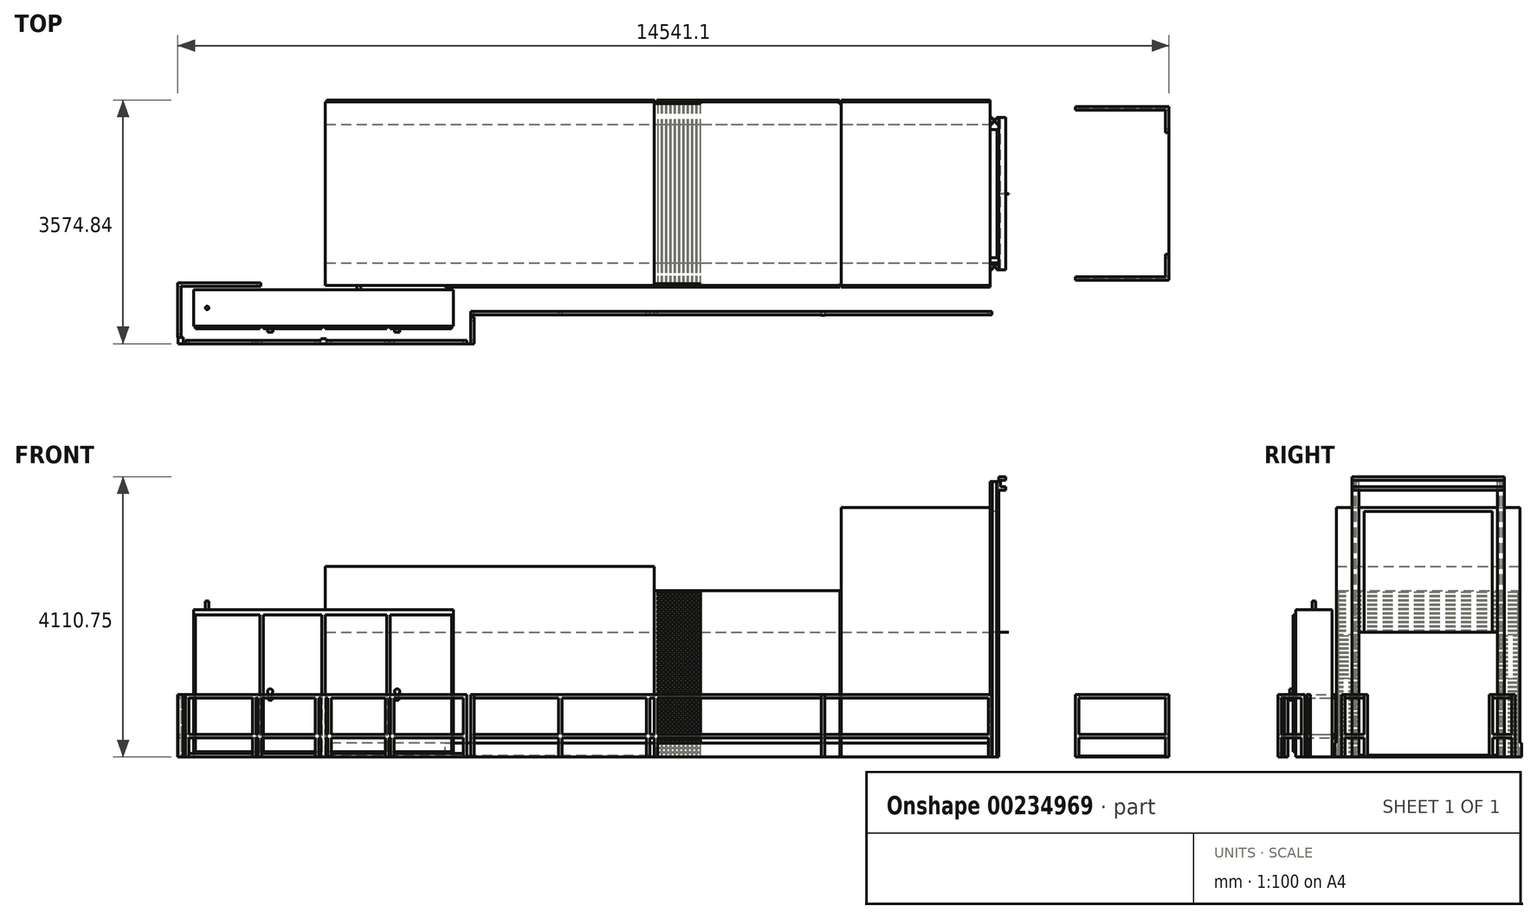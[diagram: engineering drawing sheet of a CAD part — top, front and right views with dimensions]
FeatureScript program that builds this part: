
annotation { "Feature Type Name" : "Feature", "Feature Type Description" : "" }
export const myFeature = defineFeature(function(context is Context, id is Id, definition is map)
    precondition{}
    {
        {
            var Q0;
            Q0=qCreatedBy(makeId("Top.planeOp"),FACE);
            var sketch = newSketch(context, id + "F0", { "sketchPlane" : qUnion([Q0])});
            skLineSegment(sketch, "E0.bottom", {"start": v(-1017.68, -307.3) * mm, "end": v(2792.32, -307.3) * mm});
            skLineSegment(sketch, "E0.top", {"start": v(-1017.68, 226.1) * mm, "end": v(2792.32, 226.1) * mm});
            skLineSegment(sketch, "E0.left", {"start": v(-1017.68, -307.3) * mm, "end": v(-1017.68, 226.1) * mm});
            skLineSegment(sketch, "E0.right", {"start": v(2792.32, -307.3) * mm, "end": v(2792.32, 226.1) * mm});
            skLineSegment(sketch, "E1.bottom", {"start": v(912.72, 289.6) * mm, "end": v(5738.72, 289.6) * mm});
            skLineSegment(sketch, "E1.top", {"start": v(912.72, 2982) * mm, "end": v(5738.72, 2982) * mm});
            skLineSegment(sketch, "E1.left", {"start": v(912.72, 289.6) * mm, "end": v(912.72, 2982) * mm});
            skLineSegment(sketch, "E1.right", {"start": v(5738.72, 289.6) * mm, "end": v(5738.72, 2982) * mm});
            skLineSegment(sketch, "E2.bottom", {"start": v(5738.72, 289.6) * mm, "end": v(8481.92, 289.6) * mm});
            skLineSegment(sketch, "E2.top", {"start": v(5738.72, 2982) * mm, "end": v(8481.92, 2982) * mm});
            skLineSegment(sketch, "E2.right", {"start": v(8481.92, 289.6) * mm, "end": v(8481.92, 2982) * mm});
            skLineSegment(sketch, "E3.bottom", {"start": v(8481.92, 289.6) * mm, "end": v(10666.32, 289.6) * mm});
            skLineSegment(sketch, "E3.top", {"start": v(8481.92, 2982) * mm, "end": v(10666.32, 2982) * mm});
            skLineSegment(sketch, "E3.right", {"start": v(10666.32, 289.6) * mm, "end": v(10666.32, 2982) * mm});
            skSolve(sketch);
        }
        {
            var Q0;
            Q0=makeQuery(id+"F0.imprint","IMPRINT",FACE,{"disambiguationData":[TD([[makeQuery(id+"F0.imprint","IMPRINT",EDGE,{"derivedFrom":sQuery(id+"F0.wireOp",EDGE,"E0.bottom")}),1.0]])]});
            extrude(context, id + "F1", {"entities" : qUnion([Q0]), "depth" : 2159 * mm});
        }
        {
            var Q0;
            Q0=makeQuery(id+"F0.imprint","IMPRINT",FACE,{"disambiguationData":[TD([[makeQuery(id+"F0.imprint","IMPRINT",EDGE,{"derivedFrom":sQuery(id+"F0.wireOp",EDGE,"E1.bottom")}),1.0]])]});
            extrude(context, id + "F2", {"entities" : qUnion([Q0]), "depth" : 2794 * mm});
        }
        {
            var Q0;
            Q0=makeQuery(id+"F0.imprint","IMPRINT",FACE,{"disambiguationData":[TD([[makeQuery(id+"F0.imprint","IMPRINT",EDGE,{"derivedFrom":sQuery(id+"F0.wireOp",EDGE,"E2.bottom")}),1.0]])]});
            extrude(context, id + "F3", {"entities" : qUnion([Q0]), "operationType" : NewBodyOperationType.ADD, "depth" : 2438.4 * mm});
        }
        {
            var Q0;
            Q0=makeQuery(id+"F0.imprint","IMPRINT",FACE,{"disambiguationData":[TD([[makeQuery(id+"F0.imprint","IMPRINT",EDGE,{"derivedFrom":sQuery(id+"F0.wireOp",EDGE,"E3.bottom")}),1.0]])]});
            extrude(context, id + "F4", {"entities" : qUnion([Q0]), "operationType" : NewBodyOperationType.ADD, "depth" : 3657.6 * mm});
        }
        {
            var Q0;
            Q0=makeQuery(id+"F4.boolean.opBoolean","MERGE",FACE,{"derivedFrom":[makeQuery(id+"F3.boolean.opBoolean","MERGE",FACE,{"derivedFrom":[makeQuery(id+"F2.opExtrude","SWEPT_FACE",FACE,{"disambiguationData":[OSD([sQuery(id+"F0.wireOp",EDGE,"E1.bottom")])]}),makeQuery(id+"F3.opExtrude","SWEPT_FACE",FACE,{"disambiguationData":[OSD([sQuery(id+"F0.wireOp",EDGE,"E2.bottom")])]})]}),makeQuery(id+"F4.opExtrude","SWEPT_FACE",FACE,{"disambiguationData":[OSD([sQuery(id+"F0.wireOp",EDGE,"E3.bottom")])]})]});
            var sketch = newSketch(context, id + "F5", { "sketchPlane" : qUnion([Q0])});
            skLineSegment(sketch, "E4.bottom", {"start": v(5787.37, 2413.96) * mm, "end": v(5838.17, 2413.96) * mm});
            skLineSegment(sketch, "E4.top", {"start": v(5787.37, 2363.16) * mm, "end": v(5838.17, 2363.16) * mm});
            skLineSegment(sketch, "E4.left", {"start": v(5787.37, 2413.96) * mm, "end": v(5787.37, 2363.16) * mm});
            skLineSegment(sketch, "E4.right", {"start": v(5838.17, 2413.96) * mm, "end": v(5838.17, 2363.16) * mm});
            skLineSegment(sketch, "E5.0.1.0", {"start": v(5787.37, 2350.46) * mm, "end": v(5838.17, 2350.46) * mm});
            skLineSegment(sketch, "E5.0.1.1", {"start": v(5838.17, 2350.46) * mm, "end": v(5838.17, 2299.66) * mm});
            skLineSegment(sketch, "E5.0.1.2", {"start": v(5787.37, 2350.46) * mm, "end": v(5787.37, 2299.66) * mm});
            skLineSegment(sketch, "E5.0.1.3", {"start": v(5787.37, 2299.66) * mm, "end": v(5838.17, 2299.66) * mm});
            skLineSegment(sketch, "E5.0.2.0", {"start": v(5787.37, 2286.96) * mm, "end": v(5838.17, 2286.96) * mm});
            skLineSegment(sketch, "E5.0.2.1", {"start": v(5838.17, 2286.96) * mm, "end": v(5838.17, 2236.16) * mm});
            skLineSegment(sketch, "E5.0.2.2", {"start": v(5787.37, 2286.96) * mm, "end": v(5787.37, 2236.16) * mm});
            skLineSegment(sketch, "E5.0.2.3", {"start": v(5787.37, 2236.16) * mm, "end": v(5838.17, 2236.16) * mm});
            skLineSegment(sketch, "E5.0.3.0", {"start": v(5787.37, 2223.46) * mm, "end": v(5838.17, 2223.46) * mm});
            skLineSegment(sketch, "E5.0.3.1", {"start": v(5838.17, 2223.46) * mm, "end": v(5838.17, 2172.66) * mm});
            skLineSegment(sketch, "E5.0.3.2", {"start": v(5787.37, 2223.46) * mm, "end": v(5787.37, 2172.66) * mm});
            skLineSegment(sketch, "E5.0.3.3", {"start": v(5787.37, 2172.66) * mm, "end": v(5838.17, 2172.66) * mm});
            skLineSegment(sketch, "E5.0.4.0", {"start": v(5787.37, 2159.96) * mm, "end": v(5838.17, 2159.96) * mm});
            skLineSegment(sketch, "E5.0.4.1", {"start": v(5838.17, 2159.96) * mm, "end": v(5838.17, 2109.16) * mm});
            skLineSegment(sketch, "E5.0.4.2", {"start": v(5787.37, 2159.96) * mm, "end": v(5787.37, 2109.16) * mm});
            skLineSegment(sketch, "E5.0.4.3", {"start": v(5787.37, 2109.16) * mm, "end": v(5838.17, 2109.16) * mm});
            skLineSegment(sketch, "E5.0.5.0", {"start": v(5787.37, 2096.46) * mm, "end": v(5838.17, 2096.46) * mm});
            skLineSegment(sketch, "E5.0.5.1", {"start": v(5838.17, 2096.46) * mm, "end": v(5838.17, 2045.66) * mm});
            skLineSegment(sketch, "E5.0.5.2", {"start": v(5787.37, 2096.46) * mm, "end": v(5787.37, 2045.66) * mm});
            skLineSegment(sketch, "E5.0.5.3", {"start": v(5787.37, 2045.66) * mm, "end": v(5838.17, 2045.66) * mm});
            skLineSegment(sketch, "E5.0.6.0", {"start": v(5787.37, 2032.96) * mm, "end": v(5838.17, 2032.96) * mm});
            skLineSegment(sketch, "E5.0.6.1", {"start": v(5838.17, 2032.96) * mm, "end": v(5838.17, 1982.16) * mm});
            skLineSegment(sketch, "E5.0.6.2", {"start": v(5787.37, 2032.96) * mm, "end": v(5787.37, 1982.16) * mm});
            skLineSegment(sketch, "E5.0.6.3", {"start": v(5787.37, 1982.16) * mm, "end": v(5838.17, 1982.16) * mm});
            skLineSegment(sketch, "E5.0.7.0", {"start": v(5787.37, 1969.46) * mm, "end": v(5838.17, 1969.46) * mm});
            skLineSegment(sketch, "E5.0.7.1", {"start": v(5838.17, 1969.46) * mm, "end": v(5838.17, 1918.66) * mm});
            skLineSegment(sketch, "E5.0.7.2", {"start": v(5787.37, 1969.46) * mm, "end": v(5787.37, 1918.66) * mm});
            skLineSegment(sketch, "E5.0.7.3", {"start": v(5787.37, 1918.66) * mm, "end": v(5838.17, 1918.66) * mm});
            skLineSegment(sketch, "E5.0.8.0", {"start": v(5787.37, 1905.96) * mm, "end": v(5838.17, 1905.96) * mm});
            skLineSegment(sketch, "E5.0.8.1", {"start": v(5838.17, 1905.96) * mm, "end": v(5838.17, 1855.16) * mm});
            skLineSegment(sketch, "E5.0.8.2", {"start": v(5787.37, 1905.96) * mm, "end": v(5787.37, 1855.16) * mm});
            skLineSegment(sketch, "E5.0.8.3", {"start": v(5787.37, 1855.16) * mm, "end": v(5838.17, 1855.16) * mm});
            skLineSegment(sketch, "E5.0.9.0", {"start": v(5787.37, 1842.46) * mm, "end": v(5838.17, 1842.46) * mm});
            skLineSegment(sketch, "E5.0.9.1", {"start": v(5838.17, 1842.46) * mm, "end": v(5838.17, 1791.66) * mm});
            skLineSegment(sketch, "E5.0.9.2", {"start": v(5787.37, 1842.46) * mm, "end": v(5787.37, 1791.66) * mm});
            skLineSegment(sketch, "E5.0.9.3", {"start": v(5787.37, 1791.66) * mm, "end": v(5838.17, 1791.66) * mm});
            skLineSegment(sketch, "E5.1.0.0", {"start": v(5850.87, 2413.96) * mm, "end": v(5901.67, 2413.96) * mm});
            skLineSegment(sketch, "E5.1.0.1", {"start": v(5901.67, 2413.96) * mm, "end": v(5901.67, 2363.16) * mm});
            skLineSegment(sketch, "E5.1.0.2", {"start": v(5850.87, 2413.96) * mm, "end": v(5850.87, 2363.16) * mm});
            skLineSegment(sketch, "E5.1.0.3", {"start": v(5850.87, 2363.16) * mm, "end": v(5901.67, 2363.16) * mm});
            skLineSegment(sketch, "E5.1.1.0", {"start": v(5850.87, 2350.46) * mm, "end": v(5901.67, 2350.46) * mm});
            skLineSegment(sketch, "E5.1.1.1", {"start": v(5901.67, 2350.46) * mm, "end": v(5901.67, 2299.66) * mm});
            skLineSegment(sketch, "E5.1.1.2", {"start": v(5850.87, 2350.46) * mm, "end": v(5850.87, 2299.66) * mm});
            skLineSegment(sketch, "E5.1.1.3", {"start": v(5850.87, 2299.66) * mm, "end": v(5901.67, 2299.66) * mm});
            skLineSegment(sketch, "E5.1.2.0", {"start": v(5850.87, 2286.96) * mm, "end": v(5901.67, 2286.96) * mm});
            skLineSegment(sketch, "E5.1.2.1", {"start": v(5901.67, 2286.96) * mm, "end": v(5901.67, 2236.16) * mm});
            skLineSegment(sketch, "E5.1.2.2", {"start": v(5850.87, 2286.96) * mm, "end": v(5850.87, 2236.16) * mm});
            skLineSegment(sketch, "E5.1.2.3", {"start": v(5850.87, 2236.16) * mm, "end": v(5901.67, 2236.16) * mm});
            skLineSegment(sketch, "E5.1.3.0", {"start": v(5850.87, 2223.46) * mm, "end": v(5901.67, 2223.46) * mm});
            skLineSegment(sketch, "E5.1.3.1", {"start": v(5901.67, 2223.46) * mm, "end": v(5901.67, 2172.66) * mm});
            skLineSegment(sketch, "E5.1.3.2", {"start": v(5850.87, 2223.46) * mm, "end": v(5850.87, 2172.66) * mm});
            skLineSegment(sketch, "E5.1.3.3", {"start": v(5850.87, 2172.66) * mm, "end": v(5901.67, 2172.66) * mm});
            skLineSegment(sketch, "E5.1.4.0", {"start": v(5850.87, 2159.96) * mm, "end": v(5901.67, 2159.96) * mm});
            skLineSegment(sketch, "E5.1.4.1", {"start": v(5901.67, 2159.96) * mm, "end": v(5901.67, 2109.16) * mm});
            skLineSegment(sketch, "E5.1.4.2", {"start": v(5850.87, 2159.96) * mm, "end": v(5850.87, 2109.16) * mm});
            skLineSegment(sketch, "E5.1.4.3", {"start": v(5850.87, 2109.16) * mm, "end": v(5901.67, 2109.16) * mm});
            skLineSegment(sketch, "E5.1.5.0", {"start": v(5850.87, 2096.46) * mm, "end": v(5901.67, 2096.46) * mm});
            skLineSegment(sketch, "E5.1.5.1", {"start": v(5901.67, 2096.46) * mm, "end": v(5901.67, 2045.66) * mm});
            skLineSegment(sketch, "E5.1.5.2", {"start": v(5850.87, 2096.46) * mm, "end": v(5850.87, 2045.66) * mm});
            skLineSegment(sketch, "E5.1.5.3", {"start": v(5850.87, 2045.66) * mm, "end": v(5901.67, 2045.66) * mm});
            skLineSegment(sketch, "E5.1.6.0", {"start": v(5850.87, 2032.96) * mm, "end": v(5901.67, 2032.96) * mm});
            skLineSegment(sketch, "E5.1.6.1", {"start": v(5901.67, 2032.96) * mm, "end": v(5901.67, 1982.16) * mm});
            skLineSegment(sketch, "E5.1.6.2", {"start": v(5850.87, 2032.96) * mm, "end": v(5850.87, 1982.16) * mm});
            skLineSegment(sketch, "E5.1.6.3", {"start": v(5850.87, 1982.16) * mm, "end": v(5901.67, 1982.16) * mm});
            skLineSegment(sketch, "E5.1.7.0", {"start": v(5850.87, 1969.46) * mm, "end": v(5901.67, 1969.46) * mm});
            skLineSegment(sketch, "E5.1.7.1", {"start": v(5901.67, 1969.46) * mm, "end": v(5901.67, 1918.66) * mm});
            skLineSegment(sketch, "E5.1.7.2", {"start": v(5850.87, 1969.46) * mm, "end": v(5850.87, 1918.66) * mm});
            skLineSegment(sketch, "E5.1.7.3", {"start": v(5850.87, 1918.66) * mm, "end": v(5901.67, 1918.66) * mm});
            skLineSegment(sketch, "E5.1.8.0", {"start": v(5850.87, 1905.96) * mm, "end": v(5901.67, 1905.96) * mm});
            skLineSegment(sketch, "E5.1.8.1", {"start": v(5901.67, 1905.96) * mm, "end": v(5901.67, 1855.16) * mm});
            skLineSegment(sketch, "E5.1.8.2", {"start": v(5850.87, 1905.96) * mm, "end": v(5850.87, 1855.16) * mm});
            skLineSegment(sketch, "E5.1.8.3", {"start": v(5850.87, 1855.16) * mm, "end": v(5901.67, 1855.16) * mm});
            skLineSegment(sketch, "E5.1.9.0", {"start": v(5850.87, 1842.46) * mm, "end": v(5901.67, 1842.46) * mm});
            skLineSegment(sketch, "E5.1.9.1", {"start": v(5901.67, 1842.46) * mm, "end": v(5901.67, 1791.66) * mm});
            skLineSegment(sketch, "E5.1.9.2", {"start": v(5850.87, 1842.46) * mm, "end": v(5850.87, 1791.66) * mm});
            skLineSegment(sketch, "E5.1.9.3", {"start": v(5850.87, 1791.66) * mm, "end": v(5901.67, 1791.66) * mm});
            skLineSegment(sketch, "E5.2.0.0", {"start": v(5914.37, 2413.96) * mm, "end": v(5965.17, 2413.96) * mm});
            skLineSegment(sketch, "E5.2.0.1", {"start": v(5965.17, 2413.96) * mm, "end": v(5965.17, 2363.16) * mm});
            skLineSegment(sketch, "E5.2.0.2", {"start": v(5914.37, 2413.96) * mm, "end": v(5914.37, 2363.16) * mm});
            skLineSegment(sketch, "E5.2.0.3", {"start": v(5914.37, 2363.16) * mm, "end": v(5965.17, 2363.16) * mm});
            skLineSegment(sketch, "E5.2.1.0", {"start": v(5914.37, 2350.46) * mm, "end": v(5965.17, 2350.46) * mm});
            skLineSegment(sketch, "E5.2.1.1", {"start": v(5965.17, 2350.46) * mm, "end": v(5965.17, 2299.66) * mm});
            skLineSegment(sketch, "E5.2.1.2", {"start": v(5914.37, 2350.46) * mm, "end": v(5914.37, 2299.66) * mm});
            skLineSegment(sketch, "E5.2.1.3", {"start": v(5914.37, 2299.66) * mm, "end": v(5965.17, 2299.66) * mm});
            skLineSegment(sketch, "E5.2.2.0", {"start": v(5914.37, 2286.96) * mm, "end": v(5965.17, 2286.96) * mm});
            skLineSegment(sketch, "E5.2.2.1", {"start": v(5965.17, 2286.96) * mm, "end": v(5965.17, 2236.16) * mm});
            skLineSegment(sketch, "E5.2.2.2", {"start": v(5914.37, 2286.96) * mm, "end": v(5914.37, 2236.16) * mm});
            skLineSegment(sketch, "E5.2.2.3", {"start": v(5914.37, 2236.16) * mm, "end": v(5965.17, 2236.16) * mm});
            skLineSegment(sketch, "E5.2.3.0", {"start": v(5914.37, 2223.46) * mm, "end": v(5965.17, 2223.46) * mm});
            skLineSegment(sketch, "E5.2.3.1", {"start": v(5965.17, 2223.46) * mm, "end": v(5965.17, 2172.66) * mm});
            skLineSegment(sketch, "E5.2.3.2", {"start": v(5914.37, 2223.46) * mm, "end": v(5914.37, 2172.66) * mm});
            skLineSegment(sketch, "E5.2.3.3", {"start": v(5914.37, 2172.66) * mm, "end": v(5965.17, 2172.66) * mm});
            skLineSegment(sketch, "E5.2.4.0", {"start": v(5914.37, 2159.96) * mm, "end": v(5965.17, 2159.96) * mm});
            skLineSegment(sketch, "E5.2.4.1", {"start": v(5965.17, 2159.96) * mm, "end": v(5965.17, 2109.16) * mm});
            skLineSegment(sketch, "E5.2.4.2", {"start": v(5914.37, 2159.96) * mm, "end": v(5914.37, 2109.16) * mm});
            skLineSegment(sketch, "E5.2.4.3", {"start": v(5914.37, 2109.16) * mm, "end": v(5965.17, 2109.16) * mm});
            skLineSegment(sketch, "E5.2.5.0", {"start": v(5914.37, 2096.46) * mm, "end": v(5965.17, 2096.46) * mm});
            skLineSegment(sketch, "E5.2.5.1", {"start": v(5965.17, 2096.46) * mm, "end": v(5965.17, 2045.66) * mm});
            skLineSegment(sketch, "E5.2.5.2", {"start": v(5914.37, 2096.46) * mm, "end": v(5914.37, 2045.66) * mm});
            skLineSegment(sketch, "E5.2.5.3", {"start": v(5914.37, 2045.66) * mm, "end": v(5965.17, 2045.66) * mm});
            skLineSegment(sketch, "E5.2.6.0", {"start": v(5914.37, 2032.96) * mm, "end": v(5965.17, 2032.96) * mm});
            skLineSegment(sketch, "E5.2.6.1", {"start": v(5965.17, 2032.96) * mm, "end": v(5965.17, 1982.16) * mm});
            skLineSegment(sketch, "E5.2.6.2", {"start": v(5914.37, 2032.96) * mm, "end": v(5914.37, 1982.16) * mm});
            skLineSegment(sketch, "E5.2.6.3", {"start": v(5914.37, 1982.16) * mm, "end": v(5965.17, 1982.16) * mm});
            skLineSegment(sketch, "E5.2.7.0", {"start": v(5914.37, 1969.46) * mm, "end": v(5965.17, 1969.46) * mm});
            skLineSegment(sketch, "E5.2.7.1", {"start": v(5965.17, 1969.46) * mm, "end": v(5965.17, 1918.66) * mm});
            skLineSegment(sketch, "E5.2.7.2", {"start": v(5914.37, 1969.46) * mm, "end": v(5914.37, 1918.66) * mm});
            skLineSegment(sketch, "E5.2.7.3", {"start": v(5914.37, 1918.66) * mm, "end": v(5965.17, 1918.66) * mm});
            skLineSegment(sketch, "E5.2.8.0", {"start": v(5914.37, 1905.96) * mm, "end": v(5965.17, 1905.96) * mm});
            skLineSegment(sketch, "E5.2.8.1", {"start": v(5965.17, 1905.96) * mm, "end": v(5965.17, 1855.16) * mm});
            skLineSegment(sketch, "E5.2.8.2", {"start": v(5914.37, 1905.96) * mm, "end": v(5914.37, 1855.16) * mm});
            skLineSegment(sketch, "E5.2.8.3", {"start": v(5914.37, 1855.16) * mm, "end": v(5965.17, 1855.16) * mm});
            skLineSegment(sketch, "E5.2.9.0", {"start": v(5914.37, 1842.46) * mm, "end": v(5965.17, 1842.46) * mm});
            skLineSegment(sketch, "E5.2.9.1", {"start": v(5965.17, 1842.46) * mm, "end": v(5965.17, 1791.66) * mm});
            skLineSegment(sketch, "E5.2.9.2", {"start": v(5914.37, 1842.46) * mm, "end": v(5914.37, 1791.66) * mm});
            skLineSegment(sketch, "E5.2.9.3", {"start": v(5914.37, 1791.66) * mm, "end": v(5965.17, 1791.66) * mm});
            skLineSegment(sketch, "E5.3.0.0", {"start": v(5977.87, 2413.96) * mm, "end": v(6028.67, 2413.96) * mm});
            skLineSegment(sketch, "E5.3.0.1", {"start": v(6028.67, 2413.96) * mm, "end": v(6028.67, 2363.16) * mm});
            skLineSegment(sketch, "E5.3.0.2", {"start": v(5977.87, 2413.96) * mm, "end": v(5977.87, 2363.16) * mm});
            skLineSegment(sketch, "E5.3.0.3", {"start": v(5977.87, 2363.16) * mm, "end": v(6028.67, 2363.16) * mm});
            skLineSegment(sketch, "E5.3.1.0", {"start": v(5977.87, 2350.46) * mm, "end": v(6028.67, 2350.46) * mm});
            skLineSegment(sketch, "E5.3.1.1", {"start": v(6028.67, 2350.46) * mm, "end": v(6028.67, 2299.66) * mm});
            skLineSegment(sketch, "E5.3.1.2", {"start": v(5977.87, 2350.46) * mm, "end": v(5977.87, 2299.66) * mm});
            skLineSegment(sketch, "E5.3.1.3", {"start": v(5977.87, 2299.66) * mm, "end": v(6028.67, 2299.66) * mm});
            skLineSegment(sketch, "E5.3.2.0", {"start": v(5977.87, 2286.96) * mm, "end": v(6028.67, 2286.96) * mm});
            skLineSegment(sketch, "E5.3.2.1", {"start": v(6028.67, 2286.96) * mm, "end": v(6028.67, 2236.16) * mm});
            skLineSegment(sketch, "E5.3.2.2", {"start": v(5977.87, 2286.96) * mm, "end": v(5977.87, 2236.16) * mm});
            skLineSegment(sketch, "E5.3.2.3", {"start": v(5977.87, 2236.16) * mm, "end": v(6028.67, 2236.16) * mm});
            skLineSegment(sketch, "E5.3.3.0", {"start": v(5977.87, 2223.46) * mm, "end": v(6028.67, 2223.46) * mm});
            skLineSegment(sketch, "E5.3.3.1", {"start": v(6028.67, 2223.46) * mm, "end": v(6028.67, 2172.66) * mm});
            skLineSegment(sketch, "E5.3.3.2", {"start": v(5977.87, 2223.46) * mm, "end": v(5977.87, 2172.66) * mm});
            skLineSegment(sketch, "E5.3.3.3", {"start": v(5977.87, 2172.66) * mm, "end": v(6028.67, 2172.66) * mm});
            skLineSegment(sketch, "E5.3.4.0", {"start": v(5977.87, 2159.96) * mm, "end": v(6028.67, 2159.96) * mm});
            skLineSegment(sketch, "E5.3.4.1", {"start": v(6028.67, 2159.96) * mm, "end": v(6028.67, 2109.16) * mm});
            skLineSegment(sketch, "E5.3.4.2", {"start": v(5977.87, 2159.96) * mm, "end": v(5977.87, 2109.16) * mm});
            skLineSegment(sketch, "E5.3.4.3", {"start": v(5977.87, 2109.16) * mm, "end": v(6028.67, 2109.16) * mm});
            skLineSegment(sketch, "E5.3.5.0", {"start": v(5977.87, 2096.46) * mm, "end": v(6028.67, 2096.46) * mm});
            skLineSegment(sketch, "E5.3.5.1", {"start": v(6028.67, 2096.46) * mm, "end": v(6028.67, 2045.66) * mm});
            skLineSegment(sketch, "E5.3.5.2", {"start": v(5977.87, 2096.46) * mm, "end": v(5977.87, 2045.66) * mm});
            skLineSegment(sketch, "E5.3.5.3", {"start": v(5977.87, 2045.66) * mm, "end": v(6028.67, 2045.66) * mm});
            skLineSegment(sketch, "E5.3.6.0", {"start": v(5977.87, 2032.96) * mm, "end": v(6028.67, 2032.96) * mm});
            skLineSegment(sketch, "E5.3.6.1", {"start": v(6028.67, 2032.96) * mm, "end": v(6028.67, 1982.16) * mm});
            skLineSegment(sketch, "E5.3.6.2", {"start": v(5977.87, 2032.96) * mm, "end": v(5977.87, 1982.16) * mm});
            skLineSegment(sketch, "E5.3.6.3", {"start": v(5977.87, 1982.16) * mm, "end": v(6028.67, 1982.16) * mm});
            skLineSegment(sketch, "E5.3.7.0", {"start": v(5977.87, 1969.46) * mm, "end": v(6028.67, 1969.46) * mm});
            skLineSegment(sketch, "E5.3.7.1", {"start": v(6028.67, 1969.46) * mm, "end": v(6028.67, 1918.66) * mm});
            skLineSegment(sketch, "E5.3.7.2", {"start": v(5977.87, 1969.46) * mm, "end": v(5977.87, 1918.66) * mm});
            skLineSegment(sketch, "E5.3.7.3", {"start": v(5977.87, 1918.66) * mm, "end": v(6028.67, 1918.66) * mm});
            skLineSegment(sketch, "E5.3.8.0", {"start": v(5977.87, 1905.96) * mm, "end": v(6028.67, 1905.96) * mm});
            skLineSegment(sketch, "E5.3.8.1", {"start": v(6028.67, 1905.96) * mm, "end": v(6028.67, 1855.16) * mm});
            skLineSegment(sketch, "E5.3.8.2", {"start": v(5977.87, 1905.96) * mm, "end": v(5977.87, 1855.16) * mm});
            skLineSegment(sketch, "E5.3.8.3", {"start": v(5977.87, 1855.16) * mm, "end": v(6028.67, 1855.16) * mm});
            skLineSegment(sketch, "E5.3.9.0", {"start": v(5977.87, 1842.46) * mm, "end": v(6028.67, 1842.46) * mm});
            skLineSegment(sketch, "E5.3.9.1", {"start": v(6028.67, 1842.46) * mm, "end": v(6028.67, 1791.66) * mm});
            skLineSegment(sketch, "E5.3.9.2", {"start": v(5977.87, 1842.46) * mm, "end": v(5977.87, 1791.66) * mm});
            skLineSegment(sketch, "E5.3.9.3", {"start": v(5977.87, 1791.66) * mm, "end": v(6028.67, 1791.66) * mm});
            skLineSegment(sketch, "E5.4.0.0", {"start": v(6041.37, 2413.96) * mm, "end": v(6092.17, 2413.96) * mm});
            skLineSegment(sketch, "E5.4.0.1", {"start": v(6092.17, 2413.96) * mm, "end": v(6092.17, 2363.16) * mm});
            skLineSegment(sketch, "E5.4.0.2", {"start": v(6041.37, 2413.96) * mm, "end": v(6041.37, 2363.16) * mm});
            skLineSegment(sketch, "E5.4.0.3", {"start": v(6041.37, 2363.16) * mm, "end": v(6092.17, 2363.16) * mm});
            skLineSegment(sketch, "E5.4.1.0", {"start": v(6041.37, 2350.46) * mm, "end": v(6092.17, 2350.46) * mm});
            skLineSegment(sketch, "E5.4.1.1", {"start": v(6092.17, 2350.46) * mm, "end": v(6092.17, 2299.66) * mm});
            skLineSegment(sketch, "E5.4.1.2", {"start": v(6041.37, 2350.46) * mm, "end": v(6041.37, 2299.66) * mm});
            skLineSegment(sketch, "E5.4.1.3", {"start": v(6041.37, 2299.66) * mm, "end": v(6092.17, 2299.66) * mm});
            skLineSegment(sketch, "E5.4.2.0", {"start": v(6041.37, 2286.96) * mm, "end": v(6092.17, 2286.96) * mm});
            skLineSegment(sketch, "E5.4.2.1", {"start": v(6092.17, 2286.96) * mm, "end": v(6092.17, 2236.16) * mm});
            skLineSegment(sketch, "E5.4.2.2", {"start": v(6041.37, 2286.96) * mm, "end": v(6041.37, 2236.16) * mm});
            skLineSegment(sketch, "E5.4.2.3", {"start": v(6041.37, 2236.16) * mm, "end": v(6092.17, 2236.16) * mm});
            skLineSegment(sketch, "E5.4.3.0", {"start": v(6041.37, 2223.46) * mm, "end": v(6092.17, 2223.46) * mm});
            skLineSegment(sketch, "E5.4.3.1", {"start": v(6092.17, 2223.46) * mm, "end": v(6092.17, 2172.66) * mm});
            skLineSegment(sketch, "E5.4.3.2", {"start": v(6041.37, 2223.46) * mm, "end": v(6041.37, 2172.66) * mm});
            skLineSegment(sketch, "E5.4.3.3", {"start": v(6041.37, 2172.66) * mm, "end": v(6092.17, 2172.66) * mm});
            skLineSegment(sketch, "E5.4.4.0", {"start": v(6041.37, 2159.96) * mm, "end": v(6092.17, 2159.96) * mm});
            skLineSegment(sketch, "E5.4.4.1", {"start": v(6092.17, 2159.96) * mm, "end": v(6092.17, 2109.16) * mm});
            skLineSegment(sketch, "E5.4.4.2", {"start": v(6041.37, 2159.96) * mm, "end": v(6041.37, 2109.16) * mm});
            skLineSegment(sketch, "E5.4.4.3", {"start": v(6041.37, 2109.16) * mm, "end": v(6092.17, 2109.16) * mm});
            skLineSegment(sketch, "E5.4.5.0", {"start": v(6041.37, 2096.46) * mm, "end": v(6092.17, 2096.46) * mm});
            skLineSegment(sketch, "E5.4.5.1", {"start": v(6092.17, 2096.46) * mm, "end": v(6092.17, 2045.66) * mm});
            skLineSegment(sketch, "E5.4.5.2", {"start": v(6041.37, 2096.46) * mm, "end": v(6041.37, 2045.66) * mm});
            skLineSegment(sketch, "E5.4.5.3", {"start": v(6041.37, 2045.66) * mm, "end": v(6092.17, 2045.66) * mm});
            skLineSegment(sketch, "E5.4.6.0", {"start": v(6041.37, 2032.96) * mm, "end": v(6092.17, 2032.96) * mm});
            skLineSegment(sketch, "E5.4.6.1", {"start": v(6092.17, 2032.96) * mm, "end": v(6092.17, 1982.16) * mm});
            skLineSegment(sketch, "E5.4.6.2", {"start": v(6041.37, 2032.96) * mm, "end": v(6041.37, 1982.16) * mm});
            skLineSegment(sketch, "E5.4.6.3", {"start": v(6041.37, 1982.16) * mm, "end": v(6092.17, 1982.16) * mm});
            skLineSegment(sketch, "E5.4.7.0", {"start": v(6041.37, 1969.46) * mm, "end": v(6092.17, 1969.46) * mm});
            skLineSegment(sketch, "E5.4.7.1", {"start": v(6092.17, 1969.46) * mm, "end": v(6092.17, 1918.66) * mm});
            skLineSegment(sketch, "E5.4.7.2", {"start": v(6041.37, 1969.46) * mm, "end": v(6041.37, 1918.66) * mm});
            skLineSegment(sketch, "E5.4.7.3", {"start": v(6041.37, 1918.66) * mm, "end": v(6092.17, 1918.66) * mm});
            skLineSegment(sketch, "E5.4.8.0", {"start": v(6041.37, 1905.96) * mm, "end": v(6092.17, 1905.96) * mm});
            skLineSegment(sketch, "E5.4.8.1", {"start": v(6092.17, 1905.96) * mm, "end": v(6092.17, 1855.16) * mm});
            skLineSegment(sketch, "E5.4.8.2", {"start": v(6041.37, 1905.96) * mm, "end": v(6041.37, 1855.16) * mm});
            skLineSegment(sketch, "E5.4.8.3", {"start": v(6041.37, 1855.16) * mm, "end": v(6092.17, 1855.16) * mm});
            skLineSegment(sketch, "E5.4.9.0", {"start": v(6041.37, 1842.46) * mm, "end": v(6092.17, 1842.46) * mm});
            skLineSegment(sketch, "E5.4.9.1", {"start": v(6092.17, 1842.46) * mm, "end": v(6092.17, 1791.66) * mm});
            skLineSegment(sketch, "E5.4.9.2", {"start": v(6041.37, 1842.46) * mm, "end": v(6041.37, 1791.66) * mm});
            skLineSegment(sketch, "E5.4.9.3", {"start": v(6041.37, 1791.66) * mm, "end": v(6092.17, 1791.66) * mm});
            skLineSegment(sketch, "E5.5.0.0", {"start": v(6104.87, 2413.96) * mm, "end": v(6155.67, 2413.96) * mm});
            skLineSegment(sketch, "E5.5.0.1", {"start": v(6155.67, 2413.96) * mm, "end": v(6155.67, 2363.16) * mm});
            skLineSegment(sketch, "E5.5.0.2", {"start": v(6104.87, 2413.96) * mm, "end": v(6104.87, 2363.16) * mm});
            skLineSegment(sketch, "E5.5.0.3", {"start": v(6104.87, 2363.16) * mm, "end": v(6155.67, 2363.16) * mm});
            skLineSegment(sketch, "E5.5.1.0", {"start": v(6104.87, 2350.46) * mm, "end": v(6155.67, 2350.46) * mm});
            skLineSegment(sketch, "E5.5.1.1", {"start": v(6155.67, 2350.46) * mm, "end": v(6155.67, 2299.66) * mm});
            skLineSegment(sketch, "E5.5.1.2", {"start": v(6104.87, 2350.46) * mm, "end": v(6104.87, 2299.66) * mm});
            skLineSegment(sketch, "E5.5.1.3", {"start": v(6104.87, 2299.66) * mm, "end": v(6155.67, 2299.66) * mm});
            skLineSegment(sketch, "E5.5.2.0", {"start": v(6104.87, 2286.96) * mm, "end": v(6155.67, 2286.96) * mm});
            skLineSegment(sketch, "E5.5.2.1", {"start": v(6155.67, 2286.96) * mm, "end": v(6155.67, 2236.16) * mm});
            skLineSegment(sketch, "E5.5.2.2", {"start": v(6104.87, 2286.96) * mm, "end": v(6104.87, 2236.16) * mm});
            skLineSegment(sketch, "E5.5.2.3", {"start": v(6104.87, 2236.16) * mm, "end": v(6155.67, 2236.16) * mm});
            skLineSegment(sketch, "E5.5.3.0", {"start": v(6104.87, 2223.46) * mm, "end": v(6155.67, 2223.46) * mm});
            skLineSegment(sketch, "E5.5.3.1", {"start": v(6155.67, 2223.46) * mm, "end": v(6155.67, 2172.66) * mm});
            skLineSegment(sketch, "E5.5.3.2", {"start": v(6104.87, 2223.46) * mm, "end": v(6104.87, 2172.66) * mm});
            skLineSegment(sketch, "E5.5.3.3", {"start": v(6104.87, 2172.66) * mm, "end": v(6155.67, 2172.66) * mm});
            skLineSegment(sketch, "E5.5.4.0", {"start": v(6104.87, 2159.96) * mm, "end": v(6155.67, 2159.96) * mm});
            skLineSegment(sketch, "E5.5.4.1", {"start": v(6155.67, 2159.96) * mm, "end": v(6155.67, 2109.16) * mm});
            skLineSegment(sketch, "E5.5.4.2", {"start": v(6104.87, 2159.96) * mm, "end": v(6104.87, 2109.16) * mm});
            skLineSegment(sketch, "E5.5.4.3", {"start": v(6104.87, 2109.16) * mm, "end": v(6155.67, 2109.16) * mm});
            skLineSegment(sketch, "E5.5.5.0", {"start": v(6104.87, 2096.46) * mm, "end": v(6155.67, 2096.46) * mm});
            skLineSegment(sketch, "E5.5.5.1", {"start": v(6155.67, 2096.46) * mm, "end": v(6155.67, 2045.66) * mm});
            skLineSegment(sketch, "E5.5.5.2", {"start": v(6104.87, 2096.46) * mm, "end": v(6104.87, 2045.66) * mm});
            skLineSegment(sketch, "E5.5.5.3", {"start": v(6104.87, 2045.66) * mm, "end": v(6155.67, 2045.66) * mm});
            skLineSegment(sketch, "E5.5.6.0", {"start": v(6104.87, 2032.96) * mm, "end": v(6155.67, 2032.96) * mm});
            skLineSegment(sketch, "E5.5.6.1", {"start": v(6155.67, 2032.96) * mm, "end": v(6155.67, 1982.16) * mm});
            skLineSegment(sketch, "E5.5.6.2", {"start": v(6104.87, 2032.96) * mm, "end": v(6104.87, 1982.16) * mm});
            skLineSegment(sketch, "E5.5.6.3", {"start": v(6104.87, 1982.16) * mm, "end": v(6155.67, 1982.16) * mm});
            skLineSegment(sketch, "E5.5.7.0", {"start": v(6104.87, 1969.46) * mm, "end": v(6155.67, 1969.46) * mm});
            skLineSegment(sketch, "E5.5.7.1", {"start": v(6155.67, 1969.46) * mm, "end": v(6155.67, 1918.66) * mm});
            skLineSegment(sketch, "E5.5.7.2", {"start": v(6104.87, 1969.46) * mm, "end": v(6104.87, 1918.66) * mm});
            skLineSegment(sketch, "E5.5.7.3", {"start": v(6104.87, 1918.66) * mm, "end": v(6155.67, 1918.66) * mm});
            skLineSegment(sketch, "E5.5.8.0", {"start": v(6104.87, 1905.96) * mm, "end": v(6155.67, 1905.96) * mm});
            skLineSegment(sketch, "E5.5.8.1", {"start": v(6155.67, 1905.96) * mm, "end": v(6155.67, 1855.16) * mm});
            skLineSegment(sketch, "E5.5.8.2", {"start": v(6104.87, 1905.96) * mm, "end": v(6104.87, 1855.16) * mm});
            skLineSegment(sketch, "E5.5.8.3", {"start": v(6104.87, 1855.16) * mm, "end": v(6155.67, 1855.16) * mm});
            skLineSegment(sketch, "E5.5.9.0", {"start": v(6104.87, 1842.46) * mm, "end": v(6155.67, 1842.46) * mm});
            skLineSegment(sketch, "E5.5.9.1", {"start": v(6155.67, 1842.46) * mm, "end": v(6155.67, 1791.66) * mm});
            skLineSegment(sketch, "E5.5.9.2", {"start": v(6104.87, 1842.46) * mm, "end": v(6104.87, 1791.66) * mm});
            skLineSegment(sketch, "E5.5.9.3", {"start": v(6104.87, 1791.66) * mm, "end": v(6155.67, 1791.66) * mm});
            skLineSegment(sketch, "E5.6.0.0", {"start": v(6168.37, 2413.96) * mm, "end": v(6219.17, 2413.96) * mm});
            skLineSegment(sketch, "E5.6.0.1", {"start": v(6219.17, 2413.96) * mm, "end": v(6219.17, 2363.16) * mm});
            skLineSegment(sketch, "E5.6.0.2", {"start": v(6168.37, 2413.96) * mm, "end": v(6168.37, 2363.16) * mm});
            skLineSegment(sketch, "E5.6.0.3", {"start": v(6168.37, 2363.16) * mm, "end": v(6219.17, 2363.16) * mm});
            skLineSegment(sketch, "E5.6.1.0", {"start": v(6168.37, 2350.46) * mm, "end": v(6219.17, 2350.46) * mm});
            skLineSegment(sketch, "E5.6.1.1", {"start": v(6219.17, 2350.46) * mm, "end": v(6219.17, 2299.66) * mm});
            skLineSegment(sketch, "E5.6.1.2", {"start": v(6168.37, 2350.46) * mm, "end": v(6168.37, 2299.66) * mm});
            skLineSegment(sketch, "E5.6.1.3", {"start": v(6168.37, 2299.66) * mm, "end": v(6219.17, 2299.66) * mm});
            skLineSegment(sketch, "E5.6.2.0", {"start": v(6168.37, 2286.96) * mm, "end": v(6219.17, 2286.96) * mm});
            skLineSegment(sketch, "E5.6.2.1", {"start": v(6219.17, 2286.96) * mm, "end": v(6219.17, 2236.16) * mm});
            skLineSegment(sketch, "E5.6.2.2", {"start": v(6168.37, 2286.96) * mm, "end": v(6168.37, 2236.16) * mm});
            skLineSegment(sketch, "E5.6.2.3", {"start": v(6168.37, 2236.16) * mm, "end": v(6219.17, 2236.16) * mm});
            skLineSegment(sketch, "E5.6.3.0", {"start": v(6168.37, 2223.46) * mm, "end": v(6219.17, 2223.46) * mm});
            skLineSegment(sketch, "E5.6.3.1", {"start": v(6219.17, 2223.46) * mm, "end": v(6219.17, 2172.66) * mm});
            skLineSegment(sketch, "E5.6.3.2", {"start": v(6168.37, 2223.46) * mm, "end": v(6168.37, 2172.66) * mm});
            skLineSegment(sketch, "E5.6.3.3", {"start": v(6168.37, 2172.66) * mm, "end": v(6219.17, 2172.66) * mm});
            skLineSegment(sketch, "E5.6.4.0", {"start": v(6168.37, 2159.96) * mm, "end": v(6219.17, 2159.96) * mm});
            skLineSegment(sketch, "E5.6.4.1", {"start": v(6219.17, 2159.96) * mm, "end": v(6219.17, 2109.16) * mm});
            skLineSegment(sketch, "E5.6.4.2", {"start": v(6168.37, 2159.96) * mm, "end": v(6168.37, 2109.16) * mm});
            skLineSegment(sketch, "E5.6.4.3", {"start": v(6168.37, 2109.16) * mm, "end": v(6219.17, 2109.16) * mm});
            skLineSegment(sketch, "E5.6.5.0", {"start": v(6168.37, 2096.46) * mm, "end": v(6219.17, 2096.46) * mm});
            skLineSegment(sketch, "E5.6.5.1", {"start": v(6219.17, 2096.46) * mm, "end": v(6219.17, 2045.66) * mm});
            skLineSegment(sketch, "E5.6.5.2", {"start": v(6168.37, 2096.46) * mm, "end": v(6168.37, 2045.66) * mm});
            skLineSegment(sketch, "E5.6.5.3", {"start": v(6168.37, 2045.66) * mm, "end": v(6219.17, 2045.66) * mm});
            skLineSegment(sketch, "E5.6.6.0", {"start": v(6168.37, 2032.96) * mm, "end": v(6219.17, 2032.96) * mm});
            skLineSegment(sketch, "E5.6.6.1", {"start": v(6219.17, 2032.96) * mm, "end": v(6219.17, 1982.16) * mm});
            skLineSegment(sketch, "E5.6.6.2", {"start": v(6168.37, 2032.96) * mm, "end": v(6168.37, 1982.16) * mm});
            skLineSegment(sketch, "E5.6.6.3", {"start": v(6168.37, 1982.16) * mm, "end": v(6219.17, 1982.16) * mm});
            skLineSegment(sketch, "E5.6.7.0", {"start": v(6168.37, 1969.46) * mm, "end": v(6219.17, 1969.46) * mm});
            skLineSegment(sketch, "E5.6.7.1", {"start": v(6219.17, 1969.46) * mm, "end": v(6219.17, 1918.66) * mm});
            skLineSegment(sketch, "E5.6.7.2", {"start": v(6168.37, 1969.46) * mm, "end": v(6168.37, 1918.66) * mm});
            skLineSegment(sketch, "E5.6.7.3", {"start": v(6168.37, 1918.66) * mm, "end": v(6219.17, 1918.66) * mm});
            skLineSegment(sketch, "E5.6.8.0", {"start": v(6168.37, 1905.96) * mm, "end": v(6219.17, 1905.96) * mm});
            skLineSegment(sketch, "E5.6.8.1", {"start": v(6219.17, 1905.96) * mm, "end": v(6219.17, 1855.16) * mm});
            skLineSegment(sketch, "E5.6.8.2", {"start": v(6168.37, 1905.96) * mm, "end": v(6168.37, 1855.16) * mm});
            skLineSegment(sketch, "E5.6.8.3", {"start": v(6168.37, 1855.16) * mm, "end": v(6219.17, 1855.16) * mm});
            skLineSegment(sketch, "E5.6.9.0", {"start": v(6168.37, 1842.46) * mm, "end": v(6219.17, 1842.46) * mm});
            skLineSegment(sketch, "E5.6.9.1", {"start": v(6219.17, 1842.46) * mm, "end": v(6219.17, 1791.66) * mm});
            skLineSegment(sketch, "E5.6.9.2", {"start": v(6168.37, 1842.46) * mm, "end": v(6168.37, 1791.66) * mm});
            skLineSegment(sketch, "E5.6.9.3", {"start": v(6168.37, 1791.66) * mm, "end": v(6219.17, 1791.66) * mm});
            skLineSegment(sketch, "E5.7.0.0", {"start": v(6231.87, 2413.96) * mm, "end": v(6282.67, 2413.96) * mm});
            skLineSegment(sketch, "E5.7.0.1", {"start": v(6282.67, 2413.96) * mm, "end": v(6282.67, 2363.16) * mm});
            skLineSegment(sketch, "E5.7.0.2", {"start": v(6231.87, 2413.96) * mm, "end": v(6231.87, 2363.16) * mm});
            skLineSegment(sketch, "E5.7.0.3", {"start": v(6231.87, 2363.16) * mm, "end": v(6282.67, 2363.16) * mm});
            skLineSegment(sketch, "E5.7.1.0", {"start": v(6231.87, 2350.46) * mm, "end": v(6282.67, 2350.46) * mm});
            skLineSegment(sketch, "E5.7.1.1", {"start": v(6282.67, 2350.46) * mm, "end": v(6282.67, 2299.66) * mm});
            skLineSegment(sketch, "E5.7.1.2", {"start": v(6231.87, 2350.46) * mm, "end": v(6231.87, 2299.66) * mm});
            skLineSegment(sketch, "E5.7.1.3", {"start": v(6231.87, 2299.66) * mm, "end": v(6282.67, 2299.66) * mm});
            skLineSegment(sketch, "E5.7.2.0", {"start": v(6231.87, 2286.96) * mm, "end": v(6282.67, 2286.96) * mm});
            skLineSegment(sketch, "E5.7.2.1", {"start": v(6282.67, 2286.96) * mm, "end": v(6282.67, 2236.16) * mm});
            skLineSegment(sketch, "E5.7.2.2", {"start": v(6231.87, 2286.96) * mm, "end": v(6231.87, 2236.16) * mm});
            skLineSegment(sketch, "E5.7.2.3", {"start": v(6231.87, 2236.16) * mm, "end": v(6282.67, 2236.16) * mm});
            skLineSegment(sketch, "E5.7.3.0", {"start": v(6231.87, 2223.46) * mm, "end": v(6282.67, 2223.46) * mm});
            skLineSegment(sketch, "E5.7.3.1", {"start": v(6282.67, 2223.46) * mm, "end": v(6282.67, 2172.66) * mm});
            skLineSegment(sketch, "E5.7.3.2", {"start": v(6231.87, 2223.46) * mm, "end": v(6231.87, 2172.66) * mm});
            skLineSegment(sketch, "E5.7.3.3", {"start": v(6231.87, 2172.66) * mm, "end": v(6282.67, 2172.66) * mm});
            skLineSegment(sketch, "E5.7.4.0", {"start": v(6231.87, 2159.96) * mm, "end": v(6282.67, 2159.96) * mm});
            skLineSegment(sketch, "E5.7.4.1", {"start": v(6282.67, 2159.96) * mm, "end": v(6282.67, 2109.16) * mm});
            skLineSegment(sketch, "E5.7.4.2", {"start": v(6231.87, 2159.96) * mm, "end": v(6231.87, 2109.16) * mm});
            skLineSegment(sketch, "E5.7.4.3", {"start": v(6231.87, 2109.16) * mm, "end": v(6282.67, 2109.16) * mm});
            skLineSegment(sketch, "E5.7.5.0", {"start": v(6231.87, 2096.46) * mm, "end": v(6282.67, 2096.46) * mm});
            skLineSegment(sketch, "E5.7.5.1", {"start": v(6282.67, 2096.46) * mm, "end": v(6282.67, 2045.66) * mm});
            skLineSegment(sketch, "E5.7.5.2", {"start": v(6231.87, 2096.46) * mm, "end": v(6231.87, 2045.66) * mm});
            skLineSegment(sketch, "E5.7.5.3", {"start": v(6231.87, 2045.66) * mm, "end": v(6282.67, 2045.66) * mm});
            skLineSegment(sketch, "E5.7.6.0", {"start": v(6231.87, 2032.96) * mm, "end": v(6282.67, 2032.96) * mm});
            skLineSegment(sketch, "E5.7.6.1", {"start": v(6282.67, 2032.96) * mm, "end": v(6282.67, 1982.16) * mm});
            skLineSegment(sketch, "E5.7.6.2", {"start": v(6231.87, 2032.96) * mm, "end": v(6231.87, 1982.16) * mm});
            skLineSegment(sketch, "E5.7.6.3", {"start": v(6231.87, 1982.16) * mm, "end": v(6282.67, 1982.16) * mm});
            skLineSegment(sketch, "E5.7.7.0", {"start": v(6231.87, 1969.46) * mm, "end": v(6282.67, 1969.46) * mm});
            skLineSegment(sketch, "E5.7.7.1", {"start": v(6282.67, 1969.46) * mm, "end": v(6282.67, 1918.66) * mm});
            skLineSegment(sketch, "E5.7.7.2", {"start": v(6231.87, 1969.46) * mm, "end": v(6231.87, 1918.66) * mm});
            skLineSegment(sketch, "E5.7.7.3", {"start": v(6231.87, 1918.66) * mm, "end": v(6282.67, 1918.66) * mm});
            skLineSegment(sketch, "E5.7.8.0", {"start": v(6231.87, 1905.96) * mm, "end": v(6282.67, 1905.96) * mm});
            skLineSegment(sketch, "E5.7.8.1", {"start": v(6282.67, 1905.96) * mm, "end": v(6282.67, 1855.16) * mm});
            skLineSegment(sketch, "E5.7.8.2", {"start": v(6231.87, 1905.96) * mm, "end": v(6231.87, 1855.16) * mm});
            skLineSegment(sketch, "E5.7.8.3", {"start": v(6231.87, 1855.16) * mm, "end": v(6282.67, 1855.16) * mm});
            skLineSegment(sketch, "E5.7.9.0", {"start": v(6231.87, 1842.46) * mm, "end": v(6282.67, 1842.46) * mm});
            skLineSegment(sketch, "E5.7.9.1", {"start": v(6282.67, 1842.46) * mm, "end": v(6282.67, 1791.66) * mm});
            skLineSegment(sketch, "E5.7.9.2", {"start": v(6231.87, 1842.46) * mm, "end": v(6231.87, 1791.66) * mm});
            skLineSegment(sketch, "E5.7.9.3", {"start": v(6231.87, 1791.66) * mm, "end": v(6282.67, 1791.66) * mm});
            skLineSegment(sketch, "E5.8.0.0", {"start": v(6295.37, 2413.96) * mm, "end": v(6346.17, 2413.96) * mm});
            skLineSegment(sketch, "E5.8.0.1", {"start": v(6346.17, 2413.96) * mm, "end": v(6346.17, 2363.16) * mm});
            skLineSegment(sketch, "E5.8.0.2", {"start": v(6295.37, 2413.96) * mm, "end": v(6295.37, 2363.16) * mm});
            skLineSegment(sketch, "E5.8.0.3", {"start": v(6295.37, 2363.16) * mm, "end": v(6346.17, 2363.16) * mm});
            skLineSegment(sketch, "E5.8.1.0", {"start": v(6295.37, 2350.46) * mm, "end": v(6346.17, 2350.46) * mm});
            skLineSegment(sketch, "E5.8.1.1", {"start": v(6346.17, 2350.46) * mm, "end": v(6346.17, 2299.66) * mm});
            skLineSegment(sketch, "E5.8.1.2", {"start": v(6295.37, 2350.46) * mm, "end": v(6295.37, 2299.66) * mm});
            skLineSegment(sketch, "E5.8.1.3", {"start": v(6295.37, 2299.66) * mm, "end": v(6346.17, 2299.66) * mm});
            skLineSegment(sketch, "E5.8.2.0", {"start": v(6295.37, 2286.96) * mm, "end": v(6346.17, 2286.96) * mm});
            skLineSegment(sketch, "E5.8.2.1", {"start": v(6346.17, 2286.96) * mm, "end": v(6346.17, 2236.16) * mm});
            skLineSegment(sketch, "E5.8.2.2", {"start": v(6295.37, 2286.96) * mm, "end": v(6295.37, 2236.16) * mm});
            skLineSegment(sketch, "E5.8.2.3", {"start": v(6295.37, 2236.16) * mm, "end": v(6346.17, 2236.16) * mm});
            skLineSegment(sketch, "E5.8.3.0", {"start": v(6295.37, 2223.46) * mm, "end": v(6346.17, 2223.46) * mm});
            skLineSegment(sketch, "E5.8.3.1", {"start": v(6346.17, 2223.46) * mm, "end": v(6346.17, 2172.66) * mm});
            skLineSegment(sketch, "E5.8.3.2", {"start": v(6295.37, 2223.46) * mm, "end": v(6295.37, 2172.66) * mm});
            skLineSegment(sketch, "E5.8.3.3", {"start": v(6295.37, 2172.66) * mm, "end": v(6346.17, 2172.66) * mm});
            skLineSegment(sketch, "E5.8.4.0", {"start": v(6295.37, 2159.96) * mm, "end": v(6346.17, 2159.96) * mm});
            skLineSegment(sketch, "E5.8.4.1", {"start": v(6346.17, 2159.96) * mm, "end": v(6346.17, 2109.16) * mm});
            skLineSegment(sketch, "E5.8.4.2", {"start": v(6295.37, 2159.96) * mm, "end": v(6295.37, 2109.16) * mm});
            skLineSegment(sketch, "E5.8.4.3", {"start": v(6295.37, 2109.16) * mm, "end": v(6346.17, 2109.16) * mm});
            skLineSegment(sketch, "E5.8.5.0", {"start": v(6295.37, 2096.46) * mm, "end": v(6346.17, 2096.46) * mm});
            skLineSegment(sketch, "E5.8.5.1", {"start": v(6346.17, 2096.46) * mm, "end": v(6346.17, 2045.66) * mm});
            skLineSegment(sketch, "E5.8.5.2", {"start": v(6295.37, 2096.46) * mm, "end": v(6295.37, 2045.66) * mm});
            skLineSegment(sketch, "E5.8.5.3", {"start": v(6295.37, 2045.66) * mm, "end": v(6346.17, 2045.66) * mm});
            skLineSegment(sketch, "E5.8.6.0", {"start": v(6295.37, 2032.96) * mm, "end": v(6346.17, 2032.96) * mm});
            skLineSegment(sketch, "E5.8.6.1", {"start": v(6346.17, 2032.96) * mm, "end": v(6346.17, 1982.16) * mm});
            skLineSegment(sketch, "E5.8.6.2", {"start": v(6295.37, 2032.96) * mm, "end": v(6295.37, 1982.16) * mm});
            skLineSegment(sketch, "E5.8.6.3", {"start": v(6295.37, 1982.16) * mm, "end": v(6346.17, 1982.16) * mm});
            skLineSegment(sketch, "E5.8.7.0", {"start": v(6295.37, 1969.46) * mm, "end": v(6346.17, 1969.46) * mm});
            skLineSegment(sketch, "E5.8.7.1", {"start": v(6346.17, 1969.46) * mm, "end": v(6346.17, 1918.66) * mm});
            skLineSegment(sketch, "E5.8.7.2", {"start": v(6295.37, 1969.46) * mm, "end": v(6295.37, 1918.66) * mm});
            skLineSegment(sketch, "E5.8.7.3", {"start": v(6295.37, 1918.66) * mm, "end": v(6346.17, 1918.66) * mm});
            skLineSegment(sketch, "E5.8.8.0", {"start": v(6295.37, 1905.96) * mm, "end": v(6346.17, 1905.96) * mm});
            skLineSegment(sketch, "E5.8.8.1", {"start": v(6346.17, 1905.96) * mm, "end": v(6346.17, 1855.16) * mm});
            skLineSegment(sketch, "E5.8.8.2", {"start": v(6295.37, 1905.96) * mm, "end": v(6295.37, 1855.16) * mm});
            skLineSegment(sketch, "E5.8.8.3", {"start": v(6295.37, 1855.16) * mm, "end": v(6346.17, 1855.16) * mm});
            skLineSegment(sketch, "E5.8.9.0", {"start": v(6295.37, 1842.46) * mm, "end": v(6346.17, 1842.46) * mm});
            skLineSegment(sketch, "E5.8.9.1", {"start": v(6346.17, 1842.46) * mm, "end": v(6346.17, 1791.66) * mm});
            skLineSegment(sketch, "E5.8.9.2", {"start": v(6295.37, 1842.46) * mm, "end": v(6295.37, 1791.66) * mm});
            skLineSegment(sketch, "E5.8.9.3", {"start": v(6295.37, 1791.66) * mm, "end": v(6346.17, 1791.66) * mm});
            skLineSegment(sketch, "E5.9.0.0", {"start": v(6358.87, 2413.96) * mm, "end": v(6409.67, 2413.96) * mm});
            skLineSegment(sketch, "E5.9.0.1", {"start": v(6409.67, 2413.96) * mm, "end": v(6409.67, 2363.16) * mm});
            skLineSegment(sketch, "E5.9.0.2", {"start": v(6358.87, 2413.96) * mm, "end": v(6358.87, 2363.16) * mm});
            skLineSegment(sketch, "E5.9.0.3", {"start": v(6358.87, 2363.16) * mm, "end": v(6409.67, 2363.16) * mm});
            skLineSegment(sketch, "E5.9.1.0", {"start": v(6358.87, 2350.46) * mm, "end": v(6409.67, 2350.46) * mm});
            skLineSegment(sketch, "E5.9.1.1", {"start": v(6409.67, 2350.46) * mm, "end": v(6409.67, 2299.66) * mm});
            skLineSegment(sketch, "E5.9.1.2", {"start": v(6358.87, 2350.46) * mm, "end": v(6358.87, 2299.66) * mm});
            skLineSegment(sketch, "E5.9.1.3", {"start": v(6358.87, 2299.66) * mm, "end": v(6409.67, 2299.66) * mm});
            skLineSegment(sketch, "E5.9.2.0", {"start": v(6358.87, 2286.96) * mm, "end": v(6409.67, 2286.96) * mm});
            skLineSegment(sketch, "E5.9.2.1", {"start": v(6409.67, 2286.96) * mm, "end": v(6409.67, 2236.16) * mm});
            skLineSegment(sketch, "E5.9.2.2", {"start": v(6358.87, 2286.96) * mm, "end": v(6358.87, 2236.16) * mm});
            skLineSegment(sketch, "E5.9.2.3", {"start": v(6358.87, 2236.16) * mm, "end": v(6409.67, 2236.16) * mm});
            skLineSegment(sketch, "E5.9.3.0", {"start": v(6358.87, 2223.46) * mm, "end": v(6409.67, 2223.46) * mm});
            skLineSegment(sketch, "E5.9.3.1", {"start": v(6409.67, 2223.46) * mm, "end": v(6409.67, 2172.66) * mm});
            skLineSegment(sketch, "E5.9.3.2", {"start": v(6358.87, 2223.46) * mm, "end": v(6358.87, 2172.66) * mm});
            skLineSegment(sketch, "E5.9.3.3", {"start": v(6358.87, 2172.66) * mm, "end": v(6409.67, 2172.66) * mm});
            skLineSegment(sketch, "E5.9.4.0", {"start": v(6358.87, 2159.96) * mm, "end": v(6409.67, 2159.96) * mm});
            skLineSegment(sketch, "E5.9.4.1", {"start": v(6409.67, 2159.96) * mm, "end": v(6409.67, 2109.16) * mm});
            skLineSegment(sketch, "E5.9.4.2", {"start": v(6358.87, 2159.96) * mm, "end": v(6358.87, 2109.16) * mm});
            skLineSegment(sketch, "E5.9.4.3", {"start": v(6358.87, 2109.16) * mm, "end": v(6409.67, 2109.16) * mm});
            skLineSegment(sketch, "E5.9.5.0", {"start": v(6358.87, 2096.46) * mm, "end": v(6409.67, 2096.46) * mm});
            skLineSegment(sketch, "E5.9.5.1", {"start": v(6409.67, 2096.46) * mm, "end": v(6409.67, 2045.66) * mm});
            skLineSegment(sketch, "E5.9.5.2", {"start": v(6358.87, 2096.46) * mm, "end": v(6358.87, 2045.66) * mm});
            skLineSegment(sketch, "E5.9.5.3", {"start": v(6358.87, 2045.66) * mm, "end": v(6409.67, 2045.66) * mm});
            skLineSegment(sketch, "E5.9.6.0", {"start": v(6358.87, 2032.96) * mm, "end": v(6409.67, 2032.96) * mm});
            skLineSegment(sketch, "E5.9.6.1", {"start": v(6409.67, 2032.96) * mm, "end": v(6409.67, 1982.16) * mm});
            skLineSegment(sketch, "E5.9.6.2", {"start": v(6358.87, 2032.96) * mm, "end": v(6358.87, 1982.16) * mm});
            skLineSegment(sketch, "E5.9.6.3", {"start": v(6358.87, 1982.16) * mm, "end": v(6409.67, 1982.16) * mm});
            skLineSegment(sketch, "E5.9.7.0", {"start": v(6358.87, 1969.46) * mm, "end": v(6409.67, 1969.46) * mm});
            skLineSegment(sketch, "E5.9.7.1", {"start": v(6409.67, 1969.46) * mm, "end": v(6409.67, 1918.66) * mm});
            skLineSegment(sketch, "E5.9.7.2", {"start": v(6358.87, 1969.46) * mm, "end": v(6358.87, 1918.66) * mm});
            skLineSegment(sketch, "E5.9.7.3", {"start": v(6358.87, 1918.66) * mm, "end": v(6409.67, 1918.66) * mm});
            skLineSegment(sketch, "E5.9.8.0", {"start": v(6358.87, 1905.96) * mm, "end": v(6409.67, 1905.96) * mm});
            skLineSegment(sketch, "E5.9.8.1", {"start": v(6409.67, 1905.96) * mm, "end": v(6409.67, 1855.16) * mm});
            skLineSegment(sketch, "E5.9.8.2", {"start": v(6358.87, 1905.96) * mm, "end": v(6358.87, 1855.16) * mm});
            skLineSegment(sketch, "E5.9.8.3", {"start": v(6358.87, 1855.16) * mm, "end": v(6409.67, 1855.16) * mm});
            skLineSegment(sketch, "E5.9.9.0", {"start": v(6358.87, 1842.46) * mm, "end": v(6409.67, 1842.46) * mm});
            skLineSegment(sketch, "E5.9.9.1", {"start": v(6409.67, 1842.46) * mm, "end": v(6409.67, 1791.66) * mm});
            skLineSegment(sketch, "E5.9.9.2", {"start": v(6358.87, 1842.46) * mm, "end": v(6358.87, 1791.66) * mm});
            skLineSegment(sketch, "E5.9.9.3", {"start": v(6358.87, 1791.66) * mm, "end": v(6409.67, 1791.66) * mm});
            skLineSegment(sketch, "E5.direction1", {"start": v(5787.37, 2363.16) * mm, "end": v(5850.87, 2363.16) * mm, "construction": true});
            skLineSegment(sketch, "E5.direction2", {"start": v(5787.37, 2363.16) * mm, "end": v(5787.37, 2299.66) * mm, "construction": true});
            skSolve(sketch);
        }
        {
            var Q0;
            Q0 = qSketchRegion(id + "F5", true);
            extrude(context, id + "F6", {"entities" : qUnion([Q0]), "operationType" : NewBodyOperationType.REMOVE, "endBound" : BoundingType.UP_TO_NEXT, "oppositeDirection" : true, "depth" : 25.4 * mm});
        }
        {
            var Q0;
            Q0=makeQuery(id+"F4.boolean.opBoolean","MERGE",FACE,{"derivedFrom":[makeQuery(id+"F3.boolean.opBoolean","MERGE",FACE,{"derivedFrom":[makeQuery(id+"F2.opExtrude","SWEPT_FACE",FACE,{"disambiguationData":[OSD([sQuery(id+"F0.wireOp",EDGE,"E1.top")])]}),makeQuery(id+"F3.opExtrude","SWEPT_FACE",FACE,{"disambiguationData":[OSD([sQuery(id+"F0.wireOp",EDGE,"E2.top")])]})]}),makeQuery(id+"F4.opExtrude","SWEPT_FACE",FACE,{"disambiguationData":[OSD([sQuery(id+"F0.wireOp",EDGE,"E3.top")])]})]});
            var sketch = newSketch(context, id + "F7", { "sketchPlane" : qUnion([Q0])});
            skLineSegment(sketch, "E6.bottom", {"start": v(-6409.67, 1778.96) * mm, "end": v(-6358.87, 1778.96) * mm});
            skLineSegment(sketch, "E6.top", {"start": v(-6409.67, 1728.16) * mm, "end": v(-6358.87, 1728.16) * mm});
            skLineSegment(sketch, "E6.left", {"start": v(-6409.67, 1778.96) * mm, "end": v(-6409.67, 1728.16) * mm});
            skLineSegment(sketch, "E6.right", {"start": v(-6358.87, 1778.96) * mm, "end": v(-6358.87, 1728.16) * mm});
            skLineSegment(sketch, "E7.0.1.0", {"start": v(-6358.87, 1715.46) * mm, "end": v(-6358.87, 1664.66) * mm});
            skLineSegment(sketch, "E7.0.1.1", {"start": v(-6409.67, 1715.46) * mm, "end": v(-6409.67, 1664.66) * mm});
            skLineSegment(sketch, "E7.0.1.2", {"start": v(-6409.67, 1715.46) * mm, "end": v(-6358.87, 1715.46) * mm});
            skLineSegment(sketch, "E7.0.1.3", {"start": v(-6409.67, 1664.66) * mm, "end": v(-6358.87, 1664.66) * mm});
            skLineSegment(sketch, "E7.0.2.0", {"start": v(-6358.87, 1651.96) * mm, "end": v(-6358.87, 1601.16) * mm});
            skLineSegment(sketch, "E7.0.2.1", {"start": v(-6409.67, 1651.96) * mm, "end": v(-6409.67, 1601.16) * mm});
            skLineSegment(sketch, "E7.0.2.2", {"start": v(-6409.67, 1651.96) * mm, "end": v(-6358.87, 1651.96) * mm});
            skLineSegment(sketch, "E7.0.2.3", {"start": v(-6409.67, 1601.16) * mm, "end": v(-6358.87, 1601.16) * mm});
            skLineSegment(sketch, "E7.0.3.0", {"start": v(-6358.87, 1588.46) * mm, "end": v(-6358.87, 1537.66) * mm});
            skLineSegment(sketch, "E7.0.3.1", {"start": v(-6409.67, 1588.46) * mm, "end": v(-6409.67, 1537.66) * mm});
            skLineSegment(sketch, "E7.0.3.2", {"start": v(-6409.67, 1588.46) * mm, "end": v(-6358.87, 1588.46) * mm});
            skLineSegment(sketch, "E7.0.3.3", {"start": v(-6409.67, 1537.66) * mm, "end": v(-6358.87, 1537.66) * mm});
            skLineSegment(sketch, "E7.0.4.0", {"start": v(-6358.87, 1524.96) * mm, "end": v(-6358.87, 1474.16) * mm});
            skLineSegment(sketch, "E7.0.4.1", {"start": v(-6409.67, 1524.96) * mm, "end": v(-6409.67, 1474.16) * mm});
            skLineSegment(sketch, "E7.0.4.2", {"start": v(-6409.67, 1524.96) * mm, "end": v(-6358.87, 1524.96) * mm});
            skLineSegment(sketch, "E7.0.4.3", {"start": v(-6409.67, 1474.16) * mm, "end": v(-6358.87, 1474.16) * mm});
            skLineSegment(sketch, "E7.0.5.0", {"start": v(-6358.87, 1461.46) * mm, "end": v(-6358.87, 1410.66) * mm});
            skLineSegment(sketch, "E7.0.5.1", {"start": v(-6409.67, 1461.46) * mm, "end": v(-6409.67, 1410.66) * mm});
            skLineSegment(sketch, "E7.0.5.2", {"start": v(-6409.67, 1461.46) * mm, "end": v(-6358.87, 1461.46) * mm});
            skLineSegment(sketch, "E7.0.5.3", {"start": v(-6409.67, 1410.66) * mm, "end": v(-6358.87, 1410.66) * mm});
            skLineSegment(sketch, "E7.0.6.0", {"start": v(-6358.87, 1397.96) * mm, "end": v(-6358.87, 1347.16) * mm});
            skLineSegment(sketch, "E7.0.6.1", {"start": v(-6409.67, 1397.96) * mm, "end": v(-6409.67, 1347.16) * mm});
            skLineSegment(sketch, "E7.0.6.2", {"start": v(-6409.67, 1397.96) * mm, "end": v(-6358.87, 1397.96) * mm});
            skLineSegment(sketch, "E7.0.6.3", {"start": v(-6409.67, 1347.16) * mm, "end": v(-6358.87, 1347.16) * mm});
            skLineSegment(sketch, "E7.0.7.0", {"start": v(-6358.87, 1334.46) * mm, "end": v(-6358.87, 1283.66) * mm});
            skLineSegment(sketch, "E7.0.7.1", {"start": v(-6409.67, 1334.46) * mm, "end": v(-6409.67, 1283.66) * mm});
            skLineSegment(sketch, "E7.0.7.2", {"start": v(-6409.67, 1334.46) * mm, "end": v(-6358.87, 1334.46) * mm});
            skLineSegment(sketch, "E7.0.7.3", {"start": v(-6409.67, 1283.66) * mm, "end": v(-6358.87, 1283.66) * mm});
            skLineSegment(sketch, "E7.0.8.0", {"start": v(-6358.87, 1270.96) * mm, "end": v(-6358.87, 1220.16) * mm});
            skLineSegment(sketch, "E7.0.8.1", {"start": v(-6409.67, 1270.96) * mm, "end": v(-6409.67, 1220.16) * mm});
            skLineSegment(sketch, "E7.0.8.2", {"start": v(-6409.67, 1270.96) * mm, "end": v(-6358.87, 1270.96) * mm});
            skLineSegment(sketch, "E7.0.8.3", {"start": v(-6409.67, 1220.16) * mm, "end": v(-6358.87, 1220.16) * mm});
            skLineSegment(sketch, "E7.0.9.0", {"start": v(-6358.87, 1207.46) * mm, "end": v(-6358.87, 1156.66) * mm});
            skLineSegment(sketch, "E7.0.9.1", {"start": v(-6409.67, 1207.46) * mm, "end": v(-6409.67, 1156.66) * mm});
            skLineSegment(sketch, "E7.0.9.2", {"start": v(-6409.67, 1207.46) * mm, "end": v(-6358.87, 1207.46) * mm});
            skLineSegment(sketch, "E7.0.9.3", {"start": v(-6409.67, 1156.66) * mm, "end": v(-6358.87, 1156.66) * mm});
            skLineSegment(sketch, "E7.1.0.0", {"start": v(-6295.37, 1778.96) * mm, "end": v(-6295.37, 1728.16) * mm});
            skLineSegment(sketch, "E7.1.0.1", {"start": v(-6346.17, 1778.96) * mm, "end": v(-6346.17, 1728.16) * mm});
            skLineSegment(sketch, "E7.1.0.2", {"start": v(-6346.17, 1778.96) * mm, "end": v(-6295.37, 1778.96) * mm});
            skLineSegment(sketch, "E7.1.0.3", {"start": v(-6346.17, 1728.16) * mm, "end": v(-6295.37, 1728.16) * mm});
            skLineSegment(sketch, "E7.1.1.0", {"start": v(-6295.37, 1715.46) * mm, "end": v(-6295.37, 1664.66) * mm});
            skLineSegment(sketch, "E7.1.1.1", {"start": v(-6346.17, 1715.46) * mm, "end": v(-6346.17, 1664.66) * mm});
            skLineSegment(sketch, "E7.1.1.2", {"start": v(-6346.17, 1715.46) * mm, "end": v(-6295.37, 1715.46) * mm});
            skLineSegment(sketch, "E7.1.1.3", {"start": v(-6346.17, 1664.66) * mm, "end": v(-6295.37, 1664.66) * mm});
            skLineSegment(sketch, "E7.1.2.0", {"start": v(-6295.37, 1651.96) * mm, "end": v(-6295.37, 1601.16) * mm});
            skLineSegment(sketch, "E7.1.2.1", {"start": v(-6346.17, 1651.96) * mm, "end": v(-6346.17, 1601.16) * mm});
            skLineSegment(sketch, "E7.1.2.2", {"start": v(-6346.17, 1651.96) * mm, "end": v(-6295.37, 1651.96) * mm});
            skLineSegment(sketch, "E7.1.2.3", {"start": v(-6346.17, 1601.16) * mm, "end": v(-6295.37, 1601.16) * mm});
            skLineSegment(sketch, "E7.1.3.0", {"start": v(-6295.37, 1588.46) * mm, "end": v(-6295.37, 1537.66) * mm});
            skLineSegment(sketch, "E7.1.3.1", {"start": v(-6346.17, 1588.46) * mm, "end": v(-6346.17, 1537.66) * mm});
            skLineSegment(sketch, "E7.1.3.2", {"start": v(-6346.17, 1588.46) * mm, "end": v(-6295.37, 1588.46) * mm});
            skLineSegment(sketch, "E7.1.3.3", {"start": v(-6346.17, 1537.66) * mm, "end": v(-6295.37, 1537.66) * mm});
            skLineSegment(sketch, "E7.1.4.0", {"start": v(-6295.37, 1524.96) * mm, "end": v(-6295.37, 1474.16) * mm});
            skLineSegment(sketch, "E7.1.4.1", {"start": v(-6346.17, 1524.96) * mm, "end": v(-6346.17, 1474.16) * mm});
            skLineSegment(sketch, "E7.1.4.2", {"start": v(-6346.17, 1524.96) * mm, "end": v(-6295.37, 1524.96) * mm});
            skLineSegment(sketch, "E7.1.4.3", {"start": v(-6346.17, 1474.16) * mm, "end": v(-6295.37, 1474.16) * mm});
            skLineSegment(sketch, "E7.1.5.0", {"start": v(-6295.37, 1461.46) * mm, "end": v(-6295.37, 1410.66) * mm});
            skLineSegment(sketch, "E7.1.5.1", {"start": v(-6346.17, 1461.46) * mm, "end": v(-6346.17, 1410.66) * mm});
            skLineSegment(sketch, "E7.1.5.2", {"start": v(-6346.17, 1461.46) * mm, "end": v(-6295.37, 1461.46) * mm});
            skLineSegment(sketch, "E7.1.5.3", {"start": v(-6346.17, 1410.66) * mm, "end": v(-6295.37, 1410.66) * mm});
            skLineSegment(sketch, "E7.1.6.0", {"start": v(-6295.37, 1397.96) * mm, "end": v(-6295.37, 1347.16) * mm});
            skLineSegment(sketch, "E7.1.6.1", {"start": v(-6346.17, 1397.96) * mm, "end": v(-6346.17, 1347.16) * mm});
            skLineSegment(sketch, "E7.1.6.2", {"start": v(-6346.17, 1397.96) * mm, "end": v(-6295.37, 1397.96) * mm});
            skLineSegment(sketch, "E7.1.6.3", {"start": v(-6346.17, 1347.16) * mm, "end": v(-6295.37, 1347.16) * mm});
            skLineSegment(sketch, "E7.1.7.0", {"start": v(-6295.37, 1334.46) * mm, "end": v(-6295.37, 1283.66) * mm});
            skLineSegment(sketch, "E7.1.7.1", {"start": v(-6346.17, 1334.46) * mm, "end": v(-6346.17, 1283.66) * mm});
            skLineSegment(sketch, "E7.1.7.2", {"start": v(-6346.17, 1334.46) * mm, "end": v(-6295.37, 1334.46) * mm});
            skLineSegment(sketch, "E7.1.7.3", {"start": v(-6346.17, 1283.66) * mm, "end": v(-6295.37, 1283.66) * mm});
            skLineSegment(sketch, "E7.1.8.0", {"start": v(-6295.37, 1270.96) * mm, "end": v(-6295.37, 1220.16) * mm});
            skLineSegment(sketch, "E7.1.8.1", {"start": v(-6346.17, 1270.96) * mm, "end": v(-6346.17, 1220.16) * mm});
            skLineSegment(sketch, "E7.1.8.2", {"start": v(-6346.17, 1270.96) * mm, "end": v(-6295.37, 1270.96) * mm});
            skLineSegment(sketch, "E7.1.8.3", {"start": v(-6346.17, 1220.16) * mm, "end": v(-6295.37, 1220.16) * mm});
            skLineSegment(sketch, "E7.1.9.0", {"start": v(-6295.37, 1207.46) * mm, "end": v(-6295.37, 1156.66) * mm});
            skLineSegment(sketch, "E7.1.9.1", {"start": v(-6346.17, 1207.46) * mm, "end": v(-6346.17, 1156.66) * mm});
            skLineSegment(sketch, "E7.1.9.2", {"start": v(-6346.17, 1207.46) * mm, "end": v(-6295.37, 1207.46) * mm});
            skLineSegment(sketch, "E7.1.9.3", {"start": v(-6346.17, 1156.66) * mm, "end": v(-6295.37, 1156.66) * mm});
            skLineSegment(sketch, "E7.2.0.0", {"start": v(-6231.87, 1778.96) * mm, "end": v(-6231.87, 1728.16) * mm});
            skLineSegment(sketch, "E7.2.0.1", {"start": v(-6282.67, 1778.96) * mm, "end": v(-6282.67, 1728.16) * mm});
            skLineSegment(sketch, "E7.2.0.2", {"start": v(-6282.67, 1778.96) * mm, "end": v(-6231.87, 1778.96) * mm});
            skLineSegment(sketch, "E7.2.0.3", {"start": v(-6282.67, 1728.16) * mm, "end": v(-6231.87, 1728.16) * mm});
            skLineSegment(sketch, "E7.2.1.0", {"start": v(-6231.87, 1715.46) * mm, "end": v(-6231.87, 1664.66) * mm});
            skLineSegment(sketch, "E7.2.1.1", {"start": v(-6282.67, 1715.46) * mm, "end": v(-6282.67, 1664.66) * mm});
            skLineSegment(sketch, "E7.2.1.2", {"start": v(-6282.67, 1715.46) * mm, "end": v(-6231.87, 1715.46) * mm});
            skLineSegment(sketch, "E7.2.1.3", {"start": v(-6282.67, 1664.66) * mm, "end": v(-6231.87, 1664.66) * mm});
            skLineSegment(sketch, "E7.2.2.0", {"start": v(-6231.87, 1651.96) * mm, "end": v(-6231.87, 1601.16) * mm});
            skLineSegment(sketch, "E7.2.2.1", {"start": v(-6282.67, 1651.96) * mm, "end": v(-6282.67, 1601.16) * mm});
            skLineSegment(sketch, "E7.2.2.2", {"start": v(-6282.67, 1651.96) * mm, "end": v(-6231.87, 1651.96) * mm});
            skLineSegment(sketch, "E7.2.2.3", {"start": v(-6282.67, 1601.16) * mm, "end": v(-6231.87, 1601.16) * mm});
            skLineSegment(sketch, "E7.2.3.0", {"start": v(-6231.87, 1588.46) * mm, "end": v(-6231.87, 1537.66) * mm});
            skLineSegment(sketch, "E7.2.3.1", {"start": v(-6282.67, 1588.46) * mm, "end": v(-6282.67, 1537.66) * mm});
            skLineSegment(sketch, "E7.2.3.2", {"start": v(-6282.67, 1588.46) * mm, "end": v(-6231.87, 1588.46) * mm});
            skLineSegment(sketch, "E7.2.3.3", {"start": v(-6282.67, 1537.66) * mm, "end": v(-6231.87, 1537.66) * mm});
            skLineSegment(sketch, "E7.2.4.0", {"start": v(-6231.87, 1524.96) * mm, "end": v(-6231.87, 1474.16) * mm});
            skLineSegment(sketch, "E7.2.4.1", {"start": v(-6282.67, 1524.96) * mm, "end": v(-6282.67, 1474.16) * mm});
            skLineSegment(sketch, "E7.2.4.2", {"start": v(-6282.67, 1524.96) * mm, "end": v(-6231.87, 1524.96) * mm});
            skLineSegment(sketch, "E7.2.4.3", {"start": v(-6282.67, 1474.16) * mm, "end": v(-6231.87, 1474.16) * mm});
            skLineSegment(sketch, "E7.2.5.0", {"start": v(-6231.87, 1461.46) * mm, "end": v(-6231.87, 1410.66) * mm});
            skLineSegment(sketch, "E7.2.5.1", {"start": v(-6282.67, 1461.46) * mm, "end": v(-6282.67, 1410.66) * mm});
            skLineSegment(sketch, "E7.2.5.2", {"start": v(-6282.67, 1461.46) * mm, "end": v(-6231.87, 1461.46) * mm});
            skLineSegment(sketch, "E7.2.5.3", {"start": v(-6282.67, 1410.66) * mm, "end": v(-6231.87, 1410.66) * mm});
            skLineSegment(sketch, "E7.2.6.0", {"start": v(-6231.87, 1397.96) * mm, "end": v(-6231.87, 1347.16) * mm});
            skLineSegment(sketch, "E7.2.6.1", {"start": v(-6282.67, 1397.96) * mm, "end": v(-6282.67, 1347.16) * mm});
            skLineSegment(sketch, "E7.2.6.2", {"start": v(-6282.67, 1397.96) * mm, "end": v(-6231.87, 1397.96) * mm});
            skLineSegment(sketch, "E7.2.6.3", {"start": v(-6282.67, 1347.16) * mm, "end": v(-6231.87, 1347.16) * mm});
            skLineSegment(sketch, "E7.2.7.0", {"start": v(-6231.87, 1334.46) * mm, "end": v(-6231.87, 1283.66) * mm});
            skLineSegment(sketch, "E7.2.7.1", {"start": v(-6282.67, 1334.46) * mm, "end": v(-6282.67, 1283.66) * mm});
            skLineSegment(sketch, "E7.2.7.2", {"start": v(-6282.67, 1334.46) * mm, "end": v(-6231.87, 1334.46) * mm});
            skLineSegment(sketch, "E7.2.7.3", {"start": v(-6282.67, 1283.66) * mm, "end": v(-6231.87, 1283.66) * mm});
            skLineSegment(sketch, "E7.2.8.0", {"start": v(-6231.87, 1270.96) * mm, "end": v(-6231.87, 1220.16) * mm});
            skLineSegment(sketch, "E7.2.8.1", {"start": v(-6282.67, 1270.96) * mm, "end": v(-6282.67, 1220.16) * mm});
            skLineSegment(sketch, "E7.2.8.2", {"start": v(-6282.67, 1270.96) * mm, "end": v(-6231.87, 1270.96) * mm});
            skLineSegment(sketch, "E7.2.8.3", {"start": v(-6282.67, 1220.16) * mm, "end": v(-6231.87, 1220.16) * mm});
            skLineSegment(sketch, "E7.2.9.0", {"start": v(-6231.87, 1207.46) * mm, "end": v(-6231.87, 1156.66) * mm});
            skLineSegment(sketch, "E7.2.9.1", {"start": v(-6282.67, 1207.46) * mm, "end": v(-6282.67, 1156.66) * mm});
            skLineSegment(sketch, "E7.2.9.2", {"start": v(-6282.67, 1207.46) * mm, "end": v(-6231.87, 1207.46) * mm});
            skLineSegment(sketch, "E7.2.9.3", {"start": v(-6282.67, 1156.66) * mm, "end": v(-6231.87, 1156.66) * mm});
            skLineSegment(sketch, "E7.3.0.0", {"start": v(-6168.37, 1778.96) * mm, "end": v(-6168.37, 1728.16) * mm});
            skLineSegment(sketch, "E7.3.0.1", {"start": v(-6219.17, 1778.96) * mm, "end": v(-6219.17, 1728.16) * mm});
            skLineSegment(sketch, "E7.3.0.2", {"start": v(-6219.17, 1778.96) * mm, "end": v(-6168.37, 1778.96) * mm});
            skLineSegment(sketch, "E7.3.0.3", {"start": v(-6219.17, 1728.16) * mm, "end": v(-6168.37, 1728.16) * mm});
            skLineSegment(sketch, "E7.3.1.0", {"start": v(-6168.37, 1715.46) * mm, "end": v(-6168.37, 1664.66) * mm});
            skLineSegment(sketch, "E7.3.1.1", {"start": v(-6219.17, 1715.46) * mm, "end": v(-6219.17, 1664.66) * mm});
            skLineSegment(sketch, "E7.3.1.2", {"start": v(-6219.17, 1715.46) * mm, "end": v(-6168.37, 1715.46) * mm});
            skLineSegment(sketch, "E7.3.1.3", {"start": v(-6219.17, 1664.66) * mm, "end": v(-6168.37, 1664.66) * mm});
            skLineSegment(sketch, "E7.3.2.0", {"start": v(-6168.37, 1651.96) * mm, "end": v(-6168.37, 1601.16) * mm});
            skLineSegment(sketch, "E7.3.2.1", {"start": v(-6219.17, 1651.96) * mm, "end": v(-6219.17, 1601.16) * mm});
            skLineSegment(sketch, "E7.3.2.2", {"start": v(-6219.17, 1651.96) * mm, "end": v(-6168.37, 1651.96) * mm});
            skLineSegment(sketch, "E7.3.2.3", {"start": v(-6219.17, 1601.16) * mm, "end": v(-6168.37, 1601.16) * mm});
            skLineSegment(sketch, "E7.3.3.0", {"start": v(-6168.37, 1588.46) * mm, "end": v(-6168.37, 1537.66) * mm});
            skLineSegment(sketch, "E7.3.3.1", {"start": v(-6219.17, 1588.46) * mm, "end": v(-6219.17, 1537.66) * mm});
            skLineSegment(sketch, "E7.3.3.2", {"start": v(-6219.17, 1588.46) * mm, "end": v(-6168.37, 1588.46) * mm});
            skLineSegment(sketch, "E7.3.3.3", {"start": v(-6219.17, 1537.66) * mm, "end": v(-6168.37, 1537.66) * mm});
            skLineSegment(sketch, "E7.3.4.0", {"start": v(-6168.37, 1524.96) * mm, "end": v(-6168.37, 1474.16) * mm});
            skLineSegment(sketch, "E7.3.4.1", {"start": v(-6219.17, 1524.96) * mm, "end": v(-6219.17, 1474.16) * mm});
            skLineSegment(sketch, "E7.3.4.2", {"start": v(-6219.17, 1524.96) * mm, "end": v(-6168.37, 1524.96) * mm});
            skLineSegment(sketch, "E7.3.4.3", {"start": v(-6219.17, 1474.16) * mm, "end": v(-6168.37, 1474.16) * mm});
            skLineSegment(sketch, "E7.3.5.0", {"start": v(-6168.37, 1461.46) * mm, "end": v(-6168.37, 1410.66) * mm});
            skLineSegment(sketch, "E7.3.5.1", {"start": v(-6219.17, 1461.46) * mm, "end": v(-6219.17, 1410.66) * mm});
            skLineSegment(sketch, "E7.3.5.2", {"start": v(-6219.17, 1461.46) * mm, "end": v(-6168.37, 1461.46) * mm});
            skLineSegment(sketch, "E7.3.5.3", {"start": v(-6219.17, 1410.66) * mm, "end": v(-6168.37, 1410.66) * mm});
            skLineSegment(sketch, "E7.3.6.0", {"start": v(-6168.37, 1397.96) * mm, "end": v(-6168.37, 1347.16) * mm});
            skLineSegment(sketch, "E7.3.6.1", {"start": v(-6219.17, 1397.96) * mm, "end": v(-6219.17, 1347.16) * mm});
            skLineSegment(sketch, "E7.3.6.2", {"start": v(-6219.17, 1397.96) * mm, "end": v(-6168.37, 1397.96) * mm});
            skLineSegment(sketch, "E7.3.6.3", {"start": v(-6219.17, 1347.16) * mm, "end": v(-6168.37, 1347.16) * mm});
            skLineSegment(sketch, "E7.3.7.0", {"start": v(-6168.37, 1334.46) * mm, "end": v(-6168.37, 1283.66) * mm});
            skLineSegment(sketch, "E7.3.7.1", {"start": v(-6219.17, 1334.46) * mm, "end": v(-6219.17, 1283.66) * mm});
            skLineSegment(sketch, "E7.3.7.2", {"start": v(-6219.17, 1334.46) * mm, "end": v(-6168.37, 1334.46) * mm});
            skLineSegment(sketch, "E7.3.7.3", {"start": v(-6219.17, 1283.66) * mm, "end": v(-6168.37, 1283.66) * mm});
            skLineSegment(sketch, "E7.3.8.0", {"start": v(-6168.37, 1270.96) * mm, "end": v(-6168.37, 1220.16) * mm});
            skLineSegment(sketch, "E7.3.8.1", {"start": v(-6219.17, 1270.96) * mm, "end": v(-6219.17, 1220.16) * mm});
            skLineSegment(sketch, "E7.3.8.2", {"start": v(-6219.17, 1270.96) * mm, "end": v(-6168.37, 1270.96) * mm});
            skLineSegment(sketch, "E7.3.8.3", {"start": v(-6219.17, 1220.16) * mm, "end": v(-6168.37, 1220.16) * mm});
            skLineSegment(sketch, "E7.3.9.0", {"start": v(-6168.37, 1207.46) * mm, "end": v(-6168.37, 1156.66) * mm});
            skLineSegment(sketch, "E7.3.9.1", {"start": v(-6219.17, 1207.46) * mm, "end": v(-6219.17, 1156.66) * mm});
            skLineSegment(sketch, "E7.3.9.2", {"start": v(-6219.17, 1207.46) * mm, "end": v(-6168.37, 1207.46) * mm});
            skLineSegment(sketch, "E7.3.9.3", {"start": v(-6219.17, 1156.66) * mm, "end": v(-6168.37, 1156.66) * mm});
            skLineSegment(sketch, "E7.4.0.0", {"start": v(-6104.87, 1778.96) * mm, "end": v(-6104.87, 1728.16) * mm});
            skLineSegment(sketch, "E7.4.0.1", {"start": v(-6155.67, 1778.96) * mm, "end": v(-6155.67, 1728.16) * mm});
            skLineSegment(sketch, "E7.4.0.2", {"start": v(-6155.67, 1778.96) * mm, "end": v(-6104.87, 1778.96) * mm});
            skLineSegment(sketch, "E7.4.0.3", {"start": v(-6155.67, 1728.16) * mm, "end": v(-6104.87, 1728.16) * mm});
            skLineSegment(sketch, "E7.4.1.0", {"start": v(-6104.87, 1715.46) * mm, "end": v(-6104.87, 1664.66) * mm});
            skLineSegment(sketch, "E7.4.1.1", {"start": v(-6155.67, 1715.46) * mm, "end": v(-6155.67, 1664.66) * mm});
            skLineSegment(sketch, "E7.4.1.2", {"start": v(-6155.67, 1715.46) * mm, "end": v(-6104.87, 1715.46) * mm});
            skLineSegment(sketch, "E7.4.1.3", {"start": v(-6155.67, 1664.66) * mm, "end": v(-6104.87, 1664.66) * mm});
            skLineSegment(sketch, "E7.4.2.0", {"start": v(-6104.87, 1651.96) * mm, "end": v(-6104.87, 1601.16) * mm});
            skLineSegment(sketch, "E7.4.2.1", {"start": v(-6155.67, 1651.96) * mm, "end": v(-6155.67, 1601.16) * mm});
            skLineSegment(sketch, "E7.4.2.2", {"start": v(-6155.67, 1651.96) * mm, "end": v(-6104.87, 1651.96) * mm});
            skLineSegment(sketch, "E7.4.2.3", {"start": v(-6155.67, 1601.16) * mm, "end": v(-6104.87, 1601.16) * mm});
            skLineSegment(sketch, "E7.4.3.0", {"start": v(-6104.87, 1588.46) * mm, "end": v(-6104.87, 1537.66) * mm});
            skLineSegment(sketch, "E7.4.3.1", {"start": v(-6155.67, 1588.46) * mm, "end": v(-6155.67, 1537.66) * mm});
            skLineSegment(sketch, "E7.4.3.2", {"start": v(-6155.67, 1588.46) * mm, "end": v(-6104.87, 1588.46) * mm});
            skLineSegment(sketch, "E7.4.3.3", {"start": v(-6155.67, 1537.66) * mm, "end": v(-6104.87, 1537.66) * mm});
            skLineSegment(sketch, "E7.4.4.0", {"start": v(-6104.87, 1524.96) * mm, "end": v(-6104.87, 1474.16) * mm});
            skLineSegment(sketch, "E7.4.4.1", {"start": v(-6155.67, 1524.96) * mm, "end": v(-6155.67, 1474.16) * mm});
            skLineSegment(sketch, "E7.4.4.2", {"start": v(-6155.67, 1524.96) * mm, "end": v(-6104.87, 1524.96) * mm});
            skLineSegment(sketch, "E7.4.4.3", {"start": v(-6155.67, 1474.16) * mm, "end": v(-6104.87, 1474.16) * mm});
            skLineSegment(sketch, "E7.4.5.0", {"start": v(-6104.87, 1461.46) * mm, "end": v(-6104.87, 1410.66) * mm});
            skLineSegment(sketch, "E7.4.5.1", {"start": v(-6155.67, 1461.46) * mm, "end": v(-6155.67, 1410.66) * mm});
            skLineSegment(sketch, "E7.4.5.2", {"start": v(-6155.67, 1461.46) * mm, "end": v(-6104.87, 1461.46) * mm});
            skLineSegment(sketch, "E7.4.5.3", {"start": v(-6155.67, 1410.66) * mm, "end": v(-6104.87, 1410.66) * mm});
            skLineSegment(sketch, "E7.4.6.0", {"start": v(-6104.87, 1397.96) * mm, "end": v(-6104.87, 1347.16) * mm});
            skLineSegment(sketch, "E7.4.6.1", {"start": v(-6155.67, 1397.96) * mm, "end": v(-6155.67, 1347.16) * mm});
            skLineSegment(sketch, "E7.4.6.2", {"start": v(-6155.67, 1397.96) * mm, "end": v(-6104.87, 1397.96) * mm});
            skLineSegment(sketch, "E7.4.6.3", {"start": v(-6155.67, 1347.16) * mm, "end": v(-6104.87, 1347.16) * mm});
            skLineSegment(sketch, "E7.4.7.0", {"start": v(-6104.87, 1334.46) * mm, "end": v(-6104.87, 1283.66) * mm});
            skLineSegment(sketch, "E7.4.7.1", {"start": v(-6155.67, 1334.46) * mm, "end": v(-6155.67, 1283.66) * mm});
            skLineSegment(sketch, "E7.4.7.2", {"start": v(-6155.67, 1334.46) * mm, "end": v(-6104.87, 1334.46) * mm});
            skLineSegment(sketch, "E7.4.7.3", {"start": v(-6155.67, 1283.66) * mm, "end": v(-6104.87, 1283.66) * mm});
            skLineSegment(sketch, "E7.4.8.0", {"start": v(-6104.87, 1270.96) * mm, "end": v(-6104.87, 1220.16) * mm});
            skLineSegment(sketch, "E7.4.8.1", {"start": v(-6155.67, 1270.96) * mm, "end": v(-6155.67, 1220.16) * mm});
            skLineSegment(sketch, "E7.4.8.2", {"start": v(-6155.67, 1270.96) * mm, "end": v(-6104.87, 1270.96) * mm});
            skLineSegment(sketch, "E7.4.8.3", {"start": v(-6155.67, 1220.16) * mm, "end": v(-6104.87, 1220.16) * mm});
            skLineSegment(sketch, "E7.4.9.0", {"start": v(-6104.87, 1207.46) * mm, "end": v(-6104.87, 1156.66) * mm});
            skLineSegment(sketch, "E7.4.9.1", {"start": v(-6155.67, 1207.46) * mm, "end": v(-6155.67, 1156.66) * mm});
            skLineSegment(sketch, "E7.4.9.2", {"start": v(-6155.67, 1207.46) * mm, "end": v(-6104.87, 1207.46) * mm});
            skLineSegment(sketch, "E7.4.9.3", {"start": v(-6155.67, 1156.66) * mm, "end": v(-6104.87, 1156.66) * mm});
            skLineSegment(sketch, "E7.5.0.0", {"start": v(-6041.37, 1778.96) * mm, "end": v(-6041.37, 1728.16) * mm});
            skLineSegment(sketch, "E7.5.0.1", {"start": v(-6092.17, 1778.96) * mm, "end": v(-6092.17, 1728.16) * mm});
            skLineSegment(sketch, "E7.5.0.2", {"start": v(-6092.17, 1778.96) * mm, "end": v(-6041.37, 1778.96) * mm});
            skLineSegment(sketch, "E7.5.0.3", {"start": v(-6092.17, 1728.16) * mm, "end": v(-6041.37, 1728.16) * mm});
            skLineSegment(sketch, "E7.5.1.0", {"start": v(-6041.37, 1715.46) * mm, "end": v(-6041.37, 1664.66) * mm});
            skLineSegment(sketch, "E7.5.1.1", {"start": v(-6092.17, 1715.46) * mm, "end": v(-6092.17, 1664.66) * mm});
            skLineSegment(sketch, "E7.5.1.2", {"start": v(-6092.17, 1715.46) * mm, "end": v(-6041.37, 1715.46) * mm});
            skLineSegment(sketch, "E7.5.1.3", {"start": v(-6092.17, 1664.66) * mm, "end": v(-6041.37, 1664.66) * mm});
            skLineSegment(sketch, "E7.5.2.0", {"start": v(-6041.37, 1651.96) * mm, "end": v(-6041.37, 1601.16) * mm});
            skLineSegment(sketch, "E7.5.2.1", {"start": v(-6092.17, 1651.96) * mm, "end": v(-6092.17, 1601.16) * mm});
            skLineSegment(sketch, "E7.5.2.2", {"start": v(-6092.17, 1651.96) * mm, "end": v(-6041.37, 1651.96) * mm});
            skLineSegment(sketch, "E7.5.2.3", {"start": v(-6092.17, 1601.16) * mm, "end": v(-6041.37, 1601.16) * mm});
            skLineSegment(sketch, "E7.5.3.0", {"start": v(-6041.37, 1588.46) * mm, "end": v(-6041.37, 1537.66) * mm});
            skLineSegment(sketch, "E7.5.3.1", {"start": v(-6092.17, 1588.46) * mm, "end": v(-6092.17, 1537.66) * mm});
            skLineSegment(sketch, "E7.5.3.2", {"start": v(-6092.17, 1588.46) * mm, "end": v(-6041.37, 1588.46) * mm});
            skLineSegment(sketch, "E7.5.3.3", {"start": v(-6092.17, 1537.66) * mm, "end": v(-6041.37, 1537.66) * mm});
            skLineSegment(sketch, "E7.5.4.0", {"start": v(-6041.37, 1524.96) * mm, "end": v(-6041.37, 1474.16) * mm});
            skLineSegment(sketch, "E7.5.4.1", {"start": v(-6092.17, 1524.96) * mm, "end": v(-6092.17, 1474.16) * mm});
            skLineSegment(sketch, "E7.5.4.2", {"start": v(-6092.17, 1524.96) * mm, "end": v(-6041.37, 1524.96) * mm});
            skLineSegment(sketch, "E7.5.4.3", {"start": v(-6092.17, 1474.16) * mm, "end": v(-6041.37, 1474.16) * mm});
            skLineSegment(sketch, "E7.5.5.0", {"start": v(-6041.37, 1461.46) * mm, "end": v(-6041.37, 1410.66) * mm});
            skLineSegment(sketch, "E7.5.5.1", {"start": v(-6092.17, 1461.46) * mm, "end": v(-6092.17, 1410.66) * mm});
            skLineSegment(sketch, "E7.5.5.2", {"start": v(-6092.17, 1461.46) * mm, "end": v(-6041.37, 1461.46) * mm});
            skLineSegment(sketch, "E7.5.5.3", {"start": v(-6092.17, 1410.66) * mm, "end": v(-6041.37, 1410.66) * mm});
            skLineSegment(sketch, "E7.5.6.0", {"start": v(-6041.37, 1397.96) * mm, "end": v(-6041.37, 1347.16) * mm});
            skLineSegment(sketch, "E7.5.6.1", {"start": v(-6092.17, 1397.96) * mm, "end": v(-6092.17, 1347.16) * mm});
            skLineSegment(sketch, "E7.5.6.2", {"start": v(-6092.17, 1397.96) * mm, "end": v(-6041.37, 1397.96) * mm});
            skLineSegment(sketch, "E7.5.6.3", {"start": v(-6092.17, 1347.16) * mm, "end": v(-6041.37, 1347.16) * mm});
            skLineSegment(sketch, "E7.5.7.0", {"start": v(-6041.37, 1334.46) * mm, "end": v(-6041.37, 1283.66) * mm});
            skLineSegment(sketch, "E7.5.7.1", {"start": v(-6092.17, 1334.46) * mm, "end": v(-6092.17, 1283.66) * mm});
            skLineSegment(sketch, "E7.5.7.2", {"start": v(-6092.17, 1334.46) * mm, "end": v(-6041.37, 1334.46) * mm});
            skLineSegment(sketch, "E7.5.7.3", {"start": v(-6092.17, 1283.66) * mm, "end": v(-6041.37, 1283.66) * mm});
            skLineSegment(sketch, "E7.5.8.0", {"start": v(-6041.37, 1270.96) * mm, "end": v(-6041.37, 1220.16) * mm});
            skLineSegment(sketch, "E7.5.8.1", {"start": v(-6092.17, 1270.96) * mm, "end": v(-6092.17, 1220.16) * mm});
            skLineSegment(sketch, "E7.5.8.2", {"start": v(-6092.17, 1270.96) * mm, "end": v(-6041.37, 1270.96) * mm});
            skLineSegment(sketch, "E7.5.8.3", {"start": v(-6092.17, 1220.16) * mm, "end": v(-6041.37, 1220.16) * mm});
            skLineSegment(sketch, "E7.5.9.0", {"start": v(-6041.37, 1207.46) * mm, "end": v(-6041.37, 1156.66) * mm});
            skLineSegment(sketch, "E7.5.9.1", {"start": v(-6092.17, 1207.46) * mm, "end": v(-6092.17, 1156.66) * mm});
            skLineSegment(sketch, "E7.5.9.2", {"start": v(-6092.17, 1207.46) * mm, "end": v(-6041.37, 1207.46) * mm});
            skLineSegment(sketch, "E7.5.9.3", {"start": v(-6092.17, 1156.66) * mm, "end": v(-6041.37, 1156.66) * mm});
            skLineSegment(sketch, "E7.6.0.0", {"start": v(-5977.87, 1778.96) * mm, "end": v(-5977.87, 1728.16) * mm});
            skLineSegment(sketch, "E7.6.0.1", {"start": v(-6028.67, 1778.96) * mm, "end": v(-6028.67, 1728.16) * mm});
            skLineSegment(sketch, "E7.6.0.2", {"start": v(-6028.67, 1778.96) * mm, "end": v(-5977.87, 1778.96) * mm});
            skLineSegment(sketch, "E7.6.0.3", {"start": v(-6028.67, 1728.16) * mm, "end": v(-5977.87, 1728.16) * mm});
            skLineSegment(sketch, "E7.6.1.0", {"start": v(-5977.87, 1715.46) * mm, "end": v(-5977.87, 1664.66) * mm});
            skLineSegment(sketch, "E7.6.1.1", {"start": v(-6028.67, 1715.46) * mm, "end": v(-6028.67, 1664.66) * mm});
            skLineSegment(sketch, "E7.6.1.2", {"start": v(-6028.67, 1715.46) * mm, "end": v(-5977.87, 1715.46) * mm});
            skLineSegment(sketch, "E7.6.1.3", {"start": v(-6028.67, 1664.66) * mm, "end": v(-5977.87, 1664.66) * mm});
            skLineSegment(sketch, "E7.6.2.0", {"start": v(-5977.87, 1651.96) * mm, "end": v(-5977.87, 1601.16) * mm});
            skLineSegment(sketch, "E7.6.2.1", {"start": v(-6028.67, 1651.96) * mm, "end": v(-6028.67, 1601.16) * mm});
            skLineSegment(sketch, "E7.6.2.2", {"start": v(-6028.67, 1651.96) * mm, "end": v(-5977.87, 1651.96) * mm});
            skLineSegment(sketch, "E7.6.2.3", {"start": v(-6028.67, 1601.16) * mm, "end": v(-5977.87, 1601.16) * mm});
            skLineSegment(sketch, "E7.6.3.0", {"start": v(-5977.87, 1588.46) * mm, "end": v(-5977.87, 1537.66) * mm});
            skLineSegment(sketch, "E7.6.3.1", {"start": v(-6028.67, 1588.46) * mm, "end": v(-6028.67, 1537.66) * mm});
            skLineSegment(sketch, "E7.6.3.2", {"start": v(-6028.67, 1588.46) * mm, "end": v(-5977.87, 1588.46) * mm});
            skLineSegment(sketch, "E7.6.3.3", {"start": v(-6028.67, 1537.66) * mm, "end": v(-5977.87, 1537.66) * mm});
            skLineSegment(sketch, "E7.6.4.0", {"start": v(-5977.87, 1524.96) * mm, "end": v(-5977.87, 1474.16) * mm});
            skLineSegment(sketch, "E7.6.4.1", {"start": v(-6028.67, 1524.96) * mm, "end": v(-6028.67, 1474.16) * mm});
            skLineSegment(sketch, "E7.6.4.2", {"start": v(-6028.67, 1524.96) * mm, "end": v(-5977.87, 1524.96) * mm});
            skLineSegment(sketch, "E7.6.4.3", {"start": v(-6028.67, 1474.16) * mm, "end": v(-5977.87, 1474.16) * mm});
            skLineSegment(sketch, "E7.6.5.0", {"start": v(-5977.87, 1461.46) * mm, "end": v(-5977.87, 1410.66) * mm});
            skLineSegment(sketch, "E7.6.5.1", {"start": v(-6028.67, 1461.46) * mm, "end": v(-6028.67, 1410.66) * mm});
            skLineSegment(sketch, "E7.6.5.2", {"start": v(-6028.67, 1461.46) * mm, "end": v(-5977.87, 1461.46) * mm});
            skLineSegment(sketch, "E7.6.5.3", {"start": v(-6028.67, 1410.66) * mm, "end": v(-5977.87, 1410.66) * mm});
            skLineSegment(sketch, "E7.6.6.0", {"start": v(-5977.87, 1397.96) * mm, "end": v(-5977.87, 1347.16) * mm});
            skLineSegment(sketch, "E7.6.6.1", {"start": v(-6028.67, 1397.96) * mm, "end": v(-6028.67, 1347.16) * mm});
            skLineSegment(sketch, "E7.6.6.2", {"start": v(-6028.67, 1397.96) * mm, "end": v(-5977.87, 1397.96) * mm});
            skLineSegment(sketch, "E7.6.6.3", {"start": v(-6028.67, 1347.16) * mm, "end": v(-5977.87, 1347.16) * mm});
            skLineSegment(sketch, "E7.6.7.0", {"start": v(-5977.87, 1334.46) * mm, "end": v(-5977.87, 1283.66) * mm});
            skLineSegment(sketch, "E7.6.7.1", {"start": v(-6028.67, 1334.46) * mm, "end": v(-6028.67, 1283.66) * mm});
            skLineSegment(sketch, "E7.6.7.2", {"start": v(-6028.67, 1334.46) * mm, "end": v(-5977.87, 1334.46) * mm});
            skLineSegment(sketch, "E7.6.7.3", {"start": v(-6028.67, 1283.66) * mm, "end": v(-5977.87, 1283.66) * mm});
            skLineSegment(sketch, "E7.6.8.0", {"start": v(-5977.87, 1270.96) * mm, "end": v(-5977.87, 1220.16) * mm});
            skLineSegment(sketch, "E7.6.8.1", {"start": v(-6028.67, 1270.96) * mm, "end": v(-6028.67, 1220.16) * mm});
            skLineSegment(sketch, "E7.6.8.2", {"start": v(-6028.67, 1270.96) * mm, "end": v(-5977.87, 1270.96) * mm});
            skLineSegment(sketch, "E7.6.8.3", {"start": v(-6028.67, 1220.16) * mm, "end": v(-5977.87, 1220.16) * mm});
            skLineSegment(sketch, "E7.6.9.0", {"start": v(-5977.87, 1207.46) * mm, "end": v(-5977.87, 1156.66) * mm});
            skLineSegment(sketch, "E7.6.9.1", {"start": v(-6028.67, 1207.46) * mm, "end": v(-6028.67, 1156.66) * mm});
            skLineSegment(sketch, "E7.6.9.2", {"start": v(-6028.67, 1207.46) * mm, "end": v(-5977.87, 1207.46) * mm});
            skLineSegment(sketch, "E7.6.9.3", {"start": v(-6028.67, 1156.66) * mm, "end": v(-5977.87, 1156.66) * mm});
            skLineSegment(sketch, "E7.7.0.0", {"start": v(-5914.37, 1778.96) * mm, "end": v(-5914.37, 1728.16) * mm});
            skLineSegment(sketch, "E7.7.0.1", {"start": v(-5965.17, 1778.96) * mm, "end": v(-5965.17, 1728.16) * mm});
            skLineSegment(sketch, "E7.7.0.2", {"start": v(-5965.17, 1778.96) * mm, "end": v(-5914.37, 1778.96) * mm});
            skLineSegment(sketch, "E7.7.0.3", {"start": v(-5965.17, 1728.16) * mm, "end": v(-5914.37, 1728.16) * mm});
            skLineSegment(sketch, "E7.7.1.0", {"start": v(-5914.37, 1715.46) * mm, "end": v(-5914.37, 1664.66) * mm});
            skLineSegment(sketch, "E7.7.1.1", {"start": v(-5965.17, 1715.46) * mm, "end": v(-5965.17, 1664.66) * mm});
            skLineSegment(sketch, "E7.7.1.2", {"start": v(-5965.17, 1715.46) * mm, "end": v(-5914.37, 1715.46) * mm});
            skLineSegment(sketch, "E7.7.1.3", {"start": v(-5965.17, 1664.66) * mm, "end": v(-5914.37, 1664.66) * mm});
            skLineSegment(sketch, "E7.7.2.0", {"start": v(-5914.37, 1651.96) * mm, "end": v(-5914.37, 1601.16) * mm});
            skLineSegment(sketch, "E7.7.2.1", {"start": v(-5965.17, 1651.96) * mm, "end": v(-5965.17, 1601.16) * mm});
            skLineSegment(sketch, "E7.7.2.2", {"start": v(-5965.17, 1651.96) * mm, "end": v(-5914.37, 1651.96) * mm});
            skLineSegment(sketch, "E7.7.2.3", {"start": v(-5965.17, 1601.16) * mm, "end": v(-5914.37, 1601.16) * mm});
            skLineSegment(sketch, "E7.7.3.0", {"start": v(-5914.37, 1588.46) * mm, "end": v(-5914.37, 1537.66) * mm});
            skLineSegment(sketch, "E7.7.3.1", {"start": v(-5965.17, 1588.46) * mm, "end": v(-5965.17, 1537.66) * mm});
            skLineSegment(sketch, "E7.7.3.2", {"start": v(-5965.17, 1588.46) * mm, "end": v(-5914.37, 1588.46) * mm});
            skLineSegment(sketch, "E7.7.3.3", {"start": v(-5965.17, 1537.66) * mm, "end": v(-5914.37, 1537.66) * mm});
            skLineSegment(sketch, "E7.7.4.0", {"start": v(-5914.37, 1524.96) * mm, "end": v(-5914.37, 1474.16) * mm});
            skLineSegment(sketch, "E7.7.4.1", {"start": v(-5965.17, 1524.96) * mm, "end": v(-5965.17, 1474.16) * mm});
            skLineSegment(sketch, "E7.7.4.2", {"start": v(-5965.17, 1524.96) * mm, "end": v(-5914.37, 1524.96) * mm});
            skLineSegment(sketch, "E7.7.4.3", {"start": v(-5965.17, 1474.16) * mm, "end": v(-5914.37, 1474.16) * mm});
            skLineSegment(sketch, "E7.7.5.0", {"start": v(-5914.37, 1461.46) * mm, "end": v(-5914.37, 1410.66) * mm});
            skLineSegment(sketch, "E7.7.5.1", {"start": v(-5965.17, 1461.46) * mm, "end": v(-5965.17, 1410.66) * mm});
            skLineSegment(sketch, "E7.7.5.2", {"start": v(-5965.17, 1461.46) * mm, "end": v(-5914.37, 1461.46) * mm});
            skLineSegment(sketch, "E7.7.5.3", {"start": v(-5965.17, 1410.66) * mm, "end": v(-5914.37, 1410.66) * mm});
            skLineSegment(sketch, "E7.7.6.0", {"start": v(-5914.37, 1397.96) * mm, "end": v(-5914.37, 1347.16) * mm});
            skLineSegment(sketch, "E7.7.6.1", {"start": v(-5965.17, 1397.96) * mm, "end": v(-5965.17, 1347.16) * mm});
            skLineSegment(sketch, "E7.7.6.2", {"start": v(-5965.17, 1397.96) * mm, "end": v(-5914.37, 1397.96) * mm});
            skLineSegment(sketch, "E7.7.6.3", {"start": v(-5965.17, 1347.16) * mm, "end": v(-5914.37, 1347.16) * mm});
            skLineSegment(sketch, "E7.7.7.0", {"start": v(-5914.37, 1334.46) * mm, "end": v(-5914.37, 1283.66) * mm});
            skLineSegment(sketch, "E7.7.7.1", {"start": v(-5965.17, 1334.46) * mm, "end": v(-5965.17, 1283.66) * mm});
            skLineSegment(sketch, "E7.7.7.2", {"start": v(-5965.17, 1334.46) * mm, "end": v(-5914.37, 1334.46) * mm});
            skLineSegment(sketch, "E7.7.7.3", {"start": v(-5965.17, 1283.66) * mm, "end": v(-5914.37, 1283.66) * mm});
            skLineSegment(sketch, "E7.7.8.0", {"start": v(-5914.37, 1270.96) * mm, "end": v(-5914.37, 1220.16) * mm});
            skLineSegment(sketch, "E7.7.8.1", {"start": v(-5965.17, 1270.96) * mm, "end": v(-5965.17, 1220.16) * mm});
            skLineSegment(sketch, "E7.7.8.2", {"start": v(-5965.17, 1270.96) * mm, "end": v(-5914.37, 1270.96) * mm});
            skLineSegment(sketch, "E7.7.8.3", {"start": v(-5965.17, 1220.16) * mm, "end": v(-5914.37, 1220.16) * mm});
            skLineSegment(sketch, "E7.7.9.0", {"start": v(-5914.37, 1207.46) * mm, "end": v(-5914.37, 1156.66) * mm});
            skLineSegment(sketch, "E7.7.9.1", {"start": v(-5965.17, 1207.46) * mm, "end": v(-5965.17, 1156.66) * mm});
            skLineSegment(sketch, "E7.7.9.2", {"start": v(-5965.17, 1207.46) * mm, "end": v(-5914.37, 1207.46) * mm});
            skLineSegment(sketch, "E7.7.9.3", {"start": v(-5965.17, 1156.66) * mm, "end": v(-5914.37, 1156.66) * mm});
            skLineSegment(sketch, "E7.8.0.0", {"start": v(-5850.87, 1778.96) * mm, "end": v(-5850.87, 1728.16) * mm});
            skLineSegment(sketch, "E7.8.0.1", {"start": v(-5901.67, 1778.96) * mm, "end": v(-5901.67, 1728.16) * mm});
            skLineSegment(sketch, "E7.8.0.2", {"start": v(-5901.67, 1778.96) * mm, "end": v(-5850.87, 1778.96) * mm});
            skLineSegment(sketch, "E7.8.0.3", {"start": v(-5901.67, 1728.16) * mm, "end": v(-5850.87, 1728.16) * mm});
            skLineSegment(sketch, "E7.8.1.0", {"start": v(-5850.87, 1715.46) * mm, "end": v(-5850.87, 1664.66) * mm});
            skLineSegment(sketch, "E7.8.1.1", {"start": v(-5901.67, 1715.46) * mm, "end": v(-5901.67, 1664.66) * mm});
            skLineSegment(sketch, "E7.8.1.2", {"start": v(-5901.67, 1715.46) * mm, "end": v(-5850.87, 1715.46) * mm});
            skLineSegment(sketch, "E7.8.1.3", {"start": v(-5901.67, 1664.66) * mm, "end": v(-5850.87, 1664.66) * mm});
            skLineSegment(sketch, "E7.8.2.0", {"start": v(-5850.87, 1651.96) * mm, "end": v(-5850.87, 1601.16) * mm});
            skLineSegment(sketch, "E7.8.2.1", {"start": v(-5901.67, 1651.96) * mm, "end": v(-5901.67, 1601.16) * mm});
            skLineSegment(sketch, "E7.8.2.2", {"start": v(-5901.67, 1651.96) * mm, "end": v(-5850.87, 1651.96) * mm});
            skLineSegment(sketch, "E7.8.2.3", {"start": v(-5901.67, 1601.16) * mm, "end": v(-5850.87, 1601.16) * mm});
            skLineSegment(sketch, "E7.8.3.0", {"start": v(-5850.87, 1588.46) * mm, "end": v(-5850.87, 1537.66) * mm});
            skLineSegment(sketch, "E7.8.3.1", {"start": v(-5901.67, 1588.46) * mm, "end": v(-5901.67, 1537.66) * mm});
            skLineSegment(sketch, "E7.8.3.2", {"start": v(-5901.67, 1588.46) * mm, "end": v(-5850.87, 1588.46) * mm});
            skLineSegment(sketch, "E7.8.3.3", {"start": v(-5901.67, 1537.66) * mm, "end": v(-5850.87, 1537.66) * mm});
            skLineSegment(sketch, "E7.8.4.0", {"start": v(-5850.87, 1524.96) * mm, "end": v(-5850.87, 1474.16) * mm});
            skLineSegment(sketch, "E7.8.4.1", {"start": v(-5901.67, 1524.96) * mm, "end": v(-5901.67, 1474.16) * mm});
            skLineSegment(sketch, "E7.8.4.2", {"start": v(-5901.67, 1524.96) * mm, "end": v(-5850.87, 1524.96) * mm});
            skLineSegment(sketch, "E7.8.4.3", {"start": v(-5901.67, 1474.16) * mm, "end": v(-5850.87, 1474.16) * mm});
            skLineSegment(sketch, "E7.8.5.0", {"start": v(-5850.87, 1461.46) * mm, "end": v(-5850.87, 1410.66) * mm});
            skLineSegment(sketch, "E7.8.5.1", {"start": v(-5901.67, 1461.46) * mm, "end": v(-5901.67, 1410.66) * mm});
            skLineSegment(sketch, "E7.8.5.2", {"start": v(-5901.67, 1461.46) * mm, "end": v(-5850.87, 1461.46) * mm});
            skLineSegment(sketch, "E7.8.5.3", {"start": v(-5901.67, 1410.66) * mm, "end": v(-5850.87, 1410.66) * mm});
            skLineSegment(sketch, "E7.8.6.0", {"start": v(-5850.87, 1397.96) * mm, "end": v(-5850.87, 1347.16) * mm});
            skLineSegment(sketch, "E7.8.6.1", {"start": v(-5901.67, 1397.96) * mm, "end": v(-5901.67, 1347.16) * mm});
            skLineSegment(sketch, "E7.8.6.2", {"start": v(-5901.67, 1397.96) * mm, "end": v(-5850.87, 1397.96) * mm});
            skLineSegment(sketch, "E7.8.6.3", {"start": v(-5901.67, 1347.16) * mm, "end": v(-5850.87, 1347.16) * mm});
            skLineSegment(sketch, "E7.8.7.0", {"start": v(-5850.87, 1334.46) * mm, "end": v(-5850.87, 1283.66) * mm});
            skLineSegment(sketch, "E7.8.7.1", {"start": v(-5901.67, 1334.46) * mm, "end": v(-5901.67, 1283.66) * mm});
            skLineSegment(sketch, "E7.8.7.2", {"start": v(-5901.67, 1334.46) * mm, "end": v(-5850.87, 1334.46) * mm});
            skLineSegment(sketch, "E7.8.7.3", {"start": v(-5901.67, 1283.66) * mm, "end": v(-5850.87, 1283.66) * mm});
            skLineSegment(sketch, "E7.8.8.0", {"start": v(-5850.87, 1270.96) * mm, "end": v(-5850.87, 1220.16) * mm});
            skLineSegment(sketch, "E7.8.8.1", {"start": v(-5901.67, 1270.96) * mm, "end": v(-5901.67, 1220.16) * mm});
            skLineSegment(sketch, "E7.8.8.2", {"start": v(-5901.67, 1270.96) * mm, "end": v(-5850.87, 1270.96) * mm});
            skLineSegment(sketch, "E7.8.8.3", {"start": v(-5901.67, 1220.16) * mm, "end": v(-5850.87, 1220.16) * mm});
            skLineSegment(sketch, "E7.8.9.0", {"start": v(-5850.87, 1207.46) * mm, "end": v(-5850.87, 1156.66) * mm});
            skLineSegment(sketch, "E7.8.9.1", {"start": v(-5901.67, 1207.46) * mm, "end": v(-5901.67, 1156.66) * mm});
            skLineSegment(sketch, "E7.8.9.2", {"start": v(-5901.67, 1207.46) * mm, "end": v(-5850.87, 1207.46) * mm});
            skLineSegment(sketch, "E7.8.9.3", {"start": v(-5901.67, 1156.66) * mm, "end": v(-5850.87, 1156.66) * mm});
            skLineSegment(sketch, "E7.9.0.0", {"start": v(-5787.37, 1778.96) * mm, "end": v(-5787.37, 1728.16) * mm});
            skLineSegment(sketch, "E7.9.0.1", {"start": v(-5838.17, 1778.96) * mm, "end": v(-5838.17, 1728.16) * mm});
            skLineSegment(sketch, "E7.9.0.2", {"start": v(-5838.17, 1778.96) * mm, "end": v(-5787.37, 1778.96) * mm});
            skLineSegment(sketch, "E7.9.0.3", {"start": v(-5838.17, 1728.16) * mm, "end": v(-5787.37, 1728.16) * mm});
            skLineSegment(sketch, "E7.9.1.0", {"start": v(-5787.37, 1715.46) * mm, "end": v(-5787.37, 1664.66) * mm});
            skLineSegment(sketch, "E7.9.1.1", {"start": v(-5838.17, 1715.46) * mm, "end": v(-5838.17, 1664.66) * mm});
            skLineSegment(sketch, "E7.9.1.2", {"start": v(-5838.17, 1715.46) * mm, "end": v(-5787.37, 1715.46) * mm});
            skLineSegment(sketch, "E7.9.1.3", {"start": v(-5838.17, 1664.66) * mm, "end": v(-5787.37, 1664.66) * mm});
            skLineSegment(sketch, "E7.9.2.0", {"start": v(-5787.37, 1651.96) * mm, "end": v(-5787.37, 1601.16) * mm});
            skLineSegment(sketch, "E7.9.2.1", {"start": v(-5838.17, 1651.96) * mm, "end": v(-5838.17, 1601.16) * mm});
            skLineSegment(sketch, "E7.9.2.2", {"start": v(-5838.17, 1651.96) * mm, "end": v(-5787.37, 1651.96) * mm});
            skLineSegment(sketch, "E7.9.2.3", {"start": v(-5838.17, 1601.16) * mm, "end": v(-5787.37, 1601.16) * mm});
            skLineSegment(sketch, "E7.9.3.0", {"start": v(-5787.37, 1588.46) * mm, "end": v(-5787.37, 1537.66) * mm});
            skLineSegment(sketch, "E7.9.3.1", {"start": v(-5838.17, 1588.46) * mm, "end": v(-5838.17, 1537.66) * mm});
            skLineSegment(sketch, "E7.9.3.2", {"start": v(-5838.17, 1588.46) * mm, "end": v(-5787.37, 1588.46) * mm});
            skLineSegment(sketch, "E7.9.3.3", {"start": v(-5838.17, 1537.66) * mm, "end": v(-5787.37, 1537.66) * mm});
            skLineSegment(sketch, "E7.9.4.0", {"start": v(-5787.37, 1524.96) * mm, "end": v(-5787.37, 1474.16) * mm});
            skLineSegment(sketch, "E7.9.4.1", {"start": v(-5838.17, 1524.96) * mm, "end": v(-5838.17, 1474.16) * mm});
            skLineSegment(sketch, "E7.9.4.2", {"start": v(-5838.17, 1524.96) * mm, "end": v(-5787.37, 1524.96) * mm});
            skLineSegment(sketch, "E7.9.4.3", {"start": v(-5838.17, 1474.16) * mm, "end": v(-5787.37, 1474.16) * mm});
            skLineSegment(sketch, "E7.9.5.0", {"start": v(-5787.37, 1461.46) * mm, "end": v(-5787.37, 1410.66) * mm});
            skLineSegment(sketch, "E7.9.5.1", {"start": v(-5838.17, 1461.46) * mm, "end": v(-5838.17, 1410.66) * mm});
            skLineSegment(sketch, "E7.9.5.2", {"start": v(-5838.17, 1461.46) * mm, "end": v(-5787.37, 1461.46) * mm});
            skLineSegment(sketch, "E7.9.5.3", {"start": v(-5838.17, 1410.66) * mm, "end": v(-5787.37, 1410.66) * mm});
            skLineSegment(sketch, "E7.9.6.0", {"start": v(-5787.37, 1397.96) * mm, "end": v(-5787.37, 1347.16) * mm});
            skLineSegment(sketch, "E7.9.6.1", {"start": v(-5838.17, 1397.96) * mm, "end": v(-5838.17, 1347.16) * mm});
            skLineSegment(sketch, "E7.9.6.2", {"start": v(-5838.17, 1397.96) * mm, "end": v(-5787.37, 1397.96) * mm});
            skLineSegment(sketch, "E7.9.6.3", {"start": v(-5838.17, 1347.16) * mm, "end": v(-5787.37, 1347.16) * mm});
            skLineSegment(sketch, "E7.9.7.0", {"start": v(-5787.37, 1334.46) * mm, "end": v(-5787.37, 1283.66) * mm});
            skLineSegment(sketch, "E7.9.7.1", {"start": v(-5838.17, 1334.46) * mm, "end": v(-5838.17, 1283.66) * mm});
            skLineSegment(sketch, "E7.9.7.2", {"start": v(-5838.17, 1334.46) * mm, "end": v(-5787.37, 1334.46) * mm});
            skLineSegment(sketch, "E7.9.7.3", {"start": v(-5838.17, 1283.66) * mm, "end": v(-5787.37, 1283.66) * mm});
            skLineSegment(sketch, "E7.9.8.0", {"start": v(-5787.37, 1270.96) * mm, "end": v(-5787.37, 1220.16) * mm});
            skLineSegment(sketch, "E7.9.8.1", {"start": v(-5838.17, 1270.96) * mm, "end": v(-5838.17, 1220.16) * mm});
            skLineSegment(sketch, "E7.9.8.2", {"start": v(-5838.17, 1270.96) * mm, "end": v(-5787.37, 1270.96) * mm});
            skLineSegment(sketch, "E7.9.8.3", {"start": v(-5838.17, 1220.16) * mm, "end": v(-5787.37, 1220.16) * mm});
            skLineSegment(sketch, "E7.9.9.0", {"start": v(-5787.37, 1207.46) * mm, "end": v(-5787.37, 1156.66) * mm});
            skLineSegment(sketch, "E7.9.9.1", {"start": v(-5838.17, 1207.46) * mm, "end": v(-5838.17, 1156.66) * mm});
            skLineSegment(sketch, "E7.9.9.2", {"start": v(-5838.17, 1207.46) * mm, "end": v(-5787.37, 1207.46) * mm});
            skLineSegment(sketch, "E7.9.9.3", {"start": v(-5838.17, 1156.66) * mm, "end": v(-5787.37, 1156.66) * mm});
            skLineSegment(sketch, "E7.direction1", {"start": v(-6409.67, 1728.16) * mm, "end": v(-6346.17, 1728.16) * mm, "construction": true});
            skLineSegment(sketch, "E7.direction2", {"start": v(-6409.67, 1728.16) * mm, "end": v(-6409.67, 1664.66) * mm, "construction": true});
            skSolve(sketch);
        }
        {
            var Q0;
            Q0 = qSketchRegion(id + "F7", true);
            extrude(context, id + "F8", {"entities" : qUnion([Q0]), "operationType" : NewBodyOperationType.REMOVE, "endBound" : BoundingType.UP_TO_NEXT, "oppositeDirection" : true, "depth" : 25.4 * mm});
        }
        {
            var Q0;
            Q0=makeQuery(id+"F4.boolean.opBoolean","MERGE",FACE,{"derivedFrom":[makeQuery(id+"F3.boolean.opBoolean","MERGE",FACE,{"derivedFrom":[makeQuery(id+"F2.opExtrude","SWEPT_FACE",FACE,{"disambiguationData":[OSD([sQuery(id+"F0.wireOp",EDGE,"E1.bottom")])]}),makeQuery(id+"F3.opExtrude","SWEPT_FACE",FACE,{"disambiguationData":[OSD([sQuery(id+"F0.wireOp",EDGE,"E2.bottom")])]})]}),makeQuery(id+"F4.opExtrude","SWEPT_FACE",FACE,{"disambiguationData":[OSD([sQuery(id+"F0.wireOp",EDGE,"E3.bottom")])]})]});
            var sketch = newSketch(context, id + "F9", { "sketchPlane" : qUnion([Q0])});
            skLineSegment(sketch, "E8.bottom", {"start": v(5787.37, 1143.96) * mm, "end": v(5838.17, 1143.96) * mm});
            skLineSegment(sketch, "E8.top", {"start": v(5787.37, 1093.16) * mm, "end": v(5838.17, 1093.16) * mm});
            skLineSegment(sketch, "E8.left", {"start": v(5787.37, 1143.96) * mm, "end": v(5787.37, 1093.16) * mm});
            skLineSegment(sketch, "E8.right", {"start": v(5838.17, 1143.96) * mm, "end": v(5838.17, 1093.16) * mm});
            skLineSegment(sketch, "E9.0.1.0", {"start": v(5787.37, 1080.46) * mm, "end": v(5838.17, 1080.46) * mm});
            skLineSegment(sketch, "E9.0.1.1", {"start": v(5787.37, 1080.46) * mm, "end": v(5787.37, 1029.66) * mm});
            skLineSegment(sketch, "E9.0.1.2", {"start": v(5787.37, 1029.66) * mm, "end": v(5838.17, 1029.66) * mm});
            skLineSegment(sketch, "E9.0.1.3", {"start": v(5838.17, 1080.46) * mm, "end": v(5838.17, 1029.66) * mm});
            skLineSegment(sketch, "E9.0.2.0", {"start": v(5787.37, 1016.96) * mm, "end": v(5838.17, 1016.96) * mm});
            skLineSegment(sketch, "E9.0.2.1", {"start": v(5787.37, 1016.96) * mm, "end": v(5787.37, 966.16) * mm});
            skLineSegment(sketch, "E9.0.2.2", {"start": v(5787.37, 966.16) * mm, "end": v(5838.17, 966.16) * mm});
            skLineSegment(sketch, "E9.0.2.3", {"start": v(5838.17, 1016.96) * mm, "end": v(5838.17, 966.16) * mm});
            skLineSegment(sketch, "E9.0.3.0", {"start": v(5787.37, 953.46) * mm, "end": v(5838.17, 953.46) * mm});
            skLineSegment(sketch, "E9.0.3.1", {"start": v(5787.37, 953.46) * mm, "end": v(5787.37, 902.66) * mm});
            skLineSegment(sketch, "E9.0.3.2", {"start": v(5787.37, 902.66) * mm, "end": v(5838.17, 902.66) * mm});
            skLineSegment(sketch, "E9.0.3.3", {"start": v(5838.17, 953.46) * mm, "end": v(5838.17, 902.66) * mm});
            skLineSegment(sketch, "E9.0.4.0", {"start": v(5787.37, 889.96) * mm, "end": v(5838.17, 889.96) * mm});
            skLineSegment(sketch, "E9.0.4.1", {"start": v(5787.37, 889.96) * mm, "end": v(5787.37, 839.16) * mm});
            skLineSegment(sketch, "E9.0.4.2", {"start": v(5787.37, 839.16) * mm, "end": v(5838.17, 839.16) * mm});
            skLineSegment(sketch, "E9.0.4.3", {"start": v(5838.17, 889.96) * mm, "end": v(5838.17, 839.16) * mm});
            skLineSegment(sketch, "E9.0.5.0", {"start": v(5787.37, 826.46) * mm, "end": v(5838.17, 826.46) * mm});
            skLineSegment(sketch, "E9.0.5.1", {"start": v(5787.37, 826.46) * mm, "end": v(5787.37, 775.66) * mm});
            skLineSegment(sketch, "E9.0.5.2", {"start": v(5787.37, 775.66) * mm, "end": v(5838.17, 775.66) * mm});
            skLineSegment(sketch, "E9.0.5.3", {"start": v(5838.17, 826.46) * mm, "end": v(5838.17, 775.66) * mm});
            skLineSegment(sketch, "E9.0.6.0", {"start": v(5787.37, 762.96) * mm, "end": v(5838.17, 762.96) * mm});
            skLineSegment(sketch, "E9.0.6.1", {"start": v(5787.37, 762.96) * mm, "end": v(5787.37, 712.16) * mm});
            skLineSegment(sketch, "E9.0.6.2", {"start": v(5787.37, 712.16) * mm, "end": v(5838.17, 712.16) * mm});
            skLineSegment(sketch, "E9.0.6.3", {"start": v(5838.17, 762.96) * mm, "end": v(5838.17, 712.16) * mm});
            skLineSegment(sketch, "E9.0.7.0", {"start": v(5787.37, 699.46) * mm, "end": v(5838.17, 699.46) * mm});
            skLineSegment(sketch, "E9.0.7.1", {"start": v(5787.37, 699.46) * mm, "end": v(5787.37, 648.66) * mm});
            skLineSegment(sketch, "E9.0.7.2", {"start": v(5787.37, 648.66) * mm, "end": v(5838.17, 648.66) * mm});
            skLineSegment(sketch, "E9.0.7.3", {"start": v(5838.17, 699.46) * mm, "end": v(5838.17, 648.66) * mm});
            skLineSegment(sketch, "E9.0.8.0", {"start": v(5787.37, 635.96) * mm, "end": v(5838.17, 635.96) * mm});
            skLineSegment(sketch, "E9.0.8.1", {"start": v(5787.37, 635.96) * mm, "end": v(5787.37, 585.16) * mm});
            skLineSegment(sketch, "E9.0.8.2", {"start": v(5787.37, 585.16) * mm, "end": v(5838.17, 585.16) * mm});
            skLineSegment(sketch, "E9.0.8.3", {"start": v(5838.17, 635.96) * mm, "end": v(5838.17, 585.16) * mm});
            skLineSegment(sketch, "E9.0.9.0", {"start": v(5787.37, 572.46) * mm, "end": v(5838.17, 572.46) * mm});
            skLineSegment(sketch, "E9.0.9.1", {"start": v(5787.37, 572.46) * mm, "end": v(5787.37, 521.66) * mm});
            skLineSegment(sketch, "E9.0.9.2", {"start": v(5787.37, 521.66) * mm, "end": v(5838.17, 521.66) * mm});
            skLineSegment(sketch, "E9.0.9.3", {"start": v(5838.17, 572.46) * mm, "end": v(5838.17, 521.66) * mm});
            skLineSegment(sketch, "E9.1.0.0", {"start": v(5850.87, 1143.96) * mm, "end": v(5901.67, 1143.96) * mm});
            skLineSegment(sketch, "E9.1.0.1", {"start": v(5850.87, 1143.96) * mm, "end": v(5850.87, 1093.16) * mm});
            skLineSegment(sketch, "E9.1.0.2", {"start": v(5850.87, 1093.16) * mm, "end": v(5901.67, 1093.16) * mm});
            skLineSegment(sketch, "E9.1.0.3", {"start": v(5901.67, 1143.96) * mm, "end": v(5901.67, 1093.16) * mm});
            skLineSegment(sketch, "E9.1.1.0", {"start": v(5850.87, 1080.46) * mm, "end": v(5901.67, 1080.46) * mm});
            skLineSegment(sketch, "E9.1.1.1", {"start": v(5850.87, 1080.46) * mm, "end": v(5850.87, 1029.66) * mm});
            skLineSegment(sketch, "E9.1.1.2", {"start": v(5850.87, 1029.66) * mm, "end": v(5901.67, 1029.66) * mm});
            skLineSegment(sketch, "E9.1.1.3", {"start": v(5901.67, 1080.46) * mm, "end": v(5901.67, 1029.66) * mm});
            skLineSegment(sketch, "E9.1.2.0", {"start": v(5850.87, 1016.96) * mm, "end": v(5901.67, 1016.96) * mm});
            skLineSegment(sketch, "E9.1.2.1", {"start": v(5850.87, 1016.96) * mm, "end": v(5850.87, 966.16) * mm});
            skLineSegment(sketch, "E9.1.2.2", {"start": v(5850.87, 966.16) * mm, "end": v(5901.67, 966.16) * mm});
            skLineSegment(sketch, "E9.1.2.3", {"start": v(5901.67, 1016.96) * mm, "end": v(5901.67, 966.16) * mm});
            skLineSegment(sketch, "E9.1.3.0", {"start": v(5850.87, 953.46) * mm, "end": v(5901.67, 953.46) * mm});
            skLineSegment(sketch, "E9.1.3.1", {"start": v(5850.87, 953.46) * mm, "end": v(5850.87, 902.66) * mm});
            skLineSegment(sketch, "E9.1.3.2", {"start": v(5850.87, 902.66) * mm, "end": v(5901.67, 902.66) * mm});
            skLineSegment(sketch, "E9.1.3.3", {"start": v(5901.67, 953.46) * mm, "end": v(5901.67, 902.66) * mm});
            skLineSegment(sketch, "E9.1.4.0", {"start": v(5850.87, 889.96) * mm, "end": v(5901.67, 889.96) * mm});
            skLineSegment(sketch, "E9.1.4.1", {"start": v(5850.87, 889.96) * mm, "end": v(5850.87, 839.16) * mm});
            skLineSegment(sketch, "E9.1.4.2", {"start": v(5850.87, 839.16) * mm, "end": v(5901.67, 839.16) * mm});
            skLineSegment(sketch, "E9.1.4.3", {"start": v(5901.67, 889.96) * mm, "end": v(5901.67, 839.16) * mm});
            skLineSegment(sketch, "E9.1.5.0", {"start": v(5850.87, 826.46) * mm, "end": v(5901.67, 826.46) * mm});
            skLineSegment(sketch, "E9.1.5.1", {"start": v(5850.87, 826.46) * mm, "end": v(5850.87, 775.66) * mm});
            skLineSegment(sketch, "E9.1.5.2", {"start": v(5850.87, 775.66) * mm, "end": v(5901.67, 775.66) * mm});
            skLineSegment(sketch, "E9.1.5.3", {"start": v(5901.67, 826.46) * mm, "end": v(5901.67, 775.66) * mm});
            skLineSegment(sketch, "E9.1.6.0", {"start": v(5850.87, 762.96) * mm, "end": v(5901.67, 762.96) * mm});
            skLineSegment(sketch, "E9.1.6.1", {"start": v(5850.87, 762.96) * mm, "end": v(5850.87, 712.16) * mm});
            skLineSegment(sketch, "E9.1.6.2", {"start": v(5850.87, 712.16) * mm, "end": v(5901.67, 712.16) * mm});
            skLineSegment(sketch, "E9.1.6.3", {"start": v(5901.67, 762.96) * mm, "end": v(5901.67, 712.16) * mm});
            skLineSegment(sketch, "E9.1.7.0", {"start": v(5850.87, 699.46) * mm, "end": v(5901.67, 699.46) * mm});
            skLineSegment(sketch, "E9.1.7.1", {"start": v(5850.87, 699.46) * mm, "end": v(5850.87, 648.66) * mm});
            skLineSegment(sketch, "E9.1.7.2", {"start": v(5850.87, 648.66) * mm, "end": v(5901.67, 648.66) * mm});
            skLineSegment(sketch, "E9.1.7.3", {"start": v(5901.67, 699.46) * mm, "end": v(5901.67, 648.66) * mm});
            skLineSegment(sketch, "E9.1.8.0", {"start": v(5850.87, 635.96) * mm, "end": v(5901.67, 635.96) * mm});
            skLineSegment(sketch, "E9.1.8.1", {"start": v(5850.87, 635.96) * mm, "end": v(5850.87, 585.16) * mm});
            skLineSegment(sketch, "E9.1.8.2", {"start": v(5850.87, 585.16) * mm, "end": v(5901.67, 585.16) * mm});
            skLineSegment(sketch, "E9.1.8.3", {"start": v(5901.67, 635.96) * mm, "end": v(5901.67, 585.16) * mm});
            skLineSegment(sketch, "E9.1.9.0", {"start": v(5850.87, 572.46) * mm, "end": v(5901.67, 572.46) * mm});
            skLineSegment(sketch, "E9.1.9.1", {"start": v(5850.87, 572.46) * mm, "end": v(5850.87, 521.66) * mm});
            skLineSegment(sketch, "E9.1.9.2", {"start": v(5850.87, 521.66) * mm, "end": v(5901.67, 521.66) * mm});
            skLineSegment(sketch, "E9.1.9.3", {"start": v(5901.67, 572.46) * mm, "end": v(5901.67, 521.66) * mm});
            skLineSegment(sketch, "E9.2.0.0", {"start": v(5914.37, 1143.96) * mm, "end": v(5965.17, 1143.96) * mm});
            skLineSegment(sketch, "E9.2.0.1", {"start": v(5914.37, 1143.96) * mm, "end": v(5914.37, 1093.16) * mm});
            skLineSegment(sketch, "E9.2.0.2", {"start": v(5914.37, 1093.16) * mm, "end": v(5965.17, 1093.16) * mm});
            skLineSegment(sketch, "E9.2.0.3", {"start": v(5965.17, 1143.96) * mm, "end": v(5965.17, 1093.16) * mm});
            skLineSegment(sketch, "E9.2.1.0", {"start": v(5914.37, 1080.46) * mm, "end": v(5965.17, 1080.46) * mm});
            skLineSegment(sketch, "E9.2.1.1", {"start": v(5914.37, 1080.46) * mm, "end": v(5914.37, 1029.66) * mm});
            skLineSegment(sketch, "E9.2.1.2", {"start": v(5914.37, 1029.66) * mm, "end": v(5965.17, 1029.66) * mm});
            skLineSegment(sketch, "E9.2.1.3", {"start": v(5965.17, 1080.46) * mm, "end": v(5965.17, 1029.66) * mm});
            skLineSegment(sketch, "E9.2.2.0", {"start": v(5914.37, 1016.96) * mm, "end": v(5965.17, 1016.96) * mm});
            skLineSegment(sketch, "E9.2.2.1", {"start": v(5914.37, 1016.96) * mm, "end": v(5914.37, 966.16) * mm});
            skLineSegment(sketch, "E9.2.2.2", {"start": v(5914.37, 966.16) * mm, "end": v(5965.17, 966.16) * mm});
            skLineSegment(sketch, "E9.2.2.3", {"start": v(5965.17, 1016.96) * mm, "end": v(5965.17, 966.16) * mm});
            skLineSegment(sketch, "E9.2.3.0", {"start": v(5914.37, 953.46) * mm, "end": v(5965.17, 953.46) * mm});
            skLineSegment(sketch, "E9.2.3.1", {"start": v(5914.37, 953.46) * mm, "end": v(5914.37, 902.66) * mm});
            skLineSegment(sketch, "E9.2.3.2", {"start": v(5914.37, 902.66) * mm, "end": v(5965.17, 902.66) * mm});
            skLineSegment(sketch, "E9.2.3.3", {"start": v(5965.17, 953.46) * mm, "end": v(5965.17, 902.66) * mm});
            skLineSegment(sketch, "E9.2.4.0", {"start": v(5914.37, 889.96) * mm, "end": v(5965.17, 889.96) * mm});
            skLineSegment(sketch, "E9.2.4.1", {"start": v(5914.37, 889.96) * mm, "end": v(5914.37, 839.16) * mm});
            skLineSegment(sketch, "E9.2.4.2", {"start": v(5914.37, 839.16) * mm, "end": v(5965.17, 839.16) * mm});
            skLineSegment(sketch, "E9.2.4.3", {"start": v(5965.17, 889.96) * mm, "end": v(5965.17, 839.16) * mm});
            skLineSegment(sketch, "E9.2.5.0", {"start": v(5914.37, 826.46) * mm, "end": v(5965.17, 826.46) * mm});
            skLineSegment(sketch, "E9.2.5.1", {"start": v(5914.37, 826.46) * mm, "end": v(5914.37, 775.66) * mm});
            skLineSegment(sketch, "E9.2.5.2", {"start": v(5914.37, 775.66) * mm, "end": v(5965.17, 775.66) * mm});
            skLineSegment(sketch, "E9.2.5.3", {"start": v(5965.17, 826.46) * mm, "end": v(5965.17, 775.66) * mm});
            skLineSegment(sketch, "E9.2.6.0", {"start": v(5914.37, 762.96) * mm, "end": v(5965.17, 762.96) * mm});
            skLineSegment(sketch, "E9.2.6.1", {"start": v(5914.37, 762.96) * mm, "end": v(5914.37, 712.16) * mm});
            skLineSegment(sketch, "E9.2.6.2", {"start": v(5914.37, 712.16) * mm, "end": v(5965.17, 712.16) * mm});
            skLineSegment(sketch, "E9.2.6.3", {"start": v(5965.17, 762.96) * mm, "end": v(5965.17, 712.16) * mm});
            skLineSegment(sketch, "E9.2.7.0", {"start": v(5914.37, 699.46) * mm, "end": v(5965.17, 699.46) * mm});
            skLineSegment(sketch, "E9.2.7.1", {"start": v(5914.37, 699.46) * mm, "end": v(5914.37, 648.66) * mm});
            skLineSegment(sketch, "E9.2.7.2", {"start": v(5914.37, 648.66) * mm, "end": v(5965.17, 648.66) * mm});
            skLineSegment(sketch, "E9.2.7.3", {"start": v(5965.17, 699.46) * mm, "end": v(5965.17, 648.66) * mm});
            skLineSegment(sketch, "E9.2.8.0", {"start": v(5914.37, 635.96) * mm, "end": v(5965.17, 635.96) * mm});
            skLineSegment(sketch, "E9.2.8.1", {"start": v(5914.37, 635.96) * mm, "end": v(5914.37, 585.16) * mm});
            skLineSegment(sketch, "E9.2.8.2", {"start": v(5914.37, 585.16) * mm, "end": v(5965.17, 585.16) * mm});
            skLineSegment(sketch, "E9.2.8.3", {"start": v(5965.17, 635.96) * mm, "end": v(5965.17, 585.16) * mm});
            skLineSegment(sketch, "E9.2.9.0", {"start": v(5914.37, 572.46) * mm, "end": v(5965.17, 572.46) * mm});
            skLineSegment(sketch, "E9.2.9.1", {"start": v(5914.37, 572.46) * mm, "end": v(5914.37, 521.66) * mm});
            skLineSegment(sketch, "E9.2.9.2", {"start": v(5914.37, 521.66) * mm, "end": v(5965.17, 521.66) * mm});
            skLineSegment(sketch, "E9.2.9.3", {"start": v(5965.17, 572.46) * mm, "end": v(5965.17, 521.66) * mm});
            skLineSegment(sketch, "E9.3.0.0", {"start": v(5977.87, 1143.96) * mm, "end": v(6028.67, 1143.96) * mm});
            skLineSegment(sketch, "E9.3.0.1", {"start": v(5977.87, 1143.96) * mm, "end": v(5977.87, 1093.16) * mm});
            skLineSegment(sketch, "E9.3.0.2", {"start": v(5977.87, 1093.16) * mm, "end": v(6028.67, 1093.16) * mm});
            skLineSegment(sketch, "E9.3.0.3", {"start": v(6028.67, 1143.96) * mm, "end": v(6028.67, 1093.16) * mm});
            skLineSegment(sketch, "E9.3.1.0", {"start": v(5977.87, 1080.46) * mm, "end": v(6028.67, 1080.46) * mm});
            skLineSegment(sketch, "E9.3.1.1", {"start": v(5977.87, 1080.46) * mm, "end": v(5977.87, 1029.66) * mm});
            skLineSegment(sketch, "E9.3.1.2", {"start": v(5977.87, 1029.66) * mm, "end": v(6028.67, 1029.66) * mm});
            skLineSegment(sketch, "E9.3.1.3", {"start": v(6028.67, 1080.46) * mm, "end": v(6028.67, 1029.66) * mm});
            skLineSegment(sketch, "E9.3.2.0", {"start": v(5977.87, 1016.96) * mm, "end": v(6028.67, 1016.96) * mm});
            skLineSegment(sketch, "E9.3.2.1", {"start": v(5977.87, 1016.96) * mm, "end": v(5977.87, 966.16) * mm});
            skLineSegment(sketch, "E9.3.2.2", {"start": v(5977.87, 966.16) * mm, "end": v(6028.67, 966.16) * mm});
            skLineSegment(sketch, "E9.3.2.3", {"start": v(6028.67, 1016.96) * mm, "end": v(6028.67, 966.16) * mm});
            skLineSegment(sketch, "E9.3.3.0", {"start": v(5977.87, 953.46) * mm, "end": v(6028.67, 953.46) * mm});
            skLineSegment(sketch, "E9.3.3.1", {"start": v(5977.87, 953.46) * mm, "end": v(5977.87, 902.66) * mm});
            skLineSegment(sketch, "E9.3.3.2", {"start": v(5977.87, 902.66) * mm, "end": v(6028.67, 902.66) * mm});
            skLineSegment(sketch, "E9.3.3.3", {"start": v(6028.67, 953.46) * mm, "end": v(6028.67, 902.66) * mm});
            skLineSegment(sketch, "E9.3.4.0", {"start": v(5977.87, 889.96) * mm, "end": v(6028.67, 889.96) * mm});
            skLineSegment(sketch, "E9.3.4.1", {"start": v(5977.87, 889.96) * mm, "end": v(5977.87, 839.16) * mm});
            skLineSegment(sketch, "E9.3.4.2", {"start": v(5977.87, 839.16) * mm, "end": v(6028.67, 839.16) * mm});
            skLineSegment(sketch, "E9.3.4.3", {"start": v(6028.67, 889.96) * mm, "end": v(6028.67, 839.16) * mm});
            skLineSegment(sketch, "E9.3.5.0", {"start": v(5977.87, 826.46) * mm, "end": v(6028.67, 826.46) * mm});
            skLineSegment(sketch, "E9.3.5.1", {"start": v(5977.87, 826.46) * mm, "end": v(5977.87, 775.66) * mm});
            skLineSegment(sketch, "E9.3.5.2", {"start": v(5977.87, 775.66) * mm, "end": v(6028.67, 775.66) * mm});
            skLineSegment(sketch, "E9.3.5.3", {"start": v(6028.67, 826.46) * mm, "end": v(6028.67, 775.66) * mm});
            skLineSegment(sketch, "E9.3.6.0", {"start": v(5977.87, 762.96) * mm, "end": v(6028.67, 762.96) * mm});
            skLineSegment(sketch, "E9.3.6.1", {"start": v(5977.87, 762.96) * mm, "end": v(5977.87, 712.16) * mm});
            skLineSegment(sketch, "E9.3.6.2", {"start": v(5977.87, 712.16) * mm, "end": v(6028.67, 712.16) * mm});
            skLineSegment(sketch, "E9.3.6.3", {"start": v(6028.67, 762.96) * mm, "end": v(6028.67, 712.16) * mm});
            skLineSegment(sketch, "E9.3.7.0", {"start": v(5977.87, 699.46) * mm, "end": v(6028.67, 699.46) * mm});
            skLineSegment(sketch, "E9.3.7.1", {"start": v(5977.87, 699.46) * mm, "end": v(5977.87, 648.66) * mm});
            skLineSegment(sketch, "E9.3.7.2", {"start": v(5977.87, 648.66) * mm, "end": v(6028.67, 648.66) * mm});
            skLineSegment(sketch, "E9.3.7.3", {"start": v(6028.67, 699.46) * mm, "end": v(6028.67, 648.66) * mm});
            skLineSegment(sketch, "E9.3.8.0", {"start": v(5977.87, 635.96) * mm, "end": v(6028.67, 635.96) * mm});
            skLineSegment(sketch, "E9.3.8.1", {"start": v(5977.87, 635.96) * mm, "end": v(5977.87, 585.16) * mm});
            skLineSegment(sketch, "E9.3.8.2", {"start": v(5977.87, 585.16) * mm, "end": v(6028.67, 585.16) * mm});
            skLineSegment(sketch, "E9.3.8.3", {"start": v(6028.67, 635.96) * mm, "end": v(6028.67, 585.16) * mm});
            skLineSegment(sketch, "E9.3.9.0", {"start": v(5977.87, 572.46) * mm, "end": v(6028.67, 572.46) * mm});
            skLineSegment(sketch, "E9.3.9.1", {"start": v(5977.87, 572.46) * mm, "end": v(5977.87, 521.66) * mm});
            skLineSegment(sketch, "E9.3.9.2", {"start": v(5977.87, 521.66) * mm, "end": v(6028.67, 521.66) * mm});
            skLineSegment(sketch, "E9.3.9.3", {"start": v(6028.67, 572.46) * mm, "end": v(6028.67, 521.66) * mm});
            skLineSegment(sketch, "E9.4.0.0", {"start": v(6041.37, 1143.96) * mm, "end": v(6092.17, 1143.96) * mm});
            skLineSegment(sketch, "E9.4.0.1", {"start": v(6041.37, 1143.96) * mm, "end": v(6041.37, 1093.16) * mm});
            skLineSegment(sketch, "E9.4.0.2", {"start": v(6041.37, 1093.16) * mm, "end": v(6092.17, 1093.16) * mm});
            skLineSegment(sketch, "E9.4.0.3", {"start": v(6092.17, 1143.96) * mm, "end": v(6092.17, 1093.16) * mm});
            skLineSegment(sketch, "E9.4.1.0", {"start": v(6041.37, 1080.46) * mm, "end": v(6092.17, 1080.46) * mm});
            skLineSegment(sketch, "E9.4.1.1", {"start": v(6041.37, 1080.46) * mm, "end": v(6041.37, 1029.66) * mm});
            skLineSegment(sketch, "E9.4.1.2", {"start": v(6041.37, 1029.66) * mm, "end": v(6092.17, 1029.66) * mm});
            skLineSegment(sketch, "E9.4.1.3", {"start": v(6092.17, 1080.46) * mm, "end": v(6092.17, 1029.66) * mm});
            skLineSegment(sketch, "E9.4.2.0", {"start": v(6041.37, 1016.96) * mm, "end": v(6092.17, 1016.96) * mm});
            skLineSegment(sketch, "E9.4.2.1", {"start": v(6041.37, 1016.96) * mm, "end": v(6041.37, 966.16) * mm});
            skLineSegment(sketch, "E9.4.2.2", {"start": v(6041.37, 966.16) * mm, "end": v(6092.17, 966.16) * mm});
            skLineSegment(sketch, "E9.4.2.3", {"start": v(6092.17, 1016.96) * mm, "end": v(6092.17, 966.16) * mm});
            skLineSegment(sketch, "E9.4.3.0", {"start": v(6041.37, 953.46) * mm, "end": v(6092.17, 953.46) * mm});
            skLineSegment(sketch, "E9.4.3.1", {"start": v(6041.37, 953.46) * mm, "end": v(6041.37, 902.66) * mm});
            skLineSegment(sketch, "E9.4.3.2", {"start": v(6041.37, 902.66) * mm, "end": v(6092.17, 902.66) * mm});
            skLineSegment(sketch, "E9.4.3.3", {"start": v(6092.17, 953.46) * mm, "end": v(6092.17, 902.66) * mm});
            skLineSegment(sketch, "E9.4.4.0", {"start": v(6041.37, 889.96) * mm, "end": v(6092.17, 889.96) * mm});
            skLineSegment(sketch, "E9.4.4.1", {"start": v(6041.37, 889.96) * mm, "end": v(6041.37, 839.16) * mm});
            skLineSegment(sketch, "E9.4.4.2", {"start": v(6041.37, 839.16) * mm, "end": v(6092.17, 839.16) * mm});
            skLineSegment(sketch, "E9.4.4.3", {"start": v(6092.17, 889.96) * mm, "end": v(6092.17, 839.16) * mm});
            skLineSegment(sketch, "E9.4.5.0", {"start": v(6041.37, 826.46) * mm, "end": v(6092.17, 826.46) * mm});
            skLineSegment(sketch, "E9.4.5.1", {"start": v(6041.37, 826.46) * mm, "end": v(6041.37, 775.66) * mm});
            skLineSegment(sketch, "E9.4.5.2", {"start": v(6041.37, 775.66) * mm, "end": v(6092.17, 775.66) * mm});
            skLineSegment(sketch, "E9.4.5.3", {"start": v(6092.17, 826.46) * mm, "end": v(6092.17, 775.66) * mm});
            skLineSegment(sketch, "E9.4.6.0", {"start": v(6041.37, 762.96) * mm, "end": v(6092.17, 762.96) * mm});
            skLineSegment(sketch, "E9.4.6.1", {"start": v(6041.37, 762.96) * mm, "end": v(6041.37, 712.16) * mm});
            skLineSegment(sketch, "E9.4.6.2", {"start": v(6041.37, 712.16) * mm, "end": v(6092.17, 712.16) * mm});
            skLineSegment(sketch, "E9.4.6.3", {"start": v(6092.17, 762.96) * mm, "end": v(6092.17, 712.16) * mm});
            skLineSegment(sketch, "E9.4.7.0", {"start": v(6041.37, 699.46) * mm, "end": v(6092.17, 699.46) * mm});
            skLineSegment(sketch, "E9.4.7.1", {"start": v(6041.37, 699.46) * mm, "end": v(6041.37, 648.66) * mm});
            skLineSegment(sketch, "E9.4.7.2", {"start": v(6041.37, 648.66) * mm, "end": v(6092.17, 648.66) * mm});
            skLineSegment(sketch, "E9.4.7.3", {"start": v(6092.17, 699.46) * mm, "end": v(6092.17, 648.66) * mm});
            skLineSegment(sketch, "E9.4.8.0", {"start": v(6041.37, 635.96) * mm, "end": v(6092.17, 635.96) * mm});
            skLineSegment(sketch, "E9.4.8.1", {"start": v(6041.37, 635.96) * mm, "end": v(6041.37, 585.16) * mm});
            skLineSegment(sketch, "E9.4.8.2", {"start": v(6041.37, 585.16) * mm, "end": v(6092.17, 585.16) * mm});
            skLineSegment(sketch, "E9.4.8.3", {"start": v(6092.17, 635.96) * mm, "end": v(6092.17, 585.16) * mm});
            skLineSegment(sketch, "E9.4.9.0", {"start": v(6041.37, 572.46) * mm, "end": v(6092.17, 572.46) * mm});
            skLineSegment(sketch, "E9.4.9.1", {"start": v(6041.37, 572.46) * mm, "end": v(6041.37, 521.66) * mm});
            skLineSegment(sketch, "E9.4.9.2", {"start": v(6041.37, 521.66) * mm, "end": v(6092.17, 521.66) * mm});
            skLineSegment(sketch, "E9.4.9.3", {"start": v(6092.17, 572.46) * mm, "end": v(6092.17, 521.66) * mm});
            skLineSegment(sketch, "E9.5.0.0", {"start": v(6104.87, 1143.96) * mm, "end": v(6155.67, 1143.96) * mm});
            skLineSegment(sketch, "E9.5.0.1", {"start": v(6104.87, 1143.96) * mm, "end": v(6104.87, 1093.16) * mm});
            skLineSegment(sketch, "E9.5.0.2", {"start": v(6104.87, 1093.16) * mm, "end": v(6155.67, 1093.16) * mm});
            skLineSegment(sketch, "E9.5.0.3", {"start": v(6155.67, 1143.96) * mm, "end": v(6155.67, 1093.16) * mm});
            skLineSegment(sketch, "E9.5.1.0", {"start": v(6104.87, 1080.46) * mm, "end": v(6155.67, 1080.46) * mm});
            skLineSegment(sketch, "E9.5.1.1", {"start": v(6104.87, 1080.46) * mm, "end": v(6104.87, 1029.66) * mm});
            skLineSegment(sketch, "E9.5.1.2", {"start": v(6104.87, 1029.66) * mm, "end": v(6155.67, 1029.66) * mm});
            skLineSegment(sketch, "E9.5.1.3", {"start": v(6155.67, 1080.46) * mm, "end": v(6155.67, 1029.66) * mm});
            skLineSegment(sketch, "E9.5.2.0", {"start": v(6104.87, 1016.96) * mm, "end": v(6155.67, 1016.96) * mm});
            skLineSegment(sketch, "E9.5.2.1", {"start": v(6104.87, 1016.96) * mm, "end": v(6104.87, 966.16) * mm});
            skLineSegment(sketch, "E9.5.2.2", {"start": v(6104.87, 966.16) * mm, "end": v(6155.67, 966.16) * mm});
            skLineSegment(sketch, "E9.5.2.3", {"start": v(6155.67, 1016.96) * mm, "end": v(6155.67, 966.16) * mm});
            skLineSegment(sketch, "E9.5.3.0", {"start": v(6104.87, 953.46) * mm, "end": v(6155.67, 953.46) * mm});
            skLineSegment(sketch, "E9.5.3.1", {"start": v(6104.87, 953.46) * mm, "end": v(6104.87, 902.66) * mm});
            skLineSegment(sketch, "E9.5.3.2", {"start": v(6104.87, 902.66) * mm, "end": v(6155.67, 902.66) * mm});
            skLineSegment(sketch, "E9.5.3.3", {"start": v(6155.67, 953.46) * mm, "end": v(6155.67, 902.66) * mm});
            skLineSegment(sketch, "E9.5.4.0", {"start": v(6104.87, 889.96) * mm, "end": v(6155.67, 889.96) * mm});
            skLineSegment(sketch, "E9.5.4.1", {"start": v(6104.87, 889.96) * mm, "end": v(6104.87, 839.16) * mm});
            skLineSegment(sketch, "E9.5.4.2", {"start": v(6104.87, 839.16) * mm, "end": v(6155.67, 839.16) * mm});
            skLineSegment(sketch, "E9.5.4.3", {"start": v(6155.67, 889.96) * mm, "end": v(6155.67, 839.16) * mm});
            skLineSegment(sketch, "E9.5.5.0", {"start": v(6104.87, 826.46) * mm, "end": v(6155.67, 826.46) * mm});
            skLineSegment(sketch, "E9.5.5.1", {"start": v(6104.87, 826.46) * mm, "end": v(6104.87, 775.66) * mm});
            skLineSegment(sketch, "E9.5.5.2", {"start": v(6104.87, 775.66) * mm, "end": v(6155.67, 775.66) * mm});
            skLineSegment(sketch, "E9.5.5.3", {"start": v(6155.67, 826.46) * mm, "end": v(6155.67, 775.66) * mm});
            skLineSegment(sketch, "E9.5.6.0", {"start": v(6104.87, 762.96) * mm, "end": v(6155.67, 762.96) * mm});
            skLineSegment(sketch, "E9.5.6.1", {"start": v(6104.87, 762.96) * mm, "end": v(6104.87, 712.16) * mm});
            skLineSegment(sketch, "E9.5.6.2", {"start": v(6104.87, 712.16) * mm, "end": v(6155.67, 712.16) * mm});
            skLineSegment(sketch, "E9.5.6.3", {"start": v(6155.67, 762.96) * mm, "end": v(6155.67, 712.16) * mm});
            skLineSegment(sketch, "E9.5.7.0", {"start": v(6104.87, 699.46) * mm, "end": v(6155.67, 699.46) * mm});
            skLineSegment(sketch, "E9.5.7.1", {"start": v(6104.87, 699.46) * mm, "end": v(6104.87, 648.66) * mm});
            skLineSegment(sketch, "E9.5.7.2", {"start": v(6104.87, 648.66) * mm, "end": v(6155.67, 648.66) * mm});
            skLineSegment(sketch, "E9.5.7.3", {"start": v(6155.67, 699.46) * mm, "end": v(6155.67, 648.66) * mm});
            skLineSegment(sketch, "E9.5.8.0", {"start": v(6104.87, 635.96) * mm, "end": v(6155.67, 635.96) * mm});
            skLineSegment(sketch, "E9.5.8.1", {"start": v(6104.87, 635.96) * mm, "end": v(6104.87, 585.16) * mm});
            skLineSegment(sketch, "E9.5.8.2", {"start": v(6104.87, 585.16) * mm, "end": v(6155.67, 585.16) * mm});
            skLineSegment(sketch, "E9.5.8.3", {"start": v(6155.67, 635.96) * mm, "end": v(6155.67, 585.16) * mm});
            skLineSegment(sketch, "E9.5.9.0", {"start": v(6104.87, 572.46) * mm, "end": v(6155.67, 572.46) * mm});
            skLineSegment(sketch, "E9.5.9.1", {"start": v(6104.87, 572.46) * mm, "end": v(6104.87, 521.66) * mm});
            skLineSegment(sketch, "E9.5.9.2", {"start": v(6104.87, 521.66) * mm, "end": v(6155.67, 521.66) * mm});
            skLineSegment(sketch, "E9.5.9.3", {"start": v(6155.67, 572.46) * mm, "end": v(6155.67, 521.66) * mm});
            skLineSegment(sketch, "E9.6.0.0", {"start": v(6168.37, 1143.96) * mm, "end": v(6219.17, 1143.96) * mm});
            skLineSegment(sketch, "E9.6.0.1", {"start": v(6168.37, 1143.96) * mm, "end": v(6168.37, 1093.16) * mm});
            skLineSegment(sketch, "E9.6.0.2", {"start": v(6168.37, 1093.16) * mm, "end": v(6219.17, 1093.16) * mm});
            skLineSegment(sketch, "E9.6.0.3", {"start": v(6219.17, 1143.96) * mm, "end": v(6219.17, 1093.16) * mm});
            skLineSegment(sketch, "E9.6.1.0", {"start": v(6168.37, 1080.46) * mm, "end": v(6219.17, 1080.46) * mm});
            skLineSegment(sketch, "E9.6.1.1", {"start": v(6168.37, 1080.46) * mm, "end": v(6168.37, 1029.66) * mm});
            skLineSegment(sketch, "E9.6.1.2", {"start": v(6168.37, 1029.66) * mm, "end": v(6219.17, 1029.66) * mm});
            skLineSegment(sketch, "E9.6.1.3", {"start": v(6219.17, 1080.46) * mm, "end": v(6219.17, 1029.66) * mm});
            skLineSegment(sketch, "E9.6.2.0", {"start": v(6168.37, 1016.96) * mm, "end": v(6219.17, 1016.96) * mm});
            skLineSegment(sketch, "E9.6.2.1", {"start": v(6168.37, 1016.96) * mm, "end": v(6168.37, 966.16) * mm});
            skLineSegment(sketch, "E9.6.2.2", {"start": v(6168.37, 966.16) * mm, "end": v(6219.17, 966.16) * mm});
            skLineSegment(sketch, "E9.6.2.3", {"start": v(6219.17, 1016.96) * mm, "end": v(6219.17, 966.16) * mm});
            skLineSegment(sketch, "E9.6.3.0", {"start": v(6168.37, 953.46) * mm, "end": v(6219.17, 953.46) * mm});
            skLineSegment(sketch, "E9.6.3.1", {"start": v(6168.37, 953.46) * mm, "end": v(6168.37, 902.66) * mm});
            skLineSegment(sketch, "E9.6.3.2", {"start": v(6168.37, 902.66) * mm, "end": v(6219.17, 902.66) * mm});
            skLineSegment(sketch, "E9.6.3.3", {"start": v(6219.17, 953.46) * mm, "end": v(6219.17, 902.66) * mm});
            skLineSegment(sketch, "E9.6.4.0", {"start": v(6168.37, 889.96) * mm, "end": v(6219.17, 889.96) * mm});
            skLineSegment(sketch, "E9.6.4.1", {"start": v(6168.37, 889.96) * mm, "end": v(6168.37, 839.16) * mm});
            skLineSegment(sketch, "E9.6.4.2", {"start": v(6168.37, 839.16) * mm, "end": v(6219.17, 839.16) * mm});
            skLineSegment(sketch, "E9.6.4.3", {"start": v(6219.17, 889.96) * mm, "end": v(6219.17, 839.16) * mm});
            skLineSegment(sketch, "E9.6.5.0", {"start": v(6168.37, 826.46) * mm, "end": v(6219.17, 826.46) * mm});
            skLineSegment(sketch, "E9.6.5.1", {"start": v(6168.37, 826.46) * mm, "end": v(6168.37, 775.66) * mm});
            skLineSegment(sketch, "E9.6.5.2", {"start": v(6168.37, 775.66) * mm, "end": v(6219.17, 775.66) * mm});
            skLineSegment(sketch, "E9.6.5.3", {"start": v(6219.17, 826.46) * mm, "end": v(6219.17, 775.66) * mm});
            skLineSegment(sketch, "E9.6.6.0", {"start": v(6168.37, 762.96) * mm, "end": v(6219.17, 762.96) * mm});
            skLineSegment(sketch, "E9.6.6.1", {"start": v(6168.37, 762.96) * mm, "end": v(6168.37, 712.16) * mm});
            skLineSegment(sketch, "E9.6.6.2", {"start": v(6168.37, 712.16) * mm, "end": v(6219.17, 712.16) * mm});
            skLineSegment(sketch, "E9.6.6.3", {"start": v(6219.17, 762.96) * mm, "end": v(6219.17, 712.16) * mm});
            skLineSegment(sketch, "E9.6.7.0", {"start": v(6168.37, 699.46) * mm, "end": v(6219.17, 699.46) * mm});
            skLineSegment(sketch, "E9.6.7.1", {"start": v(6168.37, 699.46) * mm, "end": v(6168.37, 648.66) * mm});
            skLineSegment(sketch, "E9.6.7.2", {"start": v(6168.37, 648.66) * mm, "end": v(6219.17, 648.66) * mm});
            skLineSegment(sketch, "E9.6.7.3", {"start": v(6219.17, 699.46) * mm, "end": v(6219.17, 648.66) * mm});
            skLineSegment(sketch, "E9.6.8.0", {"start": v(6168.37, 635.96) * mm, "end": v(6219.17, 635.96) * mm});
            skLineSegment(sketch, "E9.6.8.1", {"start": v(6168.37, 635.96) * mm, "end": v(6168.37, 585.16) * mm});
            skLineSegment(sketch, "E9.6.8.2", {"start": v(6168.37, 585.16) * mm, "end": v(6219.17, 585.16) * mm});
            skLineSegment(sketch, "E9.6.8.3", {"start": v(6219.17, 635.96) * mm, "end": v(6219.17, 585.16) * mm});
            skLineSegment(sketch, "E9.6.9.0", {"start": v(6168.37, 572.46) * mm, "end": v(6219.17, 572.46) * mm});
            skLineSegment(sketch, "E9.6.9.1", {"start": v(6168.37, 572.46) * mm, "end": v(6168.37, 521.66) * mm});
            skLineSegment(sketch, "E9.6.9.2", {"start": v(6168.37, 521.66) * mm, "end": v(6219.17, 521.66) * mm});
            skLineSegment(sketch, "E9.6.9.3", {"start": v(6219.17, 572.46) * mm, "end": v(6219.17, 521.66) * mm});
            skLineSegment(sketch, "E9.7.0.0", {"start": v(6231.87, 1143.96) * mm, "end": v(6282.67, 1143.96) * mm});
            skLineSegment(sketch, "E9.7.0.1", {"start": v(6231.87, 1143.96) * mm, "end": v(6231.87, 1093.16) * mm});
            skLineSegment(sketch, "E9.7.0.2", {"start": v(6231.87, 1093.16) * mm, "end": v(6282.67, 1093.16) * mm});
            skLineSegment(sketch, "E9.7.0.3", {"start": v(6282.67, 1143.96) * mm, "end": v(6282.67, 1093.16) * mm});
            skLineSegment(sketch, "E9.7.1.0", {"start": v(6231.87, 1080.46) * mm, "end": v(6282.67, 1080.46) * mm});
            skLineSegment(sketch, "E9.7.1.1", {"start": v(6231.87, 1080.46) * mm, "end": v(6231.87, 1029.66) * mm});
            skLineSegment(sketch, "E9.7.1.2", {"start": v(6231.87, 1029.66) * mm, "end": v(6282.67, 1029.66) * mm});
            skLineSegment(sketch, "E9.7.1.3", {"start": v(6282.67, 1080.46) * mm, "end": v(6282.67, 1029.66) * mm});
            skLineSegment(sketch, "E9.7.2.0", {"start": v(6231.87, 1016.96) * mm, "end": v(6282.67, 1016.96) * mm});
            skLineSegment(sketch, "E9.7.2.1", {"start": v(6231.87, 1016.96) * mm, "end": v(6231.87, 966.16) * mm});
            skLineSegment(sketch, "E9.7.2.2", {"start": v(6231.87, 966.16) * mm, "end": v(6282.67, 966.16) * mm});
            skLineSegment(sketch, "E9.7.2.3", {"start": v(6282.67, 1016.96) * mm, "end": v(6282.67, 966.16) * mm});
            skLineSegment(sketch, "E9.7.3.0", {"start": v(6231.87, 953.46) * mm, "end": v(6282.67, 953.46) * mm});
            skLineSegment(sketch, "E9.7.3.1", {"start": v(6231.87, 953.46) * mm, "end": v(6231.87, 902.66) * mm});
            skLineSegment(sketch, "E9.7.3.2", {"start": v(6231.87, 902.66) * mm, "end": v(6282.67, 902.66) * mm});
            skLineSegment(sketch, "E9.7.3.3", {"start": v(6282.67, 953.46) * mm, "end": v(6282.67, 902.66) * mm});
            skLineSegment(sketch, "E9.7.4.0", {"start": v(6231.87, 889.96) * mm, "end": v(6282.67, 889.96) * mm});
            skLineSegment(sketch, "E9.7.4.1", {"start": v(6231.87, 889.96) * mm, "end": v(6231.87, 839.16) * mm});
            skLineSegment(sketch, "E9.7.4.2", {"start": v(6231.87, 839.16) * mm, "end": v(6282.67, 839.16) * mm});
            skLineSegment(sketch, "E9.7.4.3", {"start": v(6282.67, 889.96) * mm, "end": v(6282.67, 839.16) * mm});
            skLineSegment(sketch, "E9.7.5.0", {"start": v(6231.87, 826.46) * mm, "end": v(6282.67, 826.46) * mm});
            skLineSegment(sketch, "E9.7.5.1", {"start": v(6231.87, 826.46) * mm, "end": v(6231.87, 775.66) * mm});
            skLineSegment(sketch, "E9.7.5.2", {"start": v(6231.87, 775.66) * mm, "end": v(6282.67, 775.66) * mm});
            skLineSegment(sketch, "E9.7.5.3", {"start": v(6282.67, 826.46) * mm, "end": v(6282.67, 775.66) * mm});
            skLineSegment(sketch, "E9.7.6.0", {"start": v(6231.87, 762.96) * mm, "end": v(6282.67, 762.96) * mm});
            skLineSegment(sketch, "E9.7.6.1", {"start": v(6231.87, 762.96) * mm, "end": v(6231.87, 712.16) * mm});
            skLineSegment(sketch, "E9.7.6.2", {"start": v(6231.87, 712.16) * mm, "end": v(6282.67, 712.16) * mm});
            skLineSegment(sketch, "E9.7.6.3", {"start": v(6282.67, 762.96) * mm, "end": v(6282.67, 712.16) * mm});
            skLineSegment(sketch, "E9.7.7.0", {"start": v(6231.87, 699.46) * mm, "end": v(6282.67, 699.46) * mm});
            skLineSegment(sketch, "E9.7.7.1", {"start": v(6231.87, 699.46) * mm, "end": v(6231.87, 648.66) * mm});
            skLineSegment(sketch, "E9.7.7.2", {"start": v(6231.87, 648.66) * mm, "end": v(6282.67, 648.66) * mm});
            skLineSegment(sketch, "E9.7.7.3", {"start": v(6282.67, 699.46) * mm, "end": v(6282.67, 648.66) * mm});
            skLineSegment(sketch, "E9.7.8.0", {"start": v(6231.87, 635.96) * mm, "end": v(6282.67, 635.96) * mm});
            skLineSegment(sketch, "E9.7.8.1", {"start": v(6231.87, 635.96) * mm, "end": v(6231.87, 585.16) * mm});
            skLineSegment(sketch, "E9.7.8.2", {"start": v(6231.87, 585.16) * mm, "end": v(6282.67, 585.16) * mm});
            skLineSegment(sketch, "E9.7.8.3", {"start": v(6282.67, 635.96) * mm, "end": v(6282.67, 585.16) * mm});
            skLineSegment(sketch, "E9.7.9.0", {"start": v(6231.87, 572.46) * mm, "end": v(6282.67, 572.46) * mm});
            skLineSegment(sketch, "E9.7.9.1", {"start": v(6231.87, 572.46) * mm, "end": v(6231.87, 521.66) * mm});
            skLineSegment(sketch, "E9.7.9.2", {"start": v(6231.87, 521.66) * mm, "end": v(6282.67, 521.66) * mm});
            skLineSegment(sketch, "E9.7.9.3", {"start": v(6282.67, 572.46) * mm, "end": v(6282.67, 521.66) * mm});
            skLineSegment(sketch, "E9.8.0.0", {"start": v(6295.37, 1143.96) * mm, "end": v(6346.17, 1143.96) * mm});
            skLineSegment(sketch, "E9.8.0.1", {"start": v(6295.37, 1143.96) * mm, "end": v(6295.37, 1093.16) * mm});
            skLineSegment(sketch, "E9.8.0.2", {"start": v(6295.37, 1093.16) * mm, "end": v(6346.17, 1093.16) * mm});
            skLineSegment(sketch, "E9.8.0.3", {"start": v(6346.17, 1143.96) * mm, "end": v(6346.17, 1093.16) * mm});
            skLineSegment(sketch, "E9.8.1.0", {"start": v(6295.37, 1080.46) * mm, "end": v(6346.17, 1080.46) * mm});
            skLineSegment(sketch, "E9.8.1.1", {"start": v(6295.37, 1080.46) * mm, "end": v(6295.37, 1029.66) * mm});
            skLineSegment(sketch, "E9.8.1.2", {"start": v(6295.37, 1029.66) * mm, "end": v(6346.17, 1029.66) * mm});
            skLineSegment(sketch, "E9.8.1.3", {"start": v(6346.17, 1080.46) * mm, "end": v(6346.17, 1029.66) * mm});
            skLineSegment(sketch, "E9.8.2.0", {"start": v(6295.37, 1016.96) * mm, "end": v(6346.17, 1016.96) * mm});
            skLineSegment(sketch, "E9.8.2.1", {"start": v(6295.37, 1016.96) * mm, "end": v(6295.37, 966.16) * mm});
            skLineSegment(sketch, "E9.8.2.2", {"start": v(6295.37, 966.16) * mm, "end": v(6346.17, 966.16) * mm});
            skLineSegment(sketch, "E9.8.2.3", {"start": v(6346.17, 1016.96) * mm, "end": v(6346.17, 966.16) * mm});
            skLineSegment(sketch, "E9.8.3.0", {"start": v(6295.37, 953.46) * mm, "end": v(6346.17, 953.46) * mm});
            skLineSegment(sketch, "E9.8.3.1", {"start": v(6295.37, 953.46) * mm, "end": v(6295.37, 902.66) * mm});
            skLineSegment(sketch, "E9.8.3.2", {"start": v(6295.37, 902.66) * mm, "end": v(6346.17, 902.66) * mm});
            skLineSegment(sketch, "E9.8.3.3", {"start": v(6346.17, 953.46) * mm, "end": v(6346.17, 902.66) * mm});
            skLineSegment(sketch, "E9.8.4.0", {"start": v(6295.37, 889.96) * mm, "end": v(6346.17, 889.96) * mm});
            skLineSegment(sketch, "E9.8.4.1", {"start": v(6295.37, 889.96) * mm, "end": v(6295.37, 839.16) * mm});
            skLineSegment(sketch, "E9.8.4.2", {"start": v(6295.37, 839.16) * mm, "end": v(6346.17, 839.16) * mm});
            skLineSegment(sketch, "E9.8.4.3", {"start": v(6346.17, 889.96) * mm, "end": v(6346.17, 839.16) * mm});
            skLineSegment(sketch, "E9.8.5.0", {"start": v(6295.37, 826.46) * mm, "end": v(6346.17, 826.46) * mm});
            skLineSegment(sketch, "E9.8.5.1", {"start": v(6295.37, 826.46) * mm, "end": v(6295.37, 775.66) * mm});
            skLineSegment(sketch, "E9.8.5.2", {"start": v(6295.37, 775.66) * mm, "end": v(6346.17, 775.66) * mm});
            skLineSegment(sketch, "E9.8.5.3", {"start": v(6346.17, 826.46) * mm, "end": v(6346.17, 775.66) * mm});
            skLineSegment(sketch, "E9.8.6.0", {"start": v(6295.37, 762.96) * mm, "end": v(6346.17, 762.96) * mm});
            skLineSegment(sketch, "E9.8.6.1", {"start": v(6295.37, 762.96) * mm, "end": v(6295.37, 712.16) * mm});
            skLineSegment(sketch, "E9.8.6.2", {"start": v(6295.37, 712.16) * mm, "end": v(6346.17, 712.16) * mm});
            skLineSegment(sketch, "E9.8.6.3", {"start": v(6346.17, 762.96) * mm, "end": v(6346.17, 712.16) * mm});
            skLineSegment(sketch, "E9.8.7.0", {"start": v(6295.37, 699.46) * mm, "end": v(6346.17, 699.46) * mm});
            skLineSegment(sketch, "E9.8.7.1", {"start": v(6295.37, 699.46) * mm, "end": v(6295.37, 648.66) * mm});
            skLineSegment(sketch, "E9.8.7.2", {"start": v(6295.37, 648.66) * mm, "end": v(6346.17, 648.66) * mm});
            skLineSegment(sketch, "E9.8.7.3", {"start": v(6346.17, 699.46) * mm, "end": v(6346.17, 648.66) * mm});
            skLineSegment(sketch, "E9.8.8.0", {"start": v(6295.37, 635.96) * mm, "end": v(6346.17, 635.96) * mm});
            skLineSegment(sketch, "E9.8.8.1", {"start": v(6295.37, 635.96) * mm, "end": v(6295.37, 585.16) * mm});
            skLineSegment(sketch, "E9.8.8.2", {"start": v(6295.37, 585.16) * mm, "end": v(6346.17, 585.16) * mm});
            skLineSegment(sketch, "E9.8.8.3", {"start": v(6346.17, 635.96) * mm, "end": v(6346.17, 585.16) * mm});
            skLineSegment(sketch, "E9.8.9.0", {"start": v(6295.37, 572.46) * mm, "end": v(6346.17, 572.46) * mm});
            skLineSegment(sketch, "E9.8.9.1", {"start": v(6295.37, 572.46) * mm, "end": v(6295.37, 521.66) * mm});
            skLineSegment(sketch, "E9.8.9.2", {"start": v(6295.37, 521.66) * mm, "end": v(6346.17, 521.66) * mm});
            skLineSegment(sketch, "E9.8.9.3", {"start": v(6346.17, 572.46) * mm, "end": v(6346.17, 521.66) * mm});
            skLineSegment(sketch, "E9.9.0.0", {"start": v(6358.87, 1143.96) * mm, "end": v(6409.67, 1143.96) * mm});
            skLineSegment(sketch, "E9.9.0.1", {"start": v(6358.87, 1143.96) * mm, "end": v(6358.87, 1093.16) * mm});
            skLineSegment(sketch, "E9.9.0.2", {"start": v(6358.87, 1093.16) * mm, "end": v(6409.67, 1093.16) * mm});
            skLineSegment(sketch, "E9.9.0.3", {"start": v(6409.67, 1143.96) * mm, "end": v(6409.67, 1093.16) * mm});
            skLineSegment(sketch, "E9.9.1.0", {"start": v(6358.87, 1080.46) * mm, "end": v(6409.67, 1080.46) * mm});
            skLineSegment(sketch, "E9.9.1.1", {"start": v(6358.87, 1080.46) * mm, "end": v(6358.87, 1029.66) * mm});
            skLineSegment(sketch, "E9.9.1.2", {"start": v(6358.87, 1029.66) * mm, "end": v(6409.67, 1029.66) * mm});
            skLineSegment(sketch, "E9.9.1.3", {"start": v(6409.67, 1080.46) * mm, "end": v(6409.67, 1029.66) * mm});
            skLineSegment(sketch, "E9.9.2.0", {"start": v(6358.87, 1016.96) * mm, "end": v(6409.67, 1016.96) * mm});
            skLineSegment(sketch, "E9.9.2.1", {"start": v(6358.87, 1016.96) * mm, "end": v(6358.87, 966.16) * mm});
            skLineSegment(sketch, "E9.9.2.2", {"start": v(6358.87, 966.16) * mm, "end": v(6409.67, 966.16) * mm});
            skLineSegment(sketch, "E9.9.2.3", {"start": v(6409.67, 1016.96) * mm, "end": v(6409.67, 966.16) * mm});
            skLineSegment(sketch, "E9.9.3.0", {"start": v(6358.87, 953.46) * mm, "end": v(6409.67, 953.46) * mm});
            skLineSegment(sketch, "E9.9.3.1", {"start": v(6358.87, 953.46) * mm, "end": v(6358.87, 902.66) * mm});
            skLineSegment(sketch, "E9.9.3.2", {"start": v(6358.87, 902.66) * mm, "end": v(6409.67, 902.66) * mm});
            skLineSegment(sketch, "E9.9.3.3", {"start": v(6409.67, 953.46) * mm, "end": v(6409.67, 902.66) * mm});
            skLineSegment(sketch, "E9.9.4.0", {"start": v(6358.87, 889.96) * mm, "end": v(6409.67, 889.96) * mm});
            skLineSegment(sketch, "E9.9.4.1", {"start": v(6358.87, 889.96) * mm, "end": v(6358.87, 839.16) * mm});
            skLineSegment(sketch, "E9.9.4.2", {"start": v(6358.87, 839.16) * mm, "end": v(6409.67, 839.16) * mm});
            skLineSegment(sketch, "E9.9.4.3", {"start": v(6409.67, 889.96) * mm, "end": v(6409.67, 839.16) * mm});
            skLineSegment(sketch, "E9.9.5.0", {"start": v(6358.87, 826.46) * mm, "end": v(6409.67, 826.46) * mm});
            skLineSegment(sketch, "E9.9.5.1", {"start": v(6358.87, 826.46) * mm, "end": v(6358.87, 775.66) * mm});
            skLineSegment(sketch, "E9.9.5.2", {"start": v(6358.87, 775.66) * mm, "end": v(6409.67, 775.66) * mm});
            skLineSegment(sketch, "E9.9.5.3", {"start": v(6409.67, 826.46) * mm, "end": v(6409.67, 775.66) * mm});
            skLineSegment(sketch, "E9.9.6.0", {"start": v(6358.87, 762.96) * mm, "end": v(6409.67, 762.96) * mm});
            skLineSegment(sketch, "E9.9.6.1", {"start": v(6358.87, 762.96) * mm, "end": v(6358.87, 712.16) * mm});
            skLineSegment(sketch, "E9.9.6.2", {"start": v(6358.87, 712.16) * mm, "end": v(6409.67, 712.16) * mm});
            skLineSegment(sketch, "E9.9.6.3", {"start": v(6409.67, 762.96) * mm, "end": v(6409.67, 712.16) * mm});
            skLineSegment(sketch, "E9.9.7.0", {"start": v(6358.87, 699.46) * mm, "end": v(6409.67, 699.46) * mm});
            skLineSegment(sketch, "E9.9.7.1", {"start": v(6358.87, 699.46) * mm, "end": v(6358.87, 648.66) * mm});
            skLineSegment(sketch, "E9.9.7.2", {"start": v(6358.87, 648.66) * mm, "end": v(6409.67, 648.66) * mm});
            skLineSegment(sketch, "E9.9.7.3", {"start": v(6409.67, 699.46) * mm, "end": v(6409.67, 648.66) * mm});
            skLineSegment(sketch, "E9.9.8.0", {"start": v(6358.87, 635.96) * mm, "end": v(6409.67, 635.96) * mm});
            skLineSegment(sketch, "E9.9.8.1", {"start": v(6358.87, 635.96) * mm, "end": v(6358.87, 585.16) * mm});
            skLineSegment(sketch, "E9.9.8.2", {"start": v(6358.87, 585.16) * mm, "end": v(6409.67, 585.16) * mm});
            skLineSegment(sketch, "E9.9.8.3", {"start": v(6409.67, 635.96) * mm, "end": v(6409.67, 585.16) * mm});
            skLineSegment(sketch, "E9.9.9.0", {"start": v(6358.87, 572.46) * mm, "end": v(6409.67, 572.46) * mm});
            skLineSegment(sketch, "E9.9.9.1", {"start": v(6358.87, 572.46) * mm, "end": v(6358.87, 521.66) * mm});
            skLineSegment(sketch, "E9.9.9.2", {"start": v(6358.87, 521.66) * mm, "end": v(6409.67, 521.66) * mm});
            skLineSegment(sketch, "E9.9.9.3", {"start": v(6409.67, 572.46) * mm, "end": v(6409.67, 521.66) * mm});
            skLineSegment(sketch, "E9.direction1", {"start": v(5787.37, 1143.96) * mm, "end": v(5850.87, 1143.96) * mm, "construction": true});
            skLineSegment(sketch, "E9.direction2", {"start": v(5787.37, 1143.96) * mm, "end": v(5787.37, 1080.46) * mm, "construction": true});
            skSolve(sketch);
        }
        {
            var Q0;
            Q0 = qSketchRegion(id + "F9", true);
            extrude(context, id + "F10", {"entities" : qUnion([Q0]), "operationType" : NewBodyOperationType.REMOVE, "endBound" : BoundingType.UP_TO_NEXT, "oppositeDirection" : true, "depth" : 25.4 * mm});
        }
        {
            var Q0;
            Q0=makeQuery(id+"F4.boolean.opBoolean","MERGE",FACE,{"derivedFrom":[makeQuery(id+"F3.boolean.opBoolean","MERGE",FACE,{"derivedFrom":[makeQuery(id+"F2.opExtrude","SWEPT_FACE",FACE,{"disambiguationData":[OSD([sQuery(id+"F0.wireOp",EDGE,"E1.bottom")])]}),makeQuery(id+"F3.opExtrude","SWEPT_FACE",FACE,{"disambiguationData":[OSD([sQuery(id+"F0.wireOp",EDGE,"E2.bottom")])]})]}),makeQuery(id+"F4.opExtrude","SWEPT_FACE",FACE,{"disambiguationData":[OSD([sQuery(id+"F0.wireOp",EDGE,"E3.bottom")])]})]});
            var sketch = newSketch(context, id + "F11", { "sketchPlane" : qUnion([Q0])});
            skLineSegment(sketch, "E10.bottom", {"start": v(5787.37, 508.96) * mm, "end": v(5838.17, 508.96) * mm});
            skLineSegment(sketch, "E10.top", {"start": v(5787.37, 458.16) * mm, "end": v(5838.17, 458.16) * mm});
            skLineSegment(sketch, "E10.left", {"start": v(5787.37, 508.96) * mm, "end": v(5787.37, 458.16) * mm});
            skLineSegment(sketch, "E10.right", {"start": v(5838.17, 508.96) * mm, "end": v(5838.17, 458.16) * mm});
            skLineSegment(sketch, "E11.0.1.0", {"start": v(5838.17, 445.46) * mm, "end": v(5838.17, 394.66) * mm});
            skLineSegment(sketch, "E11.0.1.1", {"start": v(5787.37, 394.66) * mm, "end": v(5838.17, 394.66) * mm});
            skLineSegment(sketch, "E11.0.1.2", {"start": v(5787.37, 445.46) * mm, "end": v(5787.37, 394.66) * mm});
            skLineSegment(sketch, "E11.0.1.3", {"start": v(5787.37, 445.46) * mm, "end": v(5838.17, 445.46) * mm});
            skLineSegment(sketch, "E11.0.2.0", {"start": v(5838.17, 381.96) * mm, "end": v(5838.17, 331.16) * mm});
            skLineSegment(sketch, "E11.0.2.1", {"start": v(5787.37, 331.16) * mm, "end": v(5838.17, 331.16) * mm});
            skLineSegment(sketch, "E11.0.2.2", {"start": v(5787.37, 381.96) * mm, "end": v(5787.37, 331.16) * mm});
            skLineSegment(sketch, "E11.0.2.3", {"start": v(5787.37, 381.96) * mm, "end": v(5838.17, 381.96) * mm});
            skLineSegment(sketch, "E11.0.3.0", {"start": v(5838.17, 318.46) * mm, "end": v(5838.17, 267.66) * mm});
            skLineSegment(sketch, "E11.0.3.1", {"start": v(5787.37, 267.66) * mm, "end": v(5838.17, 267.66) * mm});
            skLineSegment(sketch, "E11.0.3.2", {"start": v(5787.37, 318.46) * mm, "end": v(5787.37, 267.66) * mm});
            skLineSegment(sketch, "E11.0.3.3", {"start": v(5787.37, 318.46) * mm, "end": v(5838.17, 318.46) * mm});
            skLineSegment(sketch, "E11.0.4.0", {"start": v(5838.17, 254.96) * mm, "end": v(5838.17, 204.16) * mm});
            skLineSegment(sketch, "E11.0.4.1", {"start": v(5787.37, 204.16) * mm, "end": v(5838.17, 204.16) * mm});
            skLineSegment(sketch, "E11.0.4.2", {"start": v(5787.37, 254.96) * mm, "end": v(5787.37, 204.16) * mm});
            skLineSegment(sketch, "E11.0.4.3", {"start": v(5787.37, 254.96) * mm, "end": v(5838.17, 254.96) * mm});
            skLineSegment(sketch, "E11.0.5.0", {"start": v(5838.17, 191.46) * mm, "end": v(5838.17, 140.66) * mm});
            skLineSegment(sketch, "E11.0.5.1", {"start": v(5787.37, 140.66) * mm, "end": v(5838.17, 140.66) * mm});
            skLineSegment(sketch, "E11.0.5.2", {"start": v(5787.37, 191.46) * mm, "end": v(5787.37, 140.66) * mm});
            skLineSegment(sketch, "E11.0.5.3", {"start": v(5787.37, 191.46) * mm, "end": v(5838.17, 191.46) * mm});
            skLineSegment(sketch, "E11.0.6.0", {"start": v(5838.17, 127.96) * mm, "end": v(5838.17, 77.16) * mm});
            skLineSegment(sketch, "E11.0.6.1", {"start": v(5787.37, 77.16) * mm, "end": v(5838.17, 77.16) * mm});
            skLineSegment(sketch, "E11.0.6.2", {"start": v(5787.37, 127.96) * mm, "end": v(5787.37, 77.16) * mm});
            skLineSegment(sketch, "E11.0.6.3", {"start": v(5787.37, 127.96) * mm, "end": v(5838.17, 127.96) * mm});
            skLineSegment(sketch, "E11.0.7.0", {"start": v(5838.17, 64.46) * mm, "end": v(5838.17, 13.66) * mm});
            skLineSegment(sketch, "E11.0.7.1", {"start": v(5787.37, 13.66) * mm, "end": v(5838.17, 13.66) * mm});
            skLineSegment(sketch, "E11.0.7.2", {"start": v(5787.37, 64.46) * mm, "end": v(5787.37, 13.66) * mm});
            skLineSegment(sketch, "E11.0.7.3", {"start": v(5787.37, 64.46) * mm, "end": v(5838.17, 64.46) * mm});
            skLineSegment(sketch, "E11.1.0.0", {"start": v(5901.67, 508.96) * mm, "end": v(5901.67, 458.16) * mm});
            skLineSegment(sketch, "E11.1.0.1", {"start": v(5850.87, 458.16) * mm, "end": v(5901.67, 458.16) * mm});
            skLineSegment(sketch, "E11.1.0.2", {"start": v(5850.87, 508.96) * mm, "end": v(5850.87, 458.16) * mm});
            skLineSegment(sketch, "E11.1.0.3", {"start": v(5850.87, 508.96) * mm, "end": v(5901.67, 508.96) * mm});
            skLineSegment(sketch, "E11.1.1.0", {"start": v(5901.67, 445.46) * mm, "end": v(5901.67, 394.66) * mm});
            skLineSegment(sketch, "E11.1.1.1", {"start": v(5850.87, 394.66) * mm, "end": v(5901.67, 394.66) * mm});
            skLineSegment(sketch, "E11.1.1.2", {"start": v(5850.87, 445.46) * mm, "end": v(5850.87, 394.66) * mm});
            skLineSegment(sketch, "E11.1.1.3", {"start": v(5850.87, 445.46) * mm, "end": v(5901.67, 445.46) * mm});
            skLineSegment(sketch, "E11.1.2.0", {"start": v(5901.67, 381.96) * mm, "end": v(5901.67, 331.16) * mm});
            skLineSegment(sketch, "E11.1.2.1", {"start": v(5850.87, 331.16) * mm, "end": v(5901.67, 331.16) * mm});
            skLineSegment(sketch, "E11.1.2.2", {"start": v(5850.87, 381.96) * mm, "end": v(5850.87, 331.16) * mm});
            skLineSegment(sketch, "E11.1.2.3", {"start": v(5850.87, 381.96) * mm, "end": v(5901.67, 381.96) * mm});
            skLineSegment(sketch, "E11.1.3.0", {"start": v(5901.67, 318.46) * mm, "end": v(5901.67, 267.66) * mm});
            skLineSegment(sketch, "E11.1.3.1", {"start": v(5850.87, 267.66) * mm, "end": v(5901.67, 267.66) * mm});
            skLineSegment(sketch, "E11.1.3.2", {"start": v(5850.87, 318.46) * mm, "end": v(5850.87, 267.66) * mm});
            skLineSegment(sketch, "E11.1.3.3", {"start": v(5850.87, 318.46) * mm, "end": v(5901.67, 318.46) * mm});
            skLineSegment(sketch, "E11.1.4.0", {"start": v(5901.67, 254.96) * mm, "end": v(5901.67, 204.16) * mm});
            skLineSegment(sketch, "E11.1.4.1", {"start": v(5850.87, 204.16) * mm, "end": v(5901.67, 204.16) * mm});
            skLineSegment(sketch, "E11.1.4.2", {"start": v(5850.87, 254.96) * mm, "end": v(5850.87, 204.16) * mm});
            skLineSegment(sketch, "E11.1.4.3", {"start": v(5850.87, 254.96) * mm, "end": v(5901.67, 254.96) * mm});
            skLineSegment(sketch, "E11.1.5.0", {"start": v(5901.67, 191.46) * mm, "end": v(5901.67, 140.66) * mm});
            skLineSegment(sketch, "E11.1.5.1", {"start": v(5850.87, 140.66) * mm, "end": v(5901.67, 140.66) * mm});
            skLineSegment(sketch, "E11.1.5.2", {"start": v(5850.87, 191.46) * mm, "end": v(5850.87, 140.66) * mm});
            skLineSegment(sketch, "E11.1.5.3", {"start": v(5850.87, 191.46) * mm, "end": v(5901.67, 191.46) * mm});
            skLineSegment(sketch, "E11.1.6.0", {"start": v(5901.67, 127.96) * mm, "end": v(5901.67, 77.16) * mm});
            skLineSegment(sketch, "E11.1.6.1", {"start": v(5850.87, 77.16) * mm, "end": v(5901.67, 77.16) * mm});
            skLineSegment(sketch, "E11.1.6.2", {"start": v(5850.87, 127.96) * mm, "end": v(5850.87, 77.16) * mm});
            skLineSegment(sketch, "E11.1.6.3", {"start": v(5850.87, 127.96) * mm, "end": v(5901.67, 127.96) * mm});
            skLineSegment(sketch, "E11.1.7.0", {"start": v(5901.67, 64.46) * mm, "end": v(5901.67, 13.66) * mm});
            skLineSegment(sketch, "E11.1.7.1", {"start": v(5850.87, 13.66) * mm, "end": v(5901.67, 13.66) * mm});
            skLineSegment(sketch, "E11.1.7.2", {"start": v(5850.87, 64.46) * mm, "end": v(5850.87, 13.66) * mm});
            skLineSegment(sketch, "E11.1.7.3", {"start": v(5850.87, 64.46) * mm, "end": v(5901.67, 64.46) * mm});
            skLineSegment(sketch, "E11.2.0.0", {"start": v(5965.17, 508.96) * mm, "end": v(5965.17, 458.16) * mm});
            skLineSegment(sketch, "E11.2.0.1", {"start": v(5914.37, 458.16) * mm, "end": v(5965.17, 458.16) * mm});
            skLineSegment(sketch, "E11.2.0.2", {"start": v(5914.37, 508.96) * mm, "end": v(5914.37, 458.16) * mm});
            skLineSegment(sketch, "E11.2.0.3", {"start": v(5914.37, 508.96) * mm, "end": v(5965.17, 508.96) * mm});
            skLineSegment(sketch, "E11.2.1.0", {"start": v(5965.17, 445.46) * mm, "end": v(5965.17, 394.66) * mm});
            skLineSegment(sketch, "E11.2.1.1", {"start": v(5914.37, 394.66) * mm, "end": v(5965.17, 394.66) * mm});
            skLineSegment(sketch, "E11.2.1.2", {"start": v(5914.37, 445.46) * mm, "end": v(5914.37, 394.66) * mm});
            skLineSegment(sketch, "E11.2.1.3", {"start": v(5914.37, 445.46) * mm, "end": v(5965.17, 445.46) * mm});
            skLineSegment(sketch, "E11.2.2.0", {"start": v(5965.17, 381.96) * mm, "end": v(5965.17, 331.16) * mm});
            skLineSegment(sketch, "E11.2.2.1", {"start": v(5914.37, 331.16) * mm, "end": v(5965.17, 331.16) * mm});
            skLineSegment(sketch, "E11.2.2.2", {"start": v(5914.37, 381.96) * mm, "end": v(5914.37, 331.16) * mm});
            skLineSegment(sketch, "E11.2.2.3", {"start": v(5914.37, 381.96) * mm, "end": v(5965.17, 381.96) * mm});
            skLineSegment(sketch, "E11.2.3.0", {"start": v(5965.17, 318.46) * mm, "end": v(5965.17, 267.66) * mm});
            skLineSegment(sketch, "E11.2.3.1", {"start": v(5914.37, 267.66) * mm, "end": v(5965.17, 267.66) * mm});
            skLineSegment(sketch, "E11.2.3.2", {"start": v(5914.37, 318.46) * mm, "end": v(5914.37, 267.66) * mm});
            skLineSegment(sketch, "E11.2.3.3", {"start": v(5914.37, 318.46) * mm, "end": v(5965.17, 318.46) * mm});
            skLineSegment(sketch, "E11.2.4.0", {"start": v(5965.17, 254.96) * mm, "end": v(5965.17, 204.16) * mm});
            skLineSegment(sketch, "E11.2.4.1", {"start": v(5914.37, 204.16) * mm, "end": v(5965.17, 204.16) * mm});
            skLineSegment(sketch, "E11.2.4.2", {"start": v(5914.37, 254.96) * mm, "end": v(5914.37, 204.16) * mm});
            skLineSegment(sketch, "E11.2.4.3", {"start": v(5914.37, 254.96) * mm, "end": v(5965.17, 254.96) * mm});
            skLineSegment(sketch, "E11.2.5.0", {"start": v(5965.17, 191.46) * mm, "end": v(5965.17, 140.66) * mm});
            skLineSegment(sketch, "E11.2.5.1", {"start": v(5914.37, 140.66) * mm, "end": v(5965.17, 140.66) * mm});
            skLineSegment(sketch, "E11.2.5.2", {"start": v(5914.37, 191.46) * mm, "end": v(5914.37, 140.66) * mm});
            skLineSegment(sketch, "E11.2.5.3", {"start": v(5914.37, 191.46) * mm, "end": v(5965.17, 191.46) * mm});
            skLineSegment(sketch, "E11.2.6.0", {"start": v(5965.17, 127.96) * mm, "end": v(5965.17, 77.16) * mm});
            skLineSegment(sketch, "E11.2.6.1", {"start": v(5914.37, 77.16) * mm, "end": v(5965.17, 77.16) * mm});
            skLineSegment(sketch, "E11.2.6.2", {"start": v(5914.37, 127.96) * mm, "end": v(5914.37, 77.16) * mm});
            skLineSegment(sketch, "E11.2.6.3", {"start": v(5914.37, 127.96) * mm, "end": v(5965.17, 127.96) * mm});
            skLineSegment(sketch, "E11.2.7.0", {"start": v(5965.17, 64.46) * mm, "end": v(5965.17, 13.66) * mm});
            skLineSegment(sketch, "E11.2.7.1", {"start": v(5914.37, 13.66) * mm, "end": v(5965.17, 13.66) * mm});
            skLineSegment(sketch, "E11.2.7.2", {"start": v(5914.37, 64.46) * mm, "end": v(5914.37, 13.66) * mm});
            skLineSegment(sketch, "E11.2.7.3", {"start": v(5914.37, 64.46) * mm, "end": v(5965.17, 64.46) * mm});
            skLineSegment(sketch, "E11.3.0.0", {"start": v(6028.67, 508.96) * mm, "end": v(6028.67, 458.16) * mm});
            skLineSegment(sketch, "E11.3.0.1", {"start": v(5977.87, 458.16) * mm, "end": v(6028.67, 458.16) * mm});
            skLineSegment(sketch, "E11.3.0.2", {"start": v(5977.87, 508.96) * mm, "end": v(5977.87, 458.16) * mm});
            skLineSegment(sketch, "E11.3.0.3", {"start": v(5977.87, 508.96) * mm, "end": v(6028.67, 508.96) * mm});
            skLineSegment(sketch, "E11.3.1.0", {"start": v(6028.67, 445.46) * mm, "end": v(6028.67, 394.66) * mm});
            skLineSegment(sketch, "E11.3.1.1", {"start": v(5977.87, 394.66) * mm, "end": v(6028.67, 394.66) * mm});
            skLineSegment(sketch, "E11.3.1.2", {"start": v(5977.87, 445.46) * mm, "end": v(5977.87, 394.66) * mm});
            skLineSegment(sketch, "E11.3.1.3", {"start": v(5977.87, 445.46) * mm, "end": v(6028.67, 445.46) * mm});
            skLineSegment(sketch, "E11.3.2.0", {"start": v(6028.67, 381.96) * mm, "end": v(6028.67, 331.16) * mm});
            skLineSegment(sketch, "E11.3.2.1", {"start": v(5977.87, 331.16) * mm, "end": v(6028.67, 331.16) * mm});
            skLineSegment(sketch, "E11.3.2.2", {"start": v(5977.87, 381.96) * mm, "end": v(5977.87, 331.16) * mm});
            skLineSegment(sketch, "E11.3.2.3", {"start": v(5977.87, 381.96) * mm, "end": v(6028.67, 381.96) * mm});
            skLineSegment(sketch, "E11.3.3.0", {"start": v(6028.67, 318.46) * mm, "end": v(6028.67, 267.66) * mm});
            skLineSegment(sketch, "E11.3.3.1", {"start": v(5977.87, 267.66) * mm, "end": v(6028.67, 267.66) * mm});
            skLineSegment(sketch, "E11.3.3.2", {"start": v(5977.87, 318.46) * mm, "end": v(5977.87, 267.66) * mm});
            skLineSegment(sketch, "E11.3.3.3", {"start": v(5977.87, 318.46) * mm, "end": v(6028.67, 318.46) * mm});
            skLineSegment(sketch, "E11.3.4.0", {"start": v(6028.67, 254.96) * mm, "end": v(6028.67, 204.16) * mm});
            skLineSegment(sketch, "E11.3.4.1", {"start": v(5977.87, 204.16) * mm, "end": v(6028.67, 204.16) * mm});
            skLineSegment(sketch, "E11.3.4.2", {"start": v(5977.87, 254.96) * mm, "end": v(5977.87, 204.16) * mm});
            skLineSegment(sketch, "E11.3.4.3", {"start": v(5977.87, 254.96) * mm, "end": v(6028.67, 254.96) * mm});
            skLineSegment(sketch, "E11.3.5.0", {"start": v(6028.67, 191.46) * mm, "end": v(6028.67, 140.66) * mm});
            skLineSegment(sketch, "E11.3.5.1", {"start": v(5977.87, 140.66) * mm, "end": v(6028.67, 140.66) * mm});
            skLineSegment(sketch, "E11.3.5.2", {"start": v(5977.87, 191.46) * mm, "end": v(5977.87, 140.66) * mm});
            skLineSegment(sketch, "E11.3.5.3", {"start": v(5977.87, 191.46) * mm, "end": v(6028.67, 191.46) * mm});
            skLineSegment(sketch, "E11.3.6.0", {"start": v(6028.67, 127.96) * mm, "end": v(6028.67, 77.16) * mm});
            skLineSegment(sketch, "E11.3.6.1", {"start": v(5977.87, 77.16) * mm, "end": v(6028.67, 77.16) * mm});
            skLineSegment(sketch, "E11.3.6.2", {"start": v(5977.87, 127.96) * mm, "end": v(5977.87, 77.16) * mm});
            skLineSegment(sketch, "E11.3.6.3", {"start": v(5977.87, 127.96) * mm, "end": v(6028.67, 127.96) * mm});
            skLineSegment(sketch, "E11.3.7.0", {"start": v(6028.67, 64.46) * mm, "end": v(6028.67, 13.66) * mm});
            skLineSegment(sketch, "E11.3.7.1", {"start": v(5977.87, 13.66) * mm, "end": v(6028.67, 13.66) * mm});
            skLineSegment(sketch, "E11.3.7.2", {"start": v(5977.87, 64.46) * mm, "end": v(5977.87, 13.66) * mm});
            skLineSegment(sketch, "E11.3.7.3", {"start": v(5977.87, 64.46) * mm, "end": v(6028.67, 64.46) * mm});
            skLineSegment(sketch, "E11.4.0.0", {"start": v(6092.17, 508.96) * mm, "end": v(6092.17, 458.16) * mm});
            skLineSegment(sketch, "E11.4.0.1", {"start": v(6041.37, 458.16) * mm, "end": v(6092.17, 458.16) * mm});
            skLineSegment(sketch, "E11.4.0.2", {"start": v(6041.37, 508.96) * mm, "end": v(6041.37, 458.16) * mm});
            skLineSegment(sketch, "E11.4.0.3", {"start": v(6041.37, 508.96) * mm, "end": v(6092.17, 508.96) * mm});
            skLineSegment(sketch, "E11.4.1.0", {"start": v(6092.17, 445.46) * mm, "end": v(6092.17, 394.66) * mm});
            skLineSegment(sketch, "E11.4.1.1", {"start": v(6041.37, 394.66) * mm, "end": v(6092.17, 394.66) * mm});
            skLineSegment(sketch, "E11.4.1.2", {"start": v(6041.37, 445.46) * mm, "end": v(6041.37, 394.66) * mm});
            skLineSegment(sketch, "E11.4.1.3", {"start": v(6041.37, 445.46) * mm, "end": v(6092.17, 445.46) * mm});
            skLineSegment(sketch, "E11.4.2.0", {"start": v(6092.17, 381.96) * mm, "end": v(6092.17, 331.16) * mm});
            skLineSegment(sketch, "E11.4.2.1", {"start": v(6041.37, 331.16) * mm, "end": v(6092.17, 331.16) * mm});
            skLineSegment(sketch, "E11.4.2.2", {"start": v(6041.37, 381.96) * mm, "end": v(6041.37, 331.16) * mm});
            skLineSegment(sketch, "E11.4.2.3", {"start": v(6041.37, 381.96) * mm, "end": v(6092.17, 381.96) * mm});
            skLineSegment(sketch, "E11.4.3.0", {"start": v(6092.17, 318.46) * mm, "end": v(6092.17, 267.66) * mm});
            skLineSegment(sketch, "E11.4.3.1", {"start": v(6041.37, 267.66) * mm, "end": v(6092.17, 267.66) * mm});
            skLineSegment(sketch, "E11.4.3.2", {"start": v(6041.37, 318.46) * mm, "end": v(6041.37, 267.66) * mm});
            skLineSegment(sketch, "E11.4.3.3", {"start": v(6041.37, 318.46) * mm, "end": v(6092.17, 318.46) * mm});
            skLineSegment(sketch, "E11.4.4.0", {"start": v(6092.17, 254.96) * mm, "end": v(6092.17, 204.16) * mm});
            skLineSegment(sketch, "E11.4.4.1", {"start": v(6041.37, 204.16) * mm, "end": v(6092.17, 204.16) * mm});
            skLineSegment(sketch, "E11.4.4.2", {"start": v(6041.37, 254.96) * mm, "end": v(6041.37, 204.16) * mm});
            skLineSegment(sketch, "E11.4.4.3", {"start": v(6041.37, 254.96) * mm, "end": v(6092.17, 254.96) * mm});
            skLineSegment(sketch, "E11.4.5.0", {"start": v(6092.17, 191.46) * mm, "end": v(6092.17, 140.66) * mm});
            skLineSegment(sketch, "E11.4.5.1", {"start": v(6041.37, 140.66) * mm, "end": v(6092.17, 140.66) * mm});
            skLineSegment(sketch, "E11.4.5.2", {"start": v(6041.37, 191.46) * mm, "end": v(6041.37, 140.66) * mm});
            skLineSegment(sketch, "E11.4.5.3", {"start": v(6041.37, 191.46) * mm, "end": v(6092.17, 191.46) * mm});
            skLineSegment(sketch, "E11.4.6.0", {"start": v(6092.17, 127.96) * mm, "end": v(6092.17, 77.16) * mm});
            skLineSegment(sketch, "E11.4.6.1", {"start": v(6041.37, 77.16) * mm, "end": v(6092.17, 77.16) * mm});
            skLineSegment(sketch, "E11.4.6.2", {"start": v(6041.37, 127.96) * mm, "end": v(6041.37, 77.16) * mm});
            skLineSegment(sketch, "E11.4.6.3", {"start": v(6041.37, 127.96) * mm, "end": v(6092.17, 127.96) * mm});
            skLineSegment(sketch, "E11.4.7.0", {"start": v(6092.17, 64.46) * mm, "end": v(6092.17, 13.66) * mm});
            skLineSegment(sketch, "E11.4.7.1", {"start": v(6041.37, 13.66) * mm, "end": v(6092.17, 13.66) * mm});
            skLineSegment(sketch, "E11.4.7.2", {"start": v(6041.37, 64.46) * mm, "end": v(6041.37, 13.66) * mm});
            skLineSegment(sketch, "E11.4.7.3", {"start": v(6041.37, 64.46) * mm, "end": v(6092.17, 64.46) * mm});
            skLineSegment(sketch, "E11.5.0.0", {"start": v(6155.67, 508.96) * mm, "end": v(6155.67, 458.16) * mm});
            skLineSegment(sketch, "E11.5.0.1", {"start": v(6104.87, 458.16) * mm, "end": v(6155.67, 458.16) * mm});
            skLineSegment(sketch, "E11.5.0.2", {"start": v(6104.87, 508.96) * mm, "end": v(6104.87, 458.16) * mm});
            skLineSegment(sketch, "E11.5.0.3", {"start": v(6104.87, 508.96) * mm, "end": v(6155.67, 508.96) * mm});
            skLineSegment(sketch, "E11.5.1.0", {"start": v(6155.67, 445.46) * mm, "end": v(6155.67, 394.66) * mm});
            skLineSegment(sketch, "E11.5.1.1", {"start": v(6104.87, 394.66) * mm, "end": v(6155.67, 394.66) * mm});
            skLineSegment(sketch, "E11.5.1.2", {"start": v(6104.87, 445.46) * mm, "end": v(6104.87, 394.66) * mm});
            skLineSegment(sketch, "E11.5.1.3", {"start": v(6104.87, 445.46) * mm, "end": v(6155.67, 445.46) * mm});
            skLineSegment(sketch, "E11.5.2.0", {"start": v(6155.67, 381.96) * mm, "end": v(6155.67, 331.16) * mm});
            skLineSegment(sketch, "E11.5.2.1", {"start": v(6104.87, 331.16) * mm, "end": v(6155.67, 331.16) * mm});
            skLineSegment(sketch, "E11.5.2.2", {"start": v(6104.87, 381.96) * mm, "end": v(6104.87, 331.16) * mm});
            skLineSegment(sketch, "E11.5.2.3", {"start": v(6104.87, 381.96) * mm, "end": v(6155.67, 381.96) * mm});
            skLineSegment(sketch, "E11.5.3.0", {"start": v(6155.67, 318.46) * mm, "end": v(6155.67, 267.66) * mm});
            skLineSegment(sketch, "E11.5.3.1", {"start": v(6104.87, 267.66) * mm, "end": v(6155.67, 267.66) * mm});
            skLineSegment(sketch, "E11.5.3.2", {"start": v(6104.87, 318.46) * mm, "end": v(6104.87, 267.66) * mm});
            skLineSegment(sketch, "E11.5.3.3", {"start": v(6104.87, 318.46) * mm, "end": v(6155.67, 318.46) * mm});
            skLineSegment(sketch, "E11.5.4.0", {"start": v(6155.67, 254.96) * mm, "end": v(6155.67, 204.16) * mm});
            skLineSegment(sketch, "E11.5.4.1", {"start": v(6104.87, 204.16) * mm, "end": v(6155.67, 204.16) * mm});
            skLineSegment(sketch, "E11.5.4.2", {"start": v(6104.87, 254.96) * mm, "end": v(6104.87, 204.16) * mm});
            skLineSegment(sketch, "E11.5.4.3", {"start": v(6104.87, 254.96) * mm, "end": v(6155.67, 254.96) * mm});
            skLineSegment(sketch, "E11.5.5.0", {"start": v(6155.67, 191.46) * mm, "end": v(6155.67, 140.66) * mm});
            skLineSegment(sketch, "E11.5.5.1", {"start": v(6104.87, 140.66) * mm, "end": v(6155.67, 140.66) * mm});
            skLineSegment(sketch, "E11.5.5.2", {"start": v(6104.87, 191.46) * mm, "end": v(6104.87, 140.66) * mm});
            skLineSegment(sketch, "E11.5.5.3", {"start": v(6104.87, 191.46) * mm, "end": v(6155.67, 191.46) * mm});
            skLineSegment(sketch, "E11.5.6.0", {"start": v(6155.67, 127.96) * mm, "end": v(6155.67, 77.16) * mm});
            skLineSegment(sketch, "E11.5.6.1", {"start": v(6104.87, 77.16) * mm, "end": v(6155.67, 77.16) * mm});
            skLineSegment(sketch, "E11.5.6.2", {"start": v(6104.87, 127.96) * mm, "end": v(6104.87, 77.16) * mm});
            skLineSegment(sketch, "E11.5.6.3", {"start": v(6104.87, 127.96) * mm, "end": v(6155.67, 127.96) * mm});
            skLineSegment(sketch, "E11.5.7.0", {"start": v(6155.67, 64.46) * mm, "end": v(6155.67, 13.66) * mm});
            skLineSegment(sketch, "E11.5.7.1", {"start": v(6104.87, 13.66) * mm, "end": v(6155.67, 13.66) * mm});
            skLineSegment(sketch, "E11.5.7.2", {"start": v(6104.87, 64.46) * mm, "end": v(6104.87, 13.66) * mm});
            skLineSegment(sketch, "E11.5.7.3", {"start": v(6104.87, 64.46) * mm, "end": v(6155.67, 64.46) * mm});
            skLineSegment(sketch, "E11.6.0.0", {"start": v(6219.17, 508.96) * mm, "end": v(6219.17, 458.16) * mm});
            skLineSegment(sketch, "E11.6.0.1", {"start": v(6168.37, 458.16) * mm, "end": v(6219.17, 458.16) * mm});
            skLineSegment(sketch, "E11.6.0.2", {"start": v(6168.37, 508.96) * mm, "end": v(6168.37, 458.16) * mm});
            skLineSegment(sketch, "E11.6.0.3", {"start": v(6168.37, 508.96) * mm, "end": v(6219.17, 508.96) * mm});
            skLineSegment(sketch, "E11.6.1.0", {"start": v(6219.17, 445.46) * mm, "end": v(6219.17, 394.66) * mm});
            skLineSegment(sketch, "E11.6.1.1", {"start": v(6168.37, 394.66) * mm, "end": v(6219.17, 394.66) * mm});
            skLineSegment(sketch, "E11.6.1.2", {"start": v(6168.37, 445.46) * mm, "end": v(6168.37, 394.66) * mm});
            skLineSegment(sketch, "E11.6.1.3", {"start": v(6168.37, 445.46) * mm, "end": v(6219.17, 445.46) * mm});
            skLineSegment(sketch, "E11.6.2.0", {"start": v(6219.17, 381.96) * mm, "end": v(6219.17, 331.16) * mm});
            skLineSegment(sketch, "E11.6.2.1", {"start": v(6168.37, 331.16) * mm, "end": v(6219.17, 331.16) * mm});
            skLineSegment(sketch, "E11.6.2.2", {"start": v(6168.37, 381.96) * mm, "end": v(6168.37, 331.16) * mm});
            skLineSegment(sketch, "E11.6.2.3", {"start": v(6168.37, 381.96) * mm, "end": v(6219.17, 381.96) * mm});
            skLineSegment(sketch, "E11.6.3.0", {"start": v(6219.17, 318.46) * mm, "end": v(6219.17, 267.66) * mm});
            skLineSegment(sketch, "E11.6.3.1", {"start": v(6168.37, 267.66) * mm, "end": v(6219.17, 267.66) * mm});
            skLineSegment(sketch, "E11.6.3.2", {"start": v(6168.37, 318.46) * mm, "end": v(6168.37, 267.66) * mm});
            skLineSegment(sketch, "E11.6.3.3", {"start": v(6168.37, 318.46) * mm, "end": v(6219.17, 318.46) * mm});
            skLineSegment(sketch, "E11.6.4.0", {"start": v(6219.17, 254.96) * mm, "end": v(6219.17, 204.16) * mm});
            skLineSegment(sketch, "E11.6.4.1", {"start": v(6168.37, 204.16) * mm, "end": v(6219.17, 204.16) * mm});
            skLineSegment(sketch, "E11.6.4.2", {"start": v(6168.37, 254.96) * mm, "end": v(6168.37, 204.16) * mm});
            skLineSegment(sketch, "E11.6.4.3", {"start": v(6168.37, 254.96) * mm, "end": v(6219.17, 254.96) * mm});
            skLineSegment(sketch, "E11.6.5.0", {"start": v(6219.17, 191.46) * mm, "end": v(6219.17, 140.66) * mm});
            skLineSegment(sketch, "E11.6.5.1", {"start": v(6168.37, 140.66) * mm, "end": v(6219.17, 140.66) * mm});
            skLineSegment(sketch, "E11.6.5.2", {"start": v(6168.37, 191.46) * mm, "end": v(6168.37, 140.66) * mm});
            skLineSegment(sketch, "E11.6.5.3", {"start": v(6168.37, 191.46) * mm, "end": v(6219.17, 191.46) * mm});
            skLineSegment(sketch, "E11.6.6.0", {"start": v(6219.17, 127.96) * mm, "end": v(6219.17, 77.16) * mm});
            skLineSegment(sketch, "E11.6.6.1", {"start": v(6168.37, 77.16) * mm, "end": v(6219.17, 77.16) * mm});
            skLineSegment(sketch, "E11.6.6.2", {"start": v(6168.37, 127.96) * mm, "end": v(6168.37, 77.16) * mm});
            skLineSegment(sketch, "E11.6.6.3", {"start": v(6168.37, 127.96) * mm, "end": v(6219.17, 127.96) * mm});
            skLineSegment(sketch, "E11.6.7.0", {"start": v(6219.17, 64.46) * mm, "end": v(6219.17, 13.66) * mm});
            skLineSegment(sketch, "E11.6.7.1", {"start": v(6168.37, 13.66) * mm, "end": v(6219.17, 13.66) * mm});
            skLineSegment(sketch, "E11.6.7.2", {"start": v(6168.37, 64.46) * mm, "end": v(6168.37, 13.66) * mm});
            skLineSegment(sketch, "E11.6.7.3", {"start": v(6168.37, 64.46) * mm, "end": v(6219.17, 64.46) * mm});
            skLineSegment(sketch, "E11.7.0.0", {"start": v(6282.67, 508.96) * mm, "end": v(6282.67, 458.16) * mm});
            skLineSegment(sketch, "E11.7.0.1", {"start": v(6231.87, 458.16) * mm, "end": v(6282.67, 458.16) * mm});
            skLineSegment(sketch, "E11.7.0.2", {"start": v(6231.87, 508.96) * mm, "end": v(6231.87, 458.16) * mm});
            skLineSegment(sketch, "E11.7.0.3", {"start": v(6231.87, 508.96) * mm, "end": v(6282.67, 508.96) * mm});
            skLineSegment(sketch, "E11.7.1.0", {"start": v(6282.67, 445.46) * mm, "end": v(6282.67, 394.66) * mm});
            skLineSegment(sketch, "E11.7.1.1", {"start": v(6231.87, 394.66) * mm, "end": v(6282.67, 394.66) * mm});
            skLineSegment(sketch, "E11.7.1.2", {"start": v(6231.87, 445.46) * mm, "end": v(6231.87, 394.66) * mm});
            skLineSegment(sketch, "E11.7.1.3", {"start": v(6231.87, 445.46) * mm, "end": v(6282.67, 445.46) * mm});
            skLineSegment(sketch, "E11.7.2.0", {"start": v(6282.67, 381.96) * mm, "end": v(6282.67, 331.16) * mm});
            skLineSegment(sketch, "E11.7.2.1", {"start": v(6231.87, 331.16) * mm, "end": v(6282.67, 331.16) * mm});
            skLineSegment(sketch, "E11.7.2.2", {"start": v(6231.87, 381.96) * mm, "end": v(6231.87, 331.16) * mm});
            skLineSegment(sketch, "E11.7.2.3", {"start": v(6231.87, 381.96) * mm, "end": v(6282.67, 381.96) * mm});
            skLineSegment(sketch, "E11.7.3.0", {"start": v(6282.67, 318.46) * mm, "end": v(6282.67, 267.66) * mm});
            skLineSegment(sketch, "E11.7.3.1", {"start": v(6231.87, 267.66) * mm, "end": v(6282.67, 267.66) * mm});
            skLineSegment(sketch, "E11.7.3.2", {"start": v(6231.87, 318.46) * mm, "end": v(6231.87, 267.66) * mm});
            skLineSegment(sketch, "E11.7.3.3", {"start": v(6231.87, 318.46) * mm, "end": v(6282.67, 318.46) * mm});
            skLineSegment(sketch, "E11.7.4.0", {"start": v(6282.67, 254.96) * mm, "end": v(6282.67, 204.16) * mm});
            skLineSegment(sketch, "E11.7.4.1", {"start": v(6231.87, 204.16) * mm, "end": v(6282.67, 204.16) * mm});
            skLineSegment(sketch, "E11.7.4.2", {"start": v(6231.87, 254.96) * mm, "end": v(6231.87, 204.16) * mm});
            skLineSegment(sketch, "E11.7.4.3", {"start": v(6231.87, 254.96) * mm, "end": v(6282.67, 254.96) * mm});
            skLineSegment(sketch, "E11.7.5.0", {"start": v(6282.67, 191.46) * mm, "end": v(6282.67, 140.66) * mm});
            skLineSegment(sketch, "E11.7.5.1", {"start": v(6231.87, 140.66) * mm, "end": v(6282.67, 140.66) * mm});
            skLineSegment(sketch, "E11.7.5.2", {"start": v(6231.87, 191.46) * mm, "end": v(6231.87, 140.66) * mm});
            skLineSegment(sketch, "E11.7.5.3", {"start": v(6231.87, 191.46) * mm, "end": v(6282.67, 191.46) * mm});
            skLineSegment(sketch, "E11.7.6.0", {"start": v(6282.67, 127.96) * mm, "end": v(6282.67, 77.16) * mm});
            skLineSegment(sketch, "E11.7.6.1", {"start": v(6231.87, 77.16) * mm, "end": v(6282.67, 77.16) * mm});
            skLineSegment(sketch, "E11.7.6.2", {"start": v(6231.87, 127.96) * mm, "end": v(6231.87, 77.16) * mm});
            skLineSegment(sketch, "E11.7.6.3", {"start": v(6231.87, 127.96) * mm, "end": v(6282.67, 127.96) * mm});
            skLineSegment(sketch, "E11.7.7.0", {"start": v(6282.67, 64.46) * mm, "end": v(6282.67, 13.66) * mm});
            skLineSegment(sketch, "E11.7.7.1", {"start": v(6231.87, 13.66) * mm, "end": v(6282.67, 13.66) * mm});
            skLineSegment(sketch, "E11.7.7.2", {"start": v(6231.87, 64.46) * mm, "end": v(6231.87, 13.66) * mm});
            skLineSegment(sketch, "E11.7.7.3", {"start": v(6231.87, 64.46) * mm, "end": v(6282.67, 64.46) * mm});
            skLineSegment(sketch, "E11.8.0.0", {"start": v(6346.17, 508.96) * mm, "end": v(6346.17, 458.16) * mm});
            skLineSegment(sketch, "E11.8.0.1", {"start": v(6295.37, 458.16) * mm, "end": v(6346.17, 458.16) * mm});
            skLineSegment(sketch, "E11.8.0.2", {"start": v(6295.37, 508.96) * mm, "end": v(6295.37, 458.16) * mm});
            skLineSegment(sketch, "E11.8.0.3", {"start": v(6295.37, 508.96) * mm, "end": v(6346.17, 508.96) * mm});
            skLineSegment(sketch, "E11.8.1.0", {"start": v(6346.17, 445.46) * mm, "end": v(6346.17, 394.66) * mm});
            skLineSegment(sketch, "E11.8.1.1", {"start": v(6295.37, 394.66) * mm, "end": v(6346.17, 394.66) * mm});
            skLineSegment(sketch, "E11.8.1.2", {"start": v(6295.37, 445.46) * mm, "end": v(6295.37, 394.66) * mm});
            skLineSegment(sketch, "E11.8.1.3", {"start": v(6295.37, 445.46) * mm, "end": v(6346.17, 445.46) * mm});
            skLineSegment(sketch, "E11.8.2.0", {"start": v(6346.17, 381.96) * mm, "end": v(6346.17, 331.16) * mm});
            skLineSegment(sketch, "E11.8.2.1", {"start": v(6295.37, 331.16) * mm, "end": v(6346.17, 331.16) * mm});
            skLineSegment(sketch, "E11.8.2.2", {"start": v(6295.37, 381.96) * mm, "end": v(6295.37, 331.16) * mm});
            skLineSegment(sketch, "E11.8.2.3", {"start": v(6295.37, 381.96) * mm, "end": v(6346.17, 381.96) * mm});
            skLineSegment(sketch, "E11.8.3.0", {"start": v(6346.17, 318.46) * mm, "end": v(6346.17, 267.66) * mm});
            skLineSegment(sketch, "E11.8.3.1", {"start": v(6295.37, 267.66) * mm, "end": v(6346.17, 267.66) * mm});
            skLineSegment(sketch, "E11.8.3.2", {"start": v(6295.37, 318.46) * mm, "end": v(6295.37, 267.66) * mm});
            skLineSegment(sketch, "E11.8.3.3", {"start": v(6295.37, 318.46) * mm, "end": v(6346.17, 318.46) * mm});
            skLineSegment(sketch, "E11.8.4.0", {"start": v(6346.17, 254.96) * mm, "end": v(6346.17, 204.16) * mm});
            skLineSegment(sketch, "E11.8.4.1", {"start": v(6295.37, 204.16) * mm, "end": v(6346.17, 204.16) * mm});
            skLineSegment(sketch, "E11.8.4.2", {"start": v(6295.37, 254.96) * mm, "end": v(6295.37, 204.16) * mm});
            skLineSegment(sketch, "E11.8.4.3", {"start": v(6295.37, 254.96) * mm, "end": v(6346.17, 254.96) * mm});
            skLineSegment(sketch, "E11.8.5.0", {"start": v(6346.17, 191.46) * mm, "end": v(6346.17, 140.66) * mm});
            skLineSegment(sketch, "E11.8.5.1", {"start": v(6295.37, 140.66) * mm, "end": v(6346.17, 140.66) * mm});
            skLineSegment(sketch, "E11.8.5.2", {"start": v(6295.37, 191.46) * mm, "end": v(6295.37, 140.66) * mm});
            skLineSegment(sketch, "E11.8.5.3", {"start": v(6295.37, 191.46) * mm, "end": v(6346.17, 191.46) * mm});
            skLineSegment(sketch, "E11.8.6.0", {"start": v(6346.17, 127.96) * mm, "end": v(6346.17, 77.16) * mm});
            skLineSegment(sketch, "E11.8.6.1", {"start": v(6295.37, 77.16) * mm, "end": v(6346.17, 77.16) * mm});
            skLineSegment(sketch, "E11.8.6.2", {"start": v(6295.37, 127.96) * mm, "end": v(6295.37, 77.16) * mm});
            skLineSegment(sketch, "E11.8.6.3", {"start": v(6295.37, 127.96) * mm, "end": v(6346.17, 127.96) * mm});
            skLineSegment(sketch, "E11.8.7.0", {"start": v(6346.17, 64.46) * mm, "end": v(6346.17, 13.66) * mm});
            skLineSegment(sketch, "E11.8.7.1", {"start": v(6295.37, 13.66) * mm, "end": v(6346.17, 13.66) * mm});
            skLineSegment(sketch, "E11.8.7.2", {"start": v(6295.37, 64.46) * mm, "end": v(6295.37, 13.66) * mm});
            skLineSegment(sketch, "E11.8.7.3", {"start": v(6295.37, 64.46) * mm, "end": v(6346.17, 64.46) * mm});
            skLineSegment(sketch, "E11.9.0.0", {"start": v(6409.67, 508.96) * mm, "end": v(6409.67, 458.16) * mm});
            skLineSegment(sketch, "E11.9.0.1", {"start": v(6358.87, 458.16) * mm, "end": v(6409.67, 458.16) * mm});
            skLineSegment(sketch, "E11.9.0.2", {"start": v(6358.87, 508.96) * mm, "end": v(6358.87, 458.16) * mm});
            skLineSegment(sketch, "E11.9.0.3", {"start": v(6358.87, 508.96) * mm, "end": v(6409.67, 508.96) * mm});
            skLineSegment(sketch, "E11.9.1.0", {"start": v(6409.67, 445.46) * mm, "end": v(6409.67, 394.66) * mm});
            skLineSegment(sketch, "E11.9.1.1", {"start": v(6358.87, 394.66) * mm, "end": v(6409.67, 394.66) * mm});
            skLineSegment(sketch, "E11.9.1.2", {"start": v(6358.87, 445.46) * mm, "end": v(6358.87, 394.66) * mm});
            skLineSegment(sketch, "E11.9.1.3", {"start": v(6358.87, 445.46) * mm, "end": v(6409.67, 445.46) * mm});
            skLineSegment(sketch, "E11.9.2.0", {"start": v(6409.67, 381.96) * mm, "end": v(6409.67, 331.16) * mm});
            skLineSegment(sketch, "E11.9.2.1", {"start": v(6358.87, 331.16) * mm, "end": v(6409.67, 331.16) * mm});
            skLineSegment(sketch, "E11.9.2.2", {"start": v(6358.87, 381.96) * mm, "end": v(6358.87, 331.16) * mm});
            skLineSegment(sketch, "E11.9.2.3", {"start": v(6358.87, 381.96) * mm, "end": v(6409.67, 381.96) * mm});
            skLineSegment(sketch, "E11.9.3.0", {"start": v(6409.67, 318.46) * mm, "end": v(6409.67, 267.66) * mm});
            skLineSegment(sketch, "E11.9.3.1", {"start": v(6358.87, 267.66) * mm, "end": v(6409.67, 267.66) * mm});
            skLineSegment(sketch, "E11.9.3.2", {"start": v(6358.87, 318.46) * mm, "end": v(6358.87, 267.66) * mm});
            skLineSegment(sketch, "E11.9.3.3", {"start": v(6358.87, 318.46) * mm, "end": v(6409.67, 318.46) * mm});
            skLineSegment(sketch, "E11.9.4.0", {"start": v(6409.67, 254.96) * mm, "end": v(6409.67, 204.16) * mm});
            skLineSegment(sketch, "E11.9.4.1", {"start": v(6358.87, 204.16) * mm, "end": v(6409.67, 204.16) * mm});
            skLineSegment(sketch, "E11.9.4.2", {"start": v(6358.87, 254.96) * mm, "end": v(6358.87, 204.16) * mm});
            skLineSegment(sketch, "E11.9.4.3", {"start": v(6358.87, 254.96) * mm, "end": v(6409.67, 254.96) * mm});
            skLineSegment(sketch, "E11.9.5.0", {"start": v(6409.67, 191.46) * mm, "end": v(6409.67, 140.66) * mm});
            skLineSegment(sketch, "E11.9.5.1", {"start": v(6358.87, 140.66) * mm, "end": v(6409.67, 140.66) * mm});
            skLineSegment(sketch, "E11.9.5.2", {"start": v(6358.87, 191.46) * mm, "end": v(6358.87, 140.66) * mm});
            skLineSegment(sketch, "E11.9.5.3", {"start": v(6358.87, 191.46) * mm, "end": v(6409.67, 191.46) * mm});
            skLineSegment(sketch, "E11.9.6.0", {"start": v(6409.67, 127.96) * mm, "end": v(6409.67, 77.16) * mm});
            skLineSegment(sketch, "E11.9.6.1", {"start": v(6358.87, 77.16) * mm, "end": v(6409.67, 77.16) * mm});
            skLineSegment(sketch, "E11.9.6.2", {"start": v(6358.87, 127.96) * mm, "end": v(6358.87, 77.16) * mm});
            skLineSegment(sketch, "E11.9.6.3", {"start": v(6358.87, 127.96) * mm, "end": v(6409.67, 127.96) * mm});
            skLineSegment(sketch, "E11.9.7.0", {"start": v(6409.67, 64.46) * mm, "end": v(6409.67, 13.66) * mm});
            skLineSegment(sketch, "E11.9.7.1", {"start": v(6358.87, 13.66) * mm, "end": v(6409.67, 13.66) * mm});
            skLineSegment(sketch, "E11.9.7.2", {"start": v(6358.87, 64.46) * mm, "end": v(6358.87, 13.66) * mm});
            skLineSegment(sketch, "E11.9.7.3", {"start": v(6358.87, 64.46) * mm, "end": v(6409.67, 64.46) * mm});
            skLineSegment(sketch, "E11.direction1", {"start": v(5838.17, 458.16) * mm, "end": v(5901.67, 458.16) * mm, "construction": true});
            skLineSegment(sketch, "E11.direction2", {"start": v(5838.17, 458.16) * mm, "end": v(5838.17, 394.66) * mm, "construction": true});
            skSolve(sketch);
        }
        {
            var Q0;
            Q0 = qSketchRegion(id + "F11", true);
            extrude(context, id + "F12", {"entities" : qUnion([Q0]), "operationType" : NewBodyOperationType.REMOVE, "endBound" : BoundingType.THROUGH_ALL, "oppositeDirection" : true, "depth" : 25.4 * mm});
        }
        {
            var Q0;
            Q0=makeQuery(id+"F4.boolean.opBoolean","MERGE",FACE,{"derivedFrom":[makeQuery(id+"F3.boolean.opBoolean","MERGE",FACE,{"derivedFrom":[makeQuery(id+"F2.opExtrude","SWEPT_FACE",FACE,{"disambiguationData":[OSD([sQuery(id+"F0.wireOp",EDGE,"E1.bottom")])]}),makeQuery(id+"F3.opExtrude","SWEPT_FACE",FACE,{"disambiguationData":[OSD([sQuery(id+"F0.wireOp",EDGE,"E2.bottom")])]})]}),makeQuery(id+"F4.opExtrude","SWEPT_FACE",FACE,{"disambiguationData":[OSD([sQuery(id+"F0.wireOp",EDGE,"E3.bottom")])]})]});
            var sketch = newSketch(context, id + "F13", { "sketchPlane" : qUnion([Q0])});
            skLineSegment(sketch, "E12.bottom", {"start": v(5738.72, 2438.4) * mm, "end": v(5756.88, 2438.4) * mm});
            skLineSegment(sketch, "E12.top", {"start": v(5738.72, 0) * mm, "end": v(5756.88, 0) * mm});
            skLineSegment(sketch, "E12.left", {"start": v(5738.72, 2438.4) * mm, "end": v(5738.72, 0) * mm});
            skLineSegment(sketch, "E12.right", {"start": v(5756.88, 2438.4) * mm, "end": v(5756.88, 0) * mm});
            skSolve(sketch);
        }
        {
            var Q0;
            Q0 = qSketchRegion(id + "F13", true);
            extrude(context, id + "F14", {"entities" : qUnion([Q0]), "operationType" : NewBodyOperationType.REMOVE, "oppositeDirection" : true, "depth" : 25.4 * mm});
        }
        {
            var Q0;
            {var subQ1=sQuery(id+"F0.wireOp",EDGE,"E2.right");var subQ4=sQuery(id+"F0.wireOp",EDGE,"E2.bottom");var subQ6=sQuery(id+"F0.wireOp",EDGE,"E3.bottom");var subQ7=sQuery(id+"F0.wireOp",EDGE,"E1.bottom");Q0=makeQuery(id+"F14.boolean.opBoolean","SPLIT",FACE,{"disambiguationData":[TD([makeQuery(id+"F4.opExtrude","SWEPT_FACE",FACE,{"disambiguationData":[OSD([subQ1])]})])],"derivedFrom":makeQuery(id+"F4.boolean.opBoolean","MERGE",FACE,{"derivedFrom":[makeQuery(id+"F3.boolean.opBoolean","MERGE",FACE,{"derivedFrom":[makeQuery(id+"F2.opExtrude","SWEPT_FACE",FACE,{"disambiguationData":[OSD([subQ7])]}),makeQuery(id+"F3.opExtrude","SWEPT_FACE",FACE,{"disambiguationData":[OSD([subQ4])]})]}),makeQuery(id+"F4.opExtrude","SWEPT_FACE",FACE,{"disambiguationData":[OSD([subQ6])]})]})});}
            var sketch = newSketch(context, id + "F15", { "sketchPlane" : qUnion([Q0])});
            skLineSegment(sketch, "E13.bottom", {"start": v(8481.92, 2438.4) * mm, "end": v(8461.46, 2438.4) * mm});
            skLineSegment(sketch, "E13.top", {"start": v(8481.92, 0) * mm, "end": v(8461.46, 0) * mm});
            skLineSegment(sketch, "E13.left", {"start": v(8481.92, 2438.4) * mm, "end": v(8481.92, 0) * mm});
            skLineSegment(sketch, "E13.right", {"start": v(8461.46, 2438.4) * mm, "end": v(8461.46, 0) * mm});
            skSolve(sketch);
        }
        {
            var Q0;
            Q0 = qSketchRegion(id + "F15", true);
            extrude(context, id + "F16", {"entities" : qUnion([Q0]), "operationType" : NewBodyOperationType.REMOVE, "oppositeDirection" : true, "depth" : 25.4 * mm});
        }
        {
            var Q0;
            Q0=makeQuery(id+"F4.boolean.opBoolean","MERGE",FACE,{"derivedFrom":[makeQuery(id+"F3.boolean.opBoolean","MERGE",FACE,{"derivedFrom":[makeQuery(id+"F2.opExtrude","SWEPT_FACE",FACE,{"disambiguationData":[OSD([sQuery(id+"F0.wireOp",EDGE,"E1.top")])]}),makeQuery(id+"F3.opExtrude","SWEPT_FACE",FACE,{"disambiguationData":[OSD([sQuery(id+"F0.wireOp",EDGE,"E2.top")])]})]}),makeQuery(id+"F4.opExtrude","SWEPT_FACE",FACE,{"disambiguationData":[OSD([sQuery(id+"F0.wireOp",EDGE,"E3.top")])]})]});
            var sketch = newSketch(context, id + "F17", { "sketchPlane" : qUnion([Q0])});
            skLineSegment(sketch, "E14.bottom", {"start": v(-8481.92, 2438.4) * mm, "end": v(-8447.79, 2438.4) * mm});
            skLineSegment(sketch, "E14.top", {"start": v(-8481.92, 0) * mm, "end": v(-8447.79, 0) * mm});
            skLineSegment(sketch, "E14.left", {"start": v(-8481.92, 2438.4) * mm, "end": v(-8481.92, 0) * mm});
            skLineSegment(sketch, "E14.right", {"start": v(-8447.79, 2438.4) * mm, "end": v(-8447.79, 0) * mm});
            skSolve(sketch);
        }
        {
            var Q0;
            Q0 = qSketchRegion(id + "F17", true);
            extrude(context, id + "F18", {"entities" : qUnion([Q0]), "operationType" : NewBodyOperationType.REMOVE, "oppositeDirection" : true, "depth" : 25.4 * mm});
        }
        {
            var Q0;
            {var subQ2=sQuery(id+"F0.wireOp",EDGE,"E2.top");var subQ4=sQuery(id+"F0.wireOp",EDGE,"E3.top");var subQ5=sQuery(id+"F0.wireOp",EDGE,"E1.left");var subQ6=sQuery(id+"F0.wireOp",EDGE,"E1.top");Q0=makeQuery(id+"F18.boolean.opBoolean","SPLIT",FACE,{"disambiguationData":[TD([makeQuery(id+"F2.opExtrude","SWEPT_FACE",FACE,{"disambiguationData":[OSD([subQ5])]})])],"derivedFrom":makeQuery(id+"F4.boolean.opBoolean","MERGE",FACE,{"derivedFrom":[makeQuery(id+"F3.boolean.opBoolean","MERGE",FACE,{"derivedFrom":[makeQuery(id+"F2.opExtrude","SWEPT_FACE",FACE,{"disambiguationData":[OSD([subQ6])]}),makeQuery(id+"F3.opExtrude","SWEPT_FACE",FACE,{"disambiguationData":[OSD([subQ2])]})]}),makeQuery(id+"F4.opExtrude","SWEPT_FACE",FACE,{"disambiguationData":[OSD([subQ4])]})]})});}
            var sketch = newSketch(context, id + "F19", { "sketchPlane" : qUnion([Q0])});
            skLineSegment(sketch, "E15.bottom", {"start": v(-5738.72, 2438.4) * mm, "end": v(-5757.74, 2438.4) * mm});
            skLineSegment(sketch, "E15.top", {"start": v(-5738.72, 0) * mm, "end": v(-5757.74, 0) * mm});
            skLineSegment(sketch, "E15.left", {"start": v(-5738.72, 2438.4) * mm, "end": v(-5738.72, 0) * mm});
            skLineSegment(sketch, "E15.right", {"start": v(-5757.74, 2438.4) * mm, "end": v(-5757.74, 0) * mm});
            skSolve(sketch);
        }
        {
            var Q0;
            Q0 = qSketchRegion(id + "F19", true);
            extrude(context, id + "F20", {"entities" : qUnion([Q0]), "operationType" : NewBodyOperationType.REMOVE, "oppositeDirection" : true, "depth" : 25.4 * mm});
        }
        {
            var Q0;
            Q0=makeQuery(id+"F4.opExtrude","SWEPT_FACE",FACE,{"disambiguationData":[OSD([sQuery(id+"F0.wireOp",EDGE,"E3.right")])]});
            var sketch = newSketch(context, id + "F21", { "sketchPlane" : qUnion([Q0])});
            skLineSegment(sketch, "E16.bottom", {"start": v(619.8, 0) * mm, "end": v(2651.8, 0) * mm});
            skLineSegment(sketch, "E16.left", {"start": v(619.8, 0) * mm, "end": v(619.8, 1828.8) * mm});
            skLineSegment(sketch, "E16.right", {"start": v(2651.8, 0) * mm, "end": v(2651.8, 1828.8) * mm});
            skLineSegment(sketch, "E17", {"start": v(619.8, 1828.8) * mm, "end": v(2651.8, 1828.8) * mm});
            skSolve(sketch);
        }
        {
            var Q0;
            Q0 = qSketchRegion(id + "F21", true);
            var Q1;
            Q1=makeQuery(id+"F2.opExtrude","SWEPT_FACE",FACE,{"disambiguationData":[OSD([sQuery(id+"F0.wireOp",EDGE,"E1.left")])]});
            extrude(context, id + "F22", {"entities" : qUnion([Q0]), "operationType" : NewBodyOperationType.REMOVE, "endBound" : BoundingType.UP_TO_SURFACE, "oppositeDirection" : true, "endBoundEntityFace" : qUnion([Q1]), "depth" : 25.4 * mm});
        }
        {
            var Q0;
            Q0=makeQuery(id+"F3.opExtrude","CAP_FACE",FACE,{"disambiguationData":[OSD([sQuery(id+"F0.wireOp",EDGE,"E2.bottom"),sQuery(id+"F0.wireOp",EDGE,"E2.top"),sQuery(id+"F0.wireOp",EDGE,"E1.right"),sQuery(id+"F0.wireOp",EDGE,"E2.right")])],"isStart":false});
            var sketch = newSketch(context, id + "F23", { "sketchPlane" : qUnion([Q0])});
            skLineSegment(sketch, "E18.bottom", {"start": v(5756.88, 289.6) * mm, "end": v(6415.16, 289.6) * mm});
            skLineSegment(sketch, "E18.top", {"start": v(5756.88, 315) * mm, "end": v(6415.16, 315) * mm});
            skLineSegment(sketch, "E18.left", {"start": v(5756.88, 289.6) * mm, "end": v(5756.88, 315) * mm});
            skLineSegment(sketch, "E18.right", {"start": v(6415.16, 289.6) * mm, "end": v(6415.16, 315) * mm});
            skLineSegment(sketch, "E19", {"start": v(5738.72, 1635.8) * mm, "end": v(9000.96, 1635.8) * mm});
            skPoint(sketch, "E19.endSnap0", {"position": v(8481.92, 1635.8) * mm});
            skLineSegment(sketch, "E20.MirrorCS", {"start": v(5756.88, 2982) * mm, "end": v(5756.88, 2956.6) * mm});
            skLineSegment(sketch, "E21.MirrorCS", {"start": v(6415.16, 2982) * mm, "end": v(6415.16, 2956.6) * mm});
            skLineSegment(sketch, "E22.MirrorCS", {"start": v(5756.88, 2982) * mm, "end": v(6415.16, 2982) * mm});
            skLineSegment(sketch, "E23.MirrorCS", {"start": v(5756.88, 2956.6) * mm, "end": v(6415.16, 2956.6) * mm});
            skSolve(sketch);
        }
        {
            var Q0;
            Q0 = qSketchRegion(id + "F23", true);
            extrude(context, id + "F24", {"entities" : qUnion([Q0]), "operationType" : NewBodyOperationType.REMOVE, "endBound" : BoundingType.THROUGH_ALL, "oppositeDirection" : true, "depth" : 3530.6 * mm});
        }
        {
            var Q0;
            Q0=makeQuery(id+"F1.opExtrude","SWEPT_FACE",FACE,{"disambiguationData":[OSD([sQuery(id+"F0.wireOp",EDGE,"E0.bottom")])]});
            var sketch = newSketch(context, id + "F25", { "sketchPlane" : qUnion([Q0])});
            skLineSegment(sketch, "E24.bottom", {"start": v(-992.28, 2082.8) * mm, "end": v(-50.8, 2082.8) * mm});
            skLineSegment(sketch, "E24.top", {"start": v(-992.28, 76.2) * mm, "end": v(-50.8, 76.2) * mm});
            skLineSegment(sketch, "E24.left", {"start": v(-992.28, 2082.8) * mm, "end": v(-992.28, 76.2) * mm});
            skLineSegment(sketch, "E24.right", {"start": v(-50.8, 2082.8) * mm, "end": v(-50.8, 76.2) * mm});
            skLineSegment(sketch, "E25.bottom", {"start": v(0, 2082.8) * mm, "end": v(861.92, 2082.8) * mm});
            skLineSegment(sketch, "E25.top", {"start": v(0, 76.2) * mm, "end": v(861.92, 76.2) * mm});
            skLineSegment(sketch, "E25.left", {"start": v(0, 2082.8) * mm, "end": v(0, 76.2) * mm});
            skLineSegment(sketch, "E25.right", {"start": v(861.92, 2082.8) * mm, "end": v(861.92, 76.2) * mm});
            skLineSegment(sketch, "E26.bottom", {"start": v(912.72, 2082.8) * mm, "end": v(1814.42, 2082.8) * mm});
            skLineSegment(sketch, "E26.top", {"start": v(912.72, 76.2) * mm, "end": v(1814.42, 76.2) * mm});
            skLineSegment(sketch, "E26.left", {"start": v(912.72, 2082.8) * mm, "end": v(912.72, 76.2) * mm});
            skLineSegment(sketch, "E26.right", {"start": v(1814.42, 2082.8) * mm, "end": v(1814.42, 76.2) * mm});
            skLineSegment(sketch, "E27.bottom", {"start": v(1865.22, 2082.8) * mm, "end": v(2766.92, 2082.8) * mm});
            skLineSegment(sketch, "E27.top", {"start": v(1865.22, 76.2) * mm, "end": v(2766.92, 76.2) * mm});
            skLineSegment(sketch, "E27.left", {"start": v(1865.22, 2082.8) * mm, "end": v(1865.22, 76.2) * mm});
            skLineSegment(sketch, "E27.right", {"start": v(2766.92, 2082.8) * mm, "end": v(2766.92, 76.2) * mm});
            skSolve(sketch);
        }
        {
            var Q0;
            Q0 = qSketchRegion(id + "F25", true);
            extrude(context, id + "F26", {"entities" : qUnion([Q0]), "operationType" : NewBodyOperationType.ADD, "depth" : 38.1 * mm});
        }
        {
            var Q0;
            Q0=makeQuery(id+"F1.opExtrude","CAP_FACE",FACE,{"disambiguationData":[OSD([sQuery(id+"F0.wireOp",EDGE,"E0.bottom"),sQuery(id+"F0.wireOp",EDGE,"E0.top"),sQuery(id+"F0.wireOp",EDGE,"E0.left"),sQuery(id+"F0.wireOp",EDGE,"E0.right")])],"isStart":false});
            var sketch = newSketch(context, id + "F27", { "sketchPlane" : qUnion([Q0])});
            skCircle(sketch, "E28", {"center": v(-821.2, -40.6) * mm, "radius": 25.24 * mm});
            skPoint(sketch, "E28.centerSnap0", {"position": v(-1017.68, -40.6) * mm});
            skSolve(sketch);
        }
        {
            var Q0;
            Q0 = qSketchRegion(id + "F27", true);
            extrude(context, id + "F28", {"entities" : qUnion([Q0]), "operationType" : NewBodyOperationType.ADD, "depth" : 127 * mm});
        }
        {
            var Q0;
            Q0=makeQuery(id+"F26.opExtrude","CAP_FACE",FACE,{"disambiguationData":[OSD([sQuery(id+"F25.wireOp",EDGE,"E25.bottom"),sQuery(id+"F25.wireOp",EDGE,"E25.top"),sQuery(id+"F25.wireOp",EDGE,"E25.left"),sQuery(id+"F25.wireOp",EDGE,"E25.right")])],"isStart":false});
            var sketch = newSketch(context, id + "F29", { "sketchPlane" : qUnion([Q0])});
            skArc(sketch, "E29", {"start": v(127, 933.54) * mm, "mid": v(101.6, 1000.04) * mm, "end": v(76.2, 933.54) * mm});
            skArc(sketch, "E30", {"start": v(1992.22, 933.54) * mm, "mid": v(1966.82, 1000.04) * mm, "end": v(1941.42, 933.54) * mm});
            skLineSegment(sketch, "E31", {"start": v(101.6, 834.94) * mm, "end": v(127, 834.94) * mm});
            skLineSegment(sketch, "E32", {"start": v(127, 834.94) * mm, "end": v(127, 933.54) * mm});
            skLineSegment(sketch, "E33", {"start": v(101.6, 834.94) * mm, "end": v(76.2, 834.94) * mm});
            skLineSegment(sketch, "E34", {"start": v(76.2, 834.94) * mm, "end": v(76.2, 933.54) * mm});
            skLineSegment(sketch, "E35.MirrorCS", {"start": v(1941.42, 834.94) * mm, "end": v(1941.42, 933.54) * mm});
            skLineSegment(sketch, "E36.MirrorCS", {"start": v(1992.22, 834.94) * mm, "end": v(1992.22, 933.54) * mm});
            skLineSegment(sketch, "E37.MirrorCS", {"start": v(1966.82, 834.94) * mm, "end": v(1992.22, 834.94) * mm});
            skLineSegment(sketch, "E38.MirrorCS", {"start": v(1966.82, 834.94) * mm, "end": v(1941.42, 834.94) * mm});
            skSolve(sketch);
        }
        {
            var Q0;
            Q0 = qSketchRegion(id + "F29", true);
            extrude(context, id + "F30", {"entities" : qUnion([Q0]), "operationType" : NewBodyOperationType.ADD, "depth" : 50.8 * mm});
        }
        {
            var Q0;
            {var subQ1=sQuery(id+"F0.wireOp",EDGE,"E2.right");var subQ3=sQuery(id+"F0.wireOp",EDGE,"E3.bottom");var subQ6=sQuery(id+"F0.wireOp",EDGE,"E1.bottom");var subQ10=sQuery(id+"F0.wireOp",EDGE,"E2.bottom");var subQ13=makeQuery(id+"F4.opExtrude","SWEPT_FACE",FACE,{"disambiguationData":[OSD([subQ1])]});Q0=makeQuery(id+"F16.boolean.opBoolean","SPLIT",FACE,{"disambiguationData":[TD([subQ13])],"derivedFrom":makeQuery(id+"F14.boolean.opBoolean","SPLIT",FACE,{"disambiguationData":[TD([subQ13])],"derivedFrom":makeQuery(id+"F4.boolean.opBoolean","MERGE",FACE,{"derivedFrom":[makeQuery(id+"F3.boolean.opBoolean","MERGE",FACE,{"derivedFrom":[makeQuery(id+"F2.opExtrude","SWEPT_FACE",FACE,{"disambiguationData":[OSD([subQ6])]}),makeQuery(id+"F3.opExtrude","SWEPT_FACE",FACE,{"disambiguationData":[OSD([subQ10])]})]}),makeQuery(id+"F4.opExtrude","SWEPT_FACE",FACE,{"disambiguationData":[OSD([subQ3])]})]})})});}
            var sketch = newSketch(context, id + "F31", { "sketchPlane" : qUnion([Q0])});
            skLineSegment(sketch, "E39.bottom", {"start": v(8481.92, 0) * mm, "end": v(10666.32, 0) * mm});
            skLineSegment(sketch, "E39.top", {"start": v(8481.92, 203.2) * mm, "end": v(10666.32, 203.2) * mm});
            skLineSegment(sketch, "E39.left", {"start": v(8481.92, 0) * mm, "end": v(8481.92, 203.2) * mm});
            skLineSegment(sketch, "E39.right", {"start": v(10666.32, 0) * mm, "end": v(10666.32, 203.2) * mm});
            skLineSegment(sketch, "E40.bottom", {"start": v(5738.77, 0) * mm, "end": v(8461.46, 0) * mm});
            skLineSegment(sketch, "E40.top", {"start": v(5738.77, 203.2) * mm, "end": v(8461.46, 203.2) * mm});
            skLineSegment(sketch, "E40.left", {"start": v(5738.77, 0) * mm, "end": v(5738.77, 203.2) * mm});
            skLineSegment(sketch, "E40.right", {"start": v(8461.46, 0) * mm, "end": v(8461.46, 203.2) * mm});
            skLineSegment(sketch, "E41.bottom", {"start": v(5738.77, 0) * mm, "end": v(2671.66, 0) * mm});
            skLineSegment(sketch, "E41.top", {"start": v(5738.77, 203.2) * mm, "end": v(2671.66, 203.2) * mm});
            skLineSegment(sketch, "E41.right", {"start": v(2671.66, 0) * mm, "end": v(2671.66, 203.2) * mm});
            skSolve(sketch);
        }
        {
            var Q0;
            Q0 = qSketchRegion(id + "F31", true);
            extrude(context, id + "F32", {"entities" : qUnion([Q0]), "operationType" : NewBodyOperationType.ADD, "depth" : 25.4 * mm});
        }
        {
            var Q0;
            {var subQ1=sQuery(id+"F0.wireOp",EDGE,"E2.right");var subQ2=sQuery(id+"F0.wireOp",EDGE,"E3.top");var subQ5=sQuery(id+"F0.wireOp",EDGE,"E1.top");var subQ6=sQuery(id+"F0.wireOp",EDGE,"E2.top");Q0=makeQuery(id+"F18.boolean.opBoolean","SPLIT",FACE,{"disambiguationData":[TD([makeQuery(id+"F4.opExtrude","SWEPT_FACE",FACE,{"disambiguationData":[OSD([subQ1])]})])],"derivedFrom":makeQuery(id+"F4.boolean.opBoolean","MERGE",FACE,{"derivedFrom":[makeQuery(id+"F3.boolean.opBoolean","MERGE",FACE,{"derivedFrom":[makeQuery(id+"F2.opExtrude","SWEPT_FACE",FACE,{"disambiguationData":[OSD([subQ5])]}),makeQuery(id+"F3.opExtrude","SWEPT_FACE",FACE,{"disambiguationData":[OSD([subQ6])]})]}),makeQuery(id+"F4.opExtrude","SWEPT_FACE",FACE,{"disambiguationData":[OSD([subQ2])]})]})});}
            var sketch = newSketch(context, id + "F33", { "sketchPlane" : qUnion([Q0])});
            skLineSegment(sketch, "E42.bottom", {"start": v(-10666.32, 0) * mm, "end": v(-8481.92, 0) * mm});
            skLineSegment(sketch, "E42.top", {"start": v(-10666.32, 203.2) * mm, "end": v(-8481.92, 203.2) * mm});
            skLineSegment(sketch, "E42.left", {"start": v(-10666.32, 0) * mm, "end": v(-10666.32, 203.2) * mm});
            skLineSegment(sketch, "E42.right", {"start": v(-8481.92, 0) * mm, "end": v(-8481.92, 203.2) * mm});
            skLineSegment(sketch, "E43.bottom", {"start": v(-8454.1, 0) * mm, "end": v(-5772.3, 0) * mm});
            skLineSegment(sketch, "E43.top", {"start": v(-8454.1, 203.2) * mm, "end": v(-5772.3, 203.2) * mm});
            skLineSegment(sketch, "E43.left", {"start": v(-8454.1, 0) * mm, "end": v(-8454.1, 203.2) * mm});
            skLineSegment(sketch, "E43.right", {"start": v(-5772.3, 0) * mm, "end": v(-5772.3, 203.2) * mm});
            skLineSegment(sketch, "E44.bottom", {"start": v(-5742.27, 0) * mm, "end": v(-928.8, 0) * mm});
            skLineSegment(sketch, "E44.top", {"start": v(-5742.27, 203.2) * mm, "end": v(-928.8, 203.2) * mm});
            skLineSegment(sketch, "E44.left", {"start": v(-5742.27, 0) * mm, "end": v(-5742.27, 203.2) * mm});
            skLineSegment(sketch, "E44.right", {"start": v(-928.8, 0) * mm, "end": v(-928.8, 203.2) * mm});
            skSolve(sketch);
        }
        {
            var Q0;
            Q0 = qSketchRegion(id + "F33", true);
            extrude(context, id + "F34", {"entities" : qUnion([Q0]), "operationType" : NewBodyOperationType.ADD, "depth" : 25.4 * mm});
        }
        {
            var Q0;
            Q0=makeQuery(id+"F34.boolean.opBoolean","MERGE",FACE,{"derivedFrom":[makeQuery(id+"F32.boolean.opBoolean","MERGE",FACE,{"derivedFrom":[makeQuery(id+"F4.opExtrude","SWEPT_FACE",FACE,{"disambiguationData":[OSD([sQuery(id+"F0.wireOp",EDGE,"E3.right")])]}),makeQuery(id+"F32.opExtrude","SWEPT_FACE",FACE,{"disambiguationData":[OSD([sQuery(id+"F31.wireOp",EDGE,"E39.right")])]})]}),makeQuery(id+"F34.opExtrude","SWEPT_FACE",FACE,{"disambiguationData":[OSD([sQuery(id+"F33.wireOp",EDGE,"E42.left")])]})]});
            var sketch = newSketch(context, id + "F35", { "sketchPlane" : qUnion([Q0])});
            skLineSegment(sketch, "E45.bottom", {"start": v(619.8, 0) * mm, "end": v(518.2, 0) * mm});
            skLineSegment(sketch, "E45.top", {"start": v(619.8, 4038.6) * mm, "end": v(518.2, 4038.6) * mm});
            skLineSegment(sketch, "E45.left", {"start": v(619.8, 0) * mm, "end": v(619.8, 4038.6) * mm});
            skLineSegment(sketch, "E45.right", {"start": v(518.2, 0) * mm, "end": v(518.2, 4038.6) * mm});
            skLineSegment(sketch, "E46.MirrorCS", {"start": v(2753.4, 0) * mm, "end": v(2753.4, 4038.6) * mm});
            skLineSegment(sketch, "E47.MirrorCS", {"start": v(2651.8, 4038.6) * mm, "end": v(2753.4, 4038.6) * mm});
            skLineSegment(sketch, "E48.MirrorCS", {"start": v(2651.8, 0) * mm, "end": v(2651.8, 4038.6) * mm});
            skLineSegment(sketch, "E49.MirrorCS", {"start": v(2651.8, 0) * mm, "end": v(2753.4, 0) * mm});
            skSolve(sketch);
        }
        {
            var Q0;
            Q0 = qSketchRegion(id + "F35", true);
            extrude(context, id + "F36", {"entities" : qUnion([Q0]), "operationType" : NewBodyOperationType.ADD, "depth" : 127 * mm});
        }
        {
            var Q0;
            Q0=makeQuery(id+"F36.opExtrude","SWEPT_FACE",FACE,{"disambiguationData":[OSD([sQuery(id+"F35.wireOp",EDGE,"E47.MirrorCS")])]});
            var sketch = newSketch(context, id + "F37", { "sketchPlane" : qUnion([Q0])});
            skLineSegment(sketch, "E50.bottom", {"start": v(10694.3, 2753.4) * mm, "end": v(10758.38, 2753.4) * mm});
            skLineSegment(sketch, "E50.top", {"start": v(10694.3, 2718.34) * mm, "end": v(10758.38, 2718.34) * mm});
            skLineSegment(sketch, "E50.left", {"start": v(10694.3, 2753.4) * mm, "end": v(10694.3, 2718.34) * mm});
            skLineSegment(sketch, "E50.right", {"start": v(10758.38, 2753.4) * mm, "end": v(10758.38, 2718.34) * mm});
            skLineSegment(sketch, "E51.bottom", {"start": v(10694.3, 2651.8) * mm, "end": v(10758.38, 2651.8) * mm});
            skLineSegment(sketch, "E51.top", {"start": v(10694.3, 2690.48) * mm, "end": v(10758.38, 2690.48) * mm});
            skLineSegment(sketch, "E51.left", {"start": v(10694.3, 2651.8) * mm, "end": v(10694.3, 2690.48) * mm});
            skLineSegment(sketch, "E51.right", {"start": v(10758.38, 2651.8) * mm, "end": v(10758.38, 2690.48) * mm});
            skLineSegment(sketch, "E52.MirrorCS", {"start": v(10694.3, 517.6) * mm, "end": v(10758.38, 517.6) * mm});
            skLineSegment(sketch, "E53.MirrorCS", {"start": v(10694.3, 517.6) * mm, "end": v(10694.3, 552.65) * mm});
            skLineSegment(sketch, "E54.MirrorCS", {"start": v(10694.3, 552.65) * mm, "end": v(10758.38, 552.65) * mm});
            skLineSegment(sketch, "E55.MirrorCS", {"start": v(10758.38, 517.6) * mm, "end": v(10758.38, 552.65) * mm});
            skLineSegment(sketch, "E56.MirrorCS", {"start": v(10694.3, 580.51) * mm, "end": v(10758.38, 580.51) * mm});
            skLineSegment(sketch, "E57.MirrorCS", {"start": v(10694.3, 619.2) * mm, "end": v(10694.3, 580.51) * mm});
            skLineSegment(sketch, "E58.MirrorCS", {"start": v(10694.3, 619.2) * mm, "end": v(10758.38, 619.2) * mm});
            skLineSegment(sketch, "E59.MirrorCS", {"start": v(10758.38, 619.2) * mm, "end": v(10758.38, 580.51) * mm});
            skSolve(sketch);
        }
        {
            var Q0;
            Q0 = qSketchRegion(id + "F37", true);
            extrude(context, id + "F38", {"entities" : qUnion([Q0]), "operationType" : NewBodyOperationType.REMOVE, "endBound" : BoundingType.THROUGH_ALL, "oppositeDirection" : true, "depth" : 25.4 * mm});
        }
        {
            var Q0;
            {var subQ0=sQuery(id+"F0.wireOp",EDGE,"E3.right");var subQ1=makeQuery(id+"F4.opExtrude","SWEPT_FACE",FACE,{"disambiguationData":[OSD([subQ0])]});var subQ3=makeQuery(id+"F22.opExtrude","SWEPT_FACE",FACE,{"disambiguationData":[OSD([sQuery(id+"F21.wireOp",EDGE,"E16.left")])]});Q0=makeQuery(id+"F36.boolean.opBoolean","SPLIT",FACE,{"disambiguationData":[TD([makeQuery(id+"F22.boolean.opBoolean","COPY",FACE,{"derivedFrom":subQ3})])],"derivedFrom":makeQuery(id+"F34.boolean.opBoolean","MERGE",FACE,{"derivedFrom":[makeQuery(id+"F32.boolean.opBoolean","MERGE",FACE,{"derivedFrom":[subQ1,makeQuery(id+"F32.opExtrude","SWEPT_FACE",FACE,{"disambiguationData":[OSD([sQuery(id+"F31.wireOp",EDGE,"E39.right")])]})]}),makeQuery(id+"F34.opExtrude","SWEPT_FACE",FACE,{"disambiguationData":[OSD([sQuery(id+"F33.wireOp",EDGE,"E42.left")])]})]})});}
            var sketch = newSketch(context, id + "F39", { "sketchPlane" : qUnion([Q0])});
            skLineSegment(sketch, "E60.bottom", {"start": v(693.96, 1828.8) * mm, "end": v(2572.05, 1828.8) * mm});
            skLineSegment(sketch, "E60.top", {"start": v(693.96, 3602.2) * mm, "end": v(2572.05, 3602.2) * mm});
            skLineSegment(sketch, "E60.left", {"start": v(693.96, 1828.8) * mm, "end": v(693.96, 3602.2) * mm});
            skLineSegment(sketch, "E60.right", {"start": v(2572.05, 1828.8) * mm, "end": v(2572.05, 3602.2) * mm});
            skSolve(sketch);
        }
        {
            var Q0;
            Q0 = qSketchRegion(id + "F39", true);
            extrude(context, id + "F40", {"entities" : qUnion([Q0]), "operationType" : NewBodyOperationType.ADD, "depth" : 101.6 * mm});
        }
        {
            var Q0;
            Q0=makeQuery(id+"F36.opExtrude","CAP_FACE",FACE,{"disambiguationData":[OSD([sQuery(id+"F35.wireOp",EDGE,"E45.bottom"),sQuery(id+"F35.wireOp",EDGE,"E45.top"),sQuery(id+"F35.wireOp",EDGE,"E45.left"),sQuery(id+"F35.wireOp",EDGE,"E45.right")])],"isStart":false});
            var sketch = newSketch(context, id + "F41", { "sketchPlane" : qUnion([Q0])});
            skLineSegment(sketch, "E61.bottom", {"start": v(518.2, 3913.17) * mm, "end": v(2749.5, 3913.17) * mm});
            skLineSegment(sketch, "E61.top", {"start": v(518.2, 4110.75) * mm, "end": v(2749.5, 4110.75) * mm});
            skLineSegment(sketch, "E61.left", {"start": v(518.2, 3913.17) * mm, "end": v(518.2, 4110.75) * mm});
            skLineSegment(sketch, "E61.right", {"start": v(2749.5, 3913.17) * mm, "end": v(2749.5, 4110.75) * mm});
            skSolve(sketch);
        }
        {
            var Q0;
            Q0 = qSketchRegion(id + "F41", true);
            extrude(context, id + "F42", {"entities" : qUnion([Q0]), "operationType" : NewBodyOperationType.ADD, "depth" : 101.6 * mm});
        }
        {
            var Q0;
            Q0=makeQuery(id+"F42.opExtrude","CAP_FACE",FACE,{"disambiguationData":[OSD([sQuery(id+"F41.wireOp",EDGE,"E61.bottom"),sQuery(id+"F41.wireOp",EDGE,"E61.top"),sQuery(id+"F41.wireOp",EDGE,"E61.left"),sQuery(id+"F41.wireOp",EDGE,"E61.right")])],"isStart":false});
            var sketch = newSketch(context, id + "F43", { "sketchPlane" : qUnion([Q0])});
            skLineSegment(sketch, "E62.bottom", {"start": v(518.2, 4059.95) * mm, "end": v(2749.5, 4059.95) * mm});
            skLineSegment(sketch, "E62.top", {"start": v(518.2, 3963.97) * mm, "end": v(2749.5, 3963.97) * mm});
            skLineSegment(sketch, "E62.left", {"start": v(518.2, 4059.95) * mm, "end": v(518.2, 3963.97) * mm});
            skLineSegment(sketch, "E62.right", {"start": v(2749.5, 4059.95) * mm, "end": v(2749.5, 3963.97) * mm});
            skSolve(sketch);
        }
        {
            var Q0;
            Q0 = qSketchRegion(id + "F43", true);
            extrude(context, id + "F44", {"entities" : qUnion([Q0]), "operationType" : NewBodyOperationType.REMOVE, "oppositeDirection" : true, "depth" : 76.2 * mm});
        }
        {
            var Q0;
            Q0=makeQuery(id+"F0.imprint","IMPRINT",FACE,{"disambiguationData":[TD([[makeQuery(id+"F0.imprint","IMPRINT",EDGE,{"derivedFrom":sQuery(id+"F0.wireOp",EDGE,"E1.bottom")}),1.0]])]});
            extrude(context, id + "F45", {"entities" : qUnion([Q0]), "operationType" : NewBodyOperationType.ADD, "depth" : 25.4 * mm});
        }
        {
            var Q0;
            Q0=makeQuery(id+"F0.imprint","IMPRINT",FACE,{"disambiguationData":[TD([[makeQuery(id+"F0.imprint","IMPRINT",EDGE,{"derivedFrom":sQuery(id+"F0.wireOp",EDGE,"E0.bottom")}),1.0]])]});
            var sketch = newSketch(context, id + "F46", { "sketchPlane" : qUnion([Q0])});
            skLineSegment(sketch, "E63.bottom", {"start": v(1430.86, 98.5) * mm, "end": v(1374.7, 98.5) * mm});
            skLineSegment(sketch, "E63.top", {"start": v(1430.86, 398.02) * mm, "end": v(1374.7, 398.02) * mm});
            skLineSegment(sketch, "E63.left", {"start": v(1430.86, 98.5) * mm, "end": v(1430.86, 398.02) * mm});
            skLineSegment(sketch, "E63.right", {"start": v(1374.7, 98.5) * mm, "end": v(1374.7, 398.02) * mm});
            skSolve(sketch);
        }
        {
            var Q0;
            Q0 = qSketchRegion(id + "F46", true);
            extrude(context, id + "F47", {"entities" : qUnion([Q0]), "operationType" : NewBodyOperationType.ADD, "depth" : 25.4 * mm});
        }
        {
            var Q0;
            Q0=qCreatedBy(makeId("Top.planeOp"),FACE);
            var sketch = newSketch(context, id + "F48", { "sketchPlane" : qUnion([Q0])});
            skLineSegment(sketch, "E64", {"start": v(10667.68, -98.65) * mm, "end": v(10640.95, -92.29) * mm});
            skLineSegment(sketch, "E65", {"start": v(10640.95, -92.29) * mm, "end": v(10640.95, -143.09) * mm});
            skLineSegment(sketch, "E66", {"start": v(10640.95, -143.09) * mm, "end": v(10691.75, -143.09) * mm});
            skLineSegment(sketch, "E67", {"start": v(10691.75, -143.09) * mm, "end": v(10691.75, -98.65) * mm});
            skLineSegment(sketch, "E68", {"start": v(10691.75, -98.65) * mm, "end": v(10667.68, -98.65) * mm});
            skLineSegment(sketch, "E69.bottom", {"start": v(5736.32, -92.29) * mm, "end": v(5787.12, -92.29) * mm});
            skLineSegment(sketch, "E69.top", {"start": v(5736.32, -143.09) * mm, "end": v(5787.12, -143.09) * mm});
            skLineSegment(sketch, "E69.left", {"start": v(5736.32, -92.29) * mm, "end": v(5736.32, -143.09) * mm});
            skLineSegment(sketch, "E69.right", {"start": v(5787.12, -92.29) * mm, "end": v(5787.12, -143.09) * mm});
            skLineSegment(sketch, "E70.bottom", {"start": v(8239.43, -149.45) * mm, "end": v(8188.63, -149.45) * mm});
            skLineSegment(sketch, "E70.top", {"start": v(8239.43, -98.65) * mm, "end": v(8188.63, -98.65) * mm});
            skLineSegment(sketch, "E70.left", {"start": v(8239.43, -149.45) * mm, "end": v(8239.43, -98.65) * mm});
            skLineSegment(sketch, "E70.right", {"start": v(8188.63, -149.45) * mm, "end": v(8188.63, -98.65) * mm});
            skPoint(sketch, "E70.middle", {"position": v(8214.03, -124.05) * mm});
            skLineSegment(sketch, "E71.bottom", {"start": v(5670.83, -92.29) * mm, "end": v(5620.03, -92.29) * mm});
            skLineSegment(sketch, "E71.top", {"start": v(5670.83, -143.09) * mm, "end": v(5620.03, -143.09) * mm});
            skLineSegment(sketch, "E71.left", {"start": v(5670.83, -92.29) * mm, "end": v(5670.83, -143.09) * mm});
            skLineSegment(sketch, "E71.right", {"start": v(5620.03, -92.29) * mm, "end": v(5620.03, -143.09) * mm});
            skLineSegment(sketch, "E72.bottom", {"start": v(3042.5, -92.29) * mm, "end": v(3093.3, -92.29) * mm});
            skLineSegment(sketch, "E72.top", {"start": v(3042.5, -143.09) * mm, "end": v(3093.3, -143.09) * mm});
            skLineSegment(sketch, "E72.left", {"start": v(3042.5, -92.29) * mm, "end": v(3042.5, -143.09) * mm});
            skLineSegment(sketch, "E72.right", {"start": v(3093.3, -92.29) * mm, "end": v(3093.3, -143.09) * mm});
            skLineSegment(sketch, "E73.bottom", {"start": v(4382.07, -143.09) * mm, "end": v(4331.27, -143.09) * mm});
            skLineSegment(sketch, "E73.top", {"start": v(4382.07, -92.29) * mm, "end": v(4331.27, -92.29) * mm});
            skLineSegment(sketch, "E73.left", {"start": v(4382.07, -143.09) * mm, "end": v(4382.07, -92.29) * mm});
            skLineSegment(sketch, "E73.right", {"start": v(4331.27, -143.09) * mm, "end": v(4331.27, -92.29) * mm});
            skPoint(sketch, "E73.middle", {"position": v(4356.67, -117.69) * mm});
            skLineSegment(sketch, "E74.bottom", {"start": v(3042.5, -177.51) * mm, "end": v(3093.3, -177.51) * mm});
            skLineSegment(sketch, "E74.top", {"start": v(3042.5, -228.31) * mm, "end": v(3093.3, -228.31) * mm});
            skLineSegment(sketch, "E74.left", {"start": v(3042.5, -177.51) * mm, "end": v(3042.5, -228.31) * mm});
            skLineSegment(sketch, "E74.right", {"start": v(3093.3, -177.51) * mm, "end": v(3093.3, -228.31) * mm});
            skLineSegment(sketch, "E75.bottom", {"start": v(3042.5, -567.44) * mm, "end": v(3093.3, -567.44) * mm});
            skLineSegment(sketch, "E75.top", {"start": v(3042.5, -516.64) * mm, "end": v(3093.3, -516.64) * mm});
            skLineSegment(sketch, "E75.left", {"start": v(3042.5, -567.44) * mm, "end": v(3042.5, -516.64) * mm});
            skLineSegment(sketch, "E75.right", {"start": v(3093.3, -567.44) * mm, "end": v(3093.3, -516.64) * mm});
            skSolve(sketch);
        }
        {
            var Q0;
            Q0 = qSketchRegion(id + "F48", true);
            extrude(context, id + "F49", {"entities" : qUnion([Q0]), "depth" : 914.4 * mm});
        }
        {
            var Q0;
            Q0=makeQuery(id+"F49.opExtrude","SWEPT_FACE",FACE,{"disambiguationData":[OSD([sQuery(id+"F48.wireOp",EDGE,"E67")])]});
            var sketch = newSketch(context, id + "F50", { "sketchPlane" : qUnion([Q0])});
            skLineSegment(sketch, "E76.bottom", {"start": v(-143.09, 914.4) * mm, "end": v(-92.29, 914.4) * mm});
            skLineSegment(sketch, "E76.top", {"start": v(-143.09, 863.6) * mm, "end": v(-92.29, 863.6) * mm});
            skLineSegment(sketch, "E76.left", {"start": v(-143.09, 914.4) * mm, "end": v(-143.09, 863.6) * mm});
            skLineSegment(sketch, "E76.right", {"start": v(-92.29, 914.4) * mm, "end": v(-92.29, 863.6) * mm});
            skLineSegment(sketch, "E77.bottom", {"start": v(-143.09, 279.4) * mm, "end": v(-92.29, 279.4) * mm});
            skLineSegment(sketch, "E77.top", {"start": v(-143.09, 330.2) * mm, "end": v(-92.29, 330.2) * mm});
            skLineSegment(sketch, "E77.left", {"start": v(-143.09, 279.4) * mm, "end": v(-143.09, 330.2) * mm});
            skLineSegment(sketch, "E77.right", {"start": v(-92.29, 279.4) * mm, "end": v(-92.29, 330.2) * mm});
            skSolve(sketch);
        }
        {
            var Q0;
            Q0 = qSketchRegion(id + "F50", true);
            extrude(context, id + "F51", {"entities" : qUnion([Q0]), "operationType" : NewBodyOperationType.ADD, "oppositeDirection" : true, "depth" : 7630.16 * mm});
        }
        {
            var Q0;
            Q0=makeQuery(id+"F49.opExtrude","SWEPT_FACE",FACE,{"disambiguationData":[OSD([sQuery(id+"F48.wireOp",EDGE,"E75.bottom")])]});
            var sketch = newSketch(context, id + "F52", { "sketchPlane" : qUnion([Q0])});
            skLineSegment(sketch, "E78.bottom", {"start": v(3042.5, 914.4) * mm, "end": v(3093.3, 914.4) * mm});
            skLineSegment(sketch, "E78.top", {"start": v(3042.5, 863.6) * mm, "end": v(3093.3, 863.6) * mm});
            skLineSegment(sketch, "E78.left", {"start": v(3042.5, 914.4) * mm, "end": v(3042.5, 863.6) * mm});
            skLineSegment(sketch, "E78.right", {"start": v(3093.3, 914.4) * mm, "end": v(3093.3, 863.6) * mm});
            skLineSegment(sketch, "E79", {"start": v(3093.3, 0) * mm, "end": v(3093.3, 279.4) * mm});
            skLineSegment(sketch, "E80.bottom", {"start": v(3093.3, 279.4) * mm, "end": v(3042.5, 279.4) * mm});
            skLineSegment(sketch, "E80.top", {"start": v(3093.3, 330.2) * mm, "end": v(3042.5, 330.2) * mm});
            skLineSegment(sketch, "E80.left", {"start": v(3093.3, 279.4) * mm, "end": v(3093.3, 330.2) * mm});
            skLineSegment(sketch, "E80.right", {"start": v(3042.5, 279.4) * mm, "end": v(3042.5, 330.2) * mm});
            skSolve(sketch);
        }
        {
            var Q0;
            Q0 = qSketchRegion(id + "F52", true);
            extrude(context, id + "F53", {"entities" : qUnion([Q0]), "operationType" : NewBodyOperationType.ADD, "oppositeDirection" : true, "depth" : 363.22 * mm});
        }
        {
            var Q0;
            Q0=qCreatedBy(makeId("Top.planeOp"),FACE);
            var sketch = newSketch(context, id + "F54", { "sketchPlane" : qUnion([Q0])});
            skLineSegment(sketch, "E81.bottom", {"start": v(922.45, -567.44) * mm, "end": v(845.37, -567.44) * mm});
            skLineSegment(sketch, "E81.top", {"start": v(922.45, -491.24) * mm, "end": v(845.37, -491.24) * mm});
            skLineSegment(sketch, "E81.left", {"start": v(922.45, -567.44) * mm, "end": v(922.45, -491.24) * mm});
            skLineSegment(sketch, "E81.right", {"start": v(845.37, -567.44) * mm, "end": v(845.37, -491.24) * mm});
            skPoint(sketch, "E81.middle", {"position": v(883.91, -529.34) * mm});
            skLineSegment(sketch, "E82.bottom", {"start": v(950.05, -567.44) * mm, "end": v(1000.85, -567.44) * mm});
            skLineSegment(sketch, "E82.top", {"start": v(950.05, -516.64) * mm, "end": v(1000.85, -516.64) * mm});
            skLineSegment(sketch, "E82.left", {"start": v(950.05, -567.44) * mm, "end": v(950.05, -516.64) * mm});
            skLineSegment(sketch, "E82.right", {"start": v(1000.85, -567.44) * mm, "end": v(1000.85, -516.64) * mm});
            skLineSegment(sketch, "E83.bottom", {"start": v(2989.33, -567.44) * mm, "end": v(2938.53, -567.44) * mm});
            skLineSegment(sketch, "E83.top", {"start": v(2989.33, -516.64) * mm, "end": v(2938.53, -516.64) * mm});
            skLineSegment(sketch, "E83.left", {"start": v(2989.33, -567.44) * mm, "end": v(2989.33, -516.64) * mm});
            skLineSegment(sketch, "E83.right", {"start": v(2938.53, -567.44) * mm, "end": v(2938.53, -516.64) * mm});
            skLineSegment(sketch, "E84.bottom", {"start": v(1844.38, -567.44) * mm, "end": v(1793.58, -567.44) * mm});
            skLineSegment(sketch, "E84.top", {"start": v(1844.38, -516.64) * mm, "end": v(1793.58, -516.64) * mm});
            skLineSegment(sketch, "E84.left", {"start": v(1844.38, -567.44) * mm, "end": v(1844.38, -516.64) * mm});
            skLineSegment(sketch, "E84.right", {"start": v(1793.58, -567.44) * mm, "end": v(1793.58, -516.64) * mm});
            skLineSegment(sketch, "E85.bottom", {"start": v(1871.4, -567.44) * mm, "end": v(1922.2, -567.44) * mm});
            skLineSegment(sketch, "E85.top", {"start": v(1871.4, -516.64) * mm, "end": v(1922.2, -516.64) * mm});
            skLineSegment(sketch, "E85.left", {"start": v(1871.4, -567.44) * mm, "end": v(1871.4, -516.64) * mm});
            skLineSegment(sketch, "E85.right", {"start": v(1922.2, -567.44) * mm, "end": v(1922.2, -516.64) * mm});
            skLineSegment(sketch, "E86.MirrorCS", {"start": v(817.78, -567.44) * mm, "end": v(766.98, -567.44) * mm});
            skLineSegment(sketch, "E87.MirrorCS", {"start": v(817.78, -567.44) * mm, "end": v(817.78, -516.64) * mm});
            skLineSegment(sketch, "E88.MirrorCS", {"start": v(817.78, -516.64) * mm, "end": v(766.98, -516.64) * mm});
            skLineSegment(sketch, "E89.MirrorCS", {"start": v(766.98, -567.44) * mm, "end": v(766.98, -516.64) * mm});
            skLineSegment(sketch, "E90.MirrorCS", {"start": v(-25.76, -567.44) * mm, "end": v(-25.76, -516.64) * mm});
            skLineSegment(sketch, "E91.MirrorCS", {"start": v(-76.56, -567.44) * mm, "end": v(-25.76, -567.44) * mm});
            skLineSegment(sketch, "E92.MirrorCS", {"start": v(-103.58, -516.64) * mm, "end": v(-154.38, -516.64) * mm});
            skLineSegment(sketch, "E93.MirrorCS", {"start": v(-154.38, -567.44) * mm, "end": v(-154.38, -516.64) * mm});
            skLineSegment(sketch, "E94.MirrorCS", {"start": v(-76.56, -516.64) * mm, "end": v(-25.76, -516.64) * mm});
            skLineSegment(sketch, "E95.MirrorCS", {"start": v(-103.58, -567.44) * mm, "end": v(-103.58, -516.64) * mm});
            skLineSegment(sketch, "E96.MirrorCS", {"start": v(-76.56, -567.44) * mm, "end": v(-76.56, -516.64) * mm});
            skLineSegment(sketch, "E97.MirrorCS", {"start": v(-103.58, -567.44) * mm, "end": v(-154.38, -567.44) * mm});
            skLineSegment(sketch, "E98.bottom", {"start": v(-1139.4, -567.44) * mm, "end": v(-1088.6, -567.44) * mm});
            skLineSegment(sketch, "E98.top", {"start": v(-1139.4, -516.64) * mm, "end": v(-1088.6, -516.64) * mm});
            skLineSegment(sketch, "E98.left", {"start": v(-1139.4, -567.44) * mm, "end": v(-1139.4, -516.64) * mm});
            skLineSegment(sketch, "E98.right", {"start": v(-1088.6, -567.44) * mm, "end": v(-1088.6, -516.64) * mm});
            skLineSegment(sketch, "E99.bottom", {"start": v(-1170.71, -567.44) * mm, "end": v(-1251.44, -567.44) * mm});
            skLineSegment(sketch, "E99.top", {"start": v(-1170.71, -475.93) * mm, "end": v(-1251.44, -475.93) * mm});
            skLineSegment(sketch, "E99.left", {"start": v(-1170.71, -567.44) * mm, "end": v(-1170.71, -475.93) * mm});
            skLineSegment(sketch, "E99.right", {"start": v(-1251.44, -567.44) * mm, "end": v(-1251.44, -475.93) * mm});
            skSolve(sketch);
        }
        {
            var Q0;
            Q0 = qSketchRegion(id + "F54", true);
            extrude(context, id + "F55", {"entities" : qUnion([Q0]), "depth" : 914.4 * mm});
        }
        {
            var Q0;
            Q0=makeQuery(id+"F55.opExtrude","CAP_FACE",FACE,{"disambiguationData":[OSD([sQuery(id+"F54.wireOp",EDGE,"E99.bottom"),sQuery(id+"F54.wireOp",EDGE,"E99.top"),sQuery(id+"F54.wireOp",EDGE,"E99.left"),sQuery(id+"F54.wireOp",EDGE,"E99.right")])],"isStart":true});
            var sketch = newSketch(context, id + "F56", { "sketchPlane" : qUnion([Q0])});
            skLineSegment(sketch, "E100", {"start": v(-1251.44, 567.44) * mm, "end": v(2988.92, 567.44) * mm});
            skLineSegment(sketch, "E101", {"start": v(2988.92, 567.44) * mm, "end": v(2988.92, 566.8) * mm});
            skLineSegment(sketch, "E102", {"start": v(2988.92, 566.8) * mm, "end": v(-1251.44, 563.56) * mm});
            skLineSegment(sketch, "E103", {"start": v(-1251.44, 563.56) * mm, "end": v(-1251.44, 567.44) * mm});
            skSolve(sketch);
        }
        {
            var Q0;
            Q0 = qSketchRegion(id + "F56", true);
            extrude(context, id + "F57", {"entities" : qUnion([Q0]), "operationType" : NewBodyOperationType.ADD, "oppositeDirection" : true, "depth" : 0.13 * mm});
        }
        {
            var Q0;
            Q0=makeQuery(id+"F57.boolean.opBoolean","MERGE",FACE,{"derivedFrom":[makeQuery(id+"F55.opExtrude","CAP_FACE",FACE,{"disambiguationData":[OSD([sQuery(id+"F54.wireOp",EDGE,"E81.bottom"),sQuery(id+"F54.wireOp",EDGE,"E81.top"),sQuery(id+"F54.wireOp",EDGE,"E81.left"),sQuery(id+"F54.wireOp",EDGE,"E81.right")])],"isStart":true}),makeQuery(id+"F55.opExtrude","CAP_FACE",FACE,{"disambiguationData":[OSD([sQuery(id+"F54.wireOp",EDGE,"E82.bottom"),sQuery(id+"F54.wireOp",EDGE,"E82.top"),sQuery(id+"F54.wireOp",EDGE,"E82.left"),sQuery(id+"F54.wireOp",EDGE,"E82.right")])],"isStart":true}),makeQuery(id+"F55.opExtrude","CAP_FACE",FACE,{"disambiguationData":[OSD([sQuery(id+"F54.wireOp",EDGE,"E83.bottom"),sQuery(id+"F54.wireOp",EDGE,"E83.top"),sQuery(id+"F54.wireOp",EDGE,"E83.left"),sQuery(id+"F54.wireOp",EDGE,"E83.right")])],"isStart":true}),makeQuery(id+"F55.opExtrude","CAP_FACE",FACE,{"disambiguationData":[OSD([sQuery(id+"F54.wireOp",EDGE,"E84.bottom"),sQuery(id+"F54.wireOp",EDGE,"E84.top"),sQuery(id+"F54.wireOp",EDGE,"E84.left"),sQuery(id+"F54.wireOp",EDGE,"E84.right")])],"isStart":true}),makeQuery(id+"F55.opExtrude","CAP_FACE",FACE,{"disambiguationData":[OSD([sQuery(id+"F54.wireOp",EDGE,"E85.bottom"),sQuery(id+"F54.wireOp",EDGE,"E85.top"),sQuery(id+"F54.wireOp",EDGE,"E85.left"),sQuery(id+"F54.wireOp",EDGE,"E85.right")])],"isStart":true}),makeQuery(id+"F55.opExtrude","CAP_FACE",FACE,{"disambiguationData":[OSD([sQuery(id+"F54.wireOp",EDGE,"E86.MirrorCS"),sQuery(id+"F54.wireOp",EDGE,"E87.MirrorCS"),sQuery(id+"F54.wireOp",EDGE,"E88.MirrorCS"),sQuery(id+"F54.wireOp",EDGE,"E89.MirrorCS")])],"isStart":true}),makeQuery(id+"F55.opExtrude","CAP_FACE",FACE,{"disambiguationData":[OSD([sQuery(id+"F54.wireOp",EDGE,"E90.MirrorCS"),sQuery(id+"F54.wireOp",EDGE,"E91.MirrorCS"),sQuery(id+"F54.wireOp",EDGE,"E94.MirrorCS"),sQuery(id+"F54.wireOp",EDGE,"E96.MirrorCS")])],"isStart":true}),makeQuery(id+"F55.opExtrude","CAP_FACE",FACE,{"disambiguationData":[OSD([sQuery(id+"F54.wireOp",EDGE,"E92.MirrorCS"),sQuery(id+"F54.wireOp",EDGE,"E93.MirrorCS"),sQuery(id+"F54.wireOp",EDGE,"E95.MirrorCS"),sQuery(id+"F54.wireOp",EDGE,"E97.MirrorCS")])],"isStart":true}),makeQuery(id+"F55.opExtrude","CAP_FACE",FACE,{"disambiguationData":[OSD([sQuery(id+"F54.wireOp",EDGE,"E98.bottom"),sQuery(id+"F54.wireOp",EDGE,"E98.top"),sQuery(id+"F54.wireOp",EDGE,"E98.left"),sQuery(id+"F54.wireOp",EDGE,"E98.right")])],"isStart":true}),makeQuery(id+"F55.opExtrude","CAP_FACE",FACE,{"disambiguationData":[OSD([sQuery(id+"F54.wireOp",EDGE,"E99.bottom"),sQuery(id+"F54.wireOp",EDGE,"E99.top"),sQuery(id+"F54.wireOp",EDGE,"E99.left"),sQuery(id+"F54.wireOp",EDGE,"E99.right")])],"isStart":true}),makeQuery(id+"F57.opExtrude","CAP_FACE",FACE,{"disambiguationData":[OSD([sQuery(id+"F56.wireOp",EDGE,"E100"),sQuery(id+"F56.wireOp",EDGE,"E101"),sQuery(id+"F56.wireOp",EDGE,"E102"),sQuery(id+"F56.wireOp",EDGE,"E103")])],"isStart":true})]});
            var sketch = newSketch(context, id + "F58", { "sketchPlane" : qUnion([Q0])});
            skLineSegment(sketch, "E104", {"start": v(2989.33, 567.44) * mm, "end": v(3044.36, 567.44) * mm});
            skLineSegment(sketch, "E105", {"start": v(3044.36, 567.44) * mm, "end": v(3044.36, 567.14) * mm});
            skLineSegment(sketch, "E106", {"start": v(3044.36, 567.14) * mm, "end": v(2989.33, 567.14) * mm});
            skLineSegment(sketch, "E107", {"start": v(2989.33, 567.14) * mm, "end": v(2989.33, 567.44) * mm});
            skLineSegment(sketch, "E108", {"start": v(3044.36, 182.81) * mm, "end": v(3044.36, 134.16) * mm});
            skLineSegment(sketch, "E109", {"start": v(3044.36, 134.16) * mm, "end": v(3044.6, 134.16) * mm});
            skLineSegment(sketch, "E110", {"start": v(3044.6, 134.16) * mm, "end": v(3044.6, 182.81) * mm});
            skLineSegment(sketch, "E111", {"start": v(3044.6, 182.81) * mm, "end": v(3044.36, 182.81) * mm});
            skSolve(sketch);
        }
        {
            var Q0;
            Q0 = qSketchRegion(id + "F58", true);
            extrude(context, id + "F59", {"entities" : qUnion([Q0]), "operationType" : NewBodyOperationType.ADD, "oppositeDirection" : true, "depth" : 0.03 * mm});
        }
        {
            var Q0;
            Q0=makeQuery(id+"F59.boolean.opBoolean","MERGE",FACE,{"derivedFrom":[makeQuery(id+"F49.opExtrude","CAP_FACE",FACE,{"disambiguationData":[OSD([sQuery(id+"F48.wireOp",EDGE,"E75.bottom"),sQuery(id+"F48.wireOp",EDGE,"E75.top"),sQuery(id+"F48.wireOp",EDGE,"E75.left"),sQuery(id+"F48.wireOp",EDGE,"E75.right")])],"isStart":true}),makeQuery(id+"F57.boolean.opBoolean","MERGE",FACE,{"derivedFrom":[makeQuery(id+"F55.opExtrude","CAP_FACE",FACE,{"disambiguationData":[OSD([sQuery(id+"F54.wireOp",EDGE,"E81.bottom"),sQuery(id+"F54.wireOp",EDGE,"E81.top"),sQuery(id+"F54.wireOp",EDGE,"E81.left"),sQuery(id+"F54.wireOp",EDGE,"E81.right")])],"isStart":true}),makeQuery(id+"F55.opExtrude","CAP_FACE",FACE,{"disambiguationData":[OSD([sQuery(id+"F54.wireOp",EDGE,"E82.bottom"),sQuery(id+"F54.wireOp",EDGE,"E82.top"),sQuery(id+"F54.wireOp",EDGE,"E82.left"),sQuery(id+"F54.wireOp",EDGE,"E82.right")])],"isStart":true}),makeQuery(id+"F55.opExtrude","CAP_FACE",FACE,{"disambiguationData":[OSD([sQuery(id+"F54.wireOp",EDGE,"E83.bottom"),sQuery(id+"F54.wireOp",EDGE,"E83.top"),sQuery(id+"F54.wireOp",EDGE,"E83.left"),sQuery(id+"F54.wireOp",EDGE,"E83.right")])],"isStart":true}),makeQuery(id+"F55.opExtrude","CAP_FACE",FACE,{"disambiguationData":[OSD([sQuery(id+"F54.wireOp",EDGE,"E84.bottom"),sQuery(id+"F54.wireOp",EDGE,"E84.top"),sQuery(id+"F54.wireOp",EDGE,"E84.left"),sQuery(id+"F54.wireOp",EDGE,"E84.right")])],"isStart":true}),makeQuery(id+"F55.opExtrude","CAP_FACE",FACE,{"disambiguationData":[OSD([sQuery(id+"F54.wireOp",EDGE,"E85.bottom"),sQuery(id+"F54.wireOp",EDGE,"E85.top"),sQuery(id+"F54.wireOp",EDGE,"E85.left"),sQuery(id+"F54.wireOp",EDGE,"E85.right")])],"isStart":true}),makeQuery(id+"F55.opExtrude","CAP_FACE",FACE,{"disambiguationData":[OSD([sQuery(id+"F54.wireOp",EDGE,"E86.MirrorCS"),sQuery(id+"F54.wireOp",EDGE,"E87.MirrorCS"),sQuery(id+"F54.wireOp",EDGE,"E88.MirrorCS"),sQuery(id+"F54.wireOp",EDGE,"E89.MirrorCS")])],"isStart":true}),makeQuery(id+"F55.opExtrude","CAP_FACE",FACE,{"disambiguationData":[OSD([sQuery(id+"F54.wireOp",EDGE,"E90.MirrorCS"),sQuery(id+"F54.wireOp",EDGE,"E91.MirrorCS"),sQuery(id+"F54.wireOp",EDGE,"E94.MirrorCS"),sQuery(id+"F54.wireOp",EDGE,"E96.MirrorCS")])],"isStart":true}),makeQuery(id+"F55.opExtrude","CAP_FACE",FACE,{"disambiguationData":[OSD([sQuery(id+"F54.wireOp",EDGE,"E92.MirrorCS"),sQuery(id+"F54.wireOp",EDGE,"E93.MirrorCS"),sQuery(id+"F54.wireOp",EDGE,"E95.MirrorCS"),sQuery(id+"F54.wireOp",EDGE,"E97.MirrorCS")])],"isStart":true}),makeQuery(id+"F55.opExtrude","CAP_FACE",FACE,{"disambiguationData":[OSD([sQuery(id+"F54.wireOp",EDGE,"E98.bottom"),sQuery(id+"F54.wireOp",EDGE,"E98.top"),sQuery(id+"F54.wireOp",EDGE,"E98.left"),sQuery(id+"F54.wireOp",EDGE,"E98.right")])],"isStart":true}),makeQuery(id+"F55.opExtrude","CAP_FACE",FACE,{"disambiguationData":[OSD([sQuery(id+"F54.wireOp",EDGE,"E99.bottom"),sQuery(id+"F54.wireOp",EDGE,"E99.top"),sQuery(id+"F54.wireOp",EDGE,"E99.left"),sQuery(id+"F54.wireOp",EDGE,"E99.right")])],"isStart":true}),makeQuery(id+"F57.opExtrude","CAP_FACE",FACE,{"disambiguationData":[OSD([sQuery(id+"F56.wireOp",EDGE,"E100"),sQuery(id+"F56.wireOp",EDGE,"E101"),sQuery(id+"F56.wireOp",EDGE,"E102"),sQuery(id+"F56.wireOp",EDGE,"E103")])],"isStart":true})]}),makeQuery(id+"F59.opExtrude","CAP_FACE",FACE,{"disambiguationData":[OSD([sQuery(id+"F58.wireOp",EDGE,"E104"),sQuery(id+"F58.wireOp",EDGE,"E105"),sQuery(id+"F58.wireOp",EDGE,"E106"),sQuery(id+"F58.wireOp",EDGE,"E107")])],"isStart":true})]});
            var sketch = newSketch(context, id + "F60", { "sketchPlane" : qUnion([Q0])});
            skLineSegment(sketch, "E112.bottom", {"start": v(2938.53, 516.64) * mm, "end": v(1922.2, 516.64) * mm});
            skLineSegment(sketch, "E112.top", {"start": v(2938.53, 566) * mm, "end": v(1922.2, 566) * mm});
            skLineSegment(sketch, "E112.left", {"start": v(2938.53, 516.64) * mm, "end": v(2938.53, 566) * mm});
            skLineSegment(sketch, "E112.right", {"start": v(1922.2, 516.64) * mm, "end": v(1922.2, 566) * mm});
            skLineSegment(sketch, "E113.bottom", {"start": v(1793.58, 516.64) * mm, "end": v(1000.85, 516.64) * mm});
            skLineSegment(sketch, "E113.top", {"start": v(1793.58, 565.29) * mm, "end": v(1000.85, 565.29) * mm});
            skLineSegment(sketch, "E113.left", {"start": v(1793.58, 516.64) * mm, "end": v(1793.58, 565.29) * mm});
            skLineSegment(sketch, "E113.right", {"start": v(1000.85, 516.64) * mm, "end": v(1000.85, 565.29) * mm});
            skLineSegment(sketch, "E114.bottom", {"start": v(766.98, 516.64) * mm, "end": v(-25.76, 516.64) * mm});
            skLineSegment(sketch, "E114.top", {"start": v(766.98, 564.5) * mm, "end": v(-25.76, 564.5) * mm});
            skLineSegment(sketch, "E114.left", {"start": v(766.98, 516.64) * mm, "end": v(766.98, 564.5) * mm});
            skLineSegment(sketch, "E114.right", {"start": v(-25.76, 516.64) * mm, "end": v(-25.76, 564.5) * mm});
            skLineSegment(sketch, "E115.bottom", {"start": v(-154.38, 516.64) * mm, "end": v(-1088.6, 516.64) * mm});
            skLineSegment(sketch, "E115.top", {"start": v(-154.38, 563.69) * mm, "end": v(-1088.6, 563.69) * mm});
            skLineSegment(sketch, "E115.left", {"start": v(-154.38, 516.64) * mm, "end": v(-154.38, 563.69) * mm});
            skLineSegment(sketch, "E115.right", {"start": v(-1088.6, 516.64) * mm, "end": v(-1088.6, 563.69) * mm});
            skSolve(sketch);
        }
        {
            var Q0;
            Q0 = qSketchRegion(id + "F60", true);
            extrude(context, id + "F61", {"entities" : qUnion([Q0]), "operationType" : NewBodyOperationType.ADD, "oppositeDirection" : true, "depth" : 50.8 * mm});
        }
        {
            var Q0;
            Q0=makeQuery(id+"F55.opExtrude","SWEPT_FACE",FACE,{"disambiguationData":[OSD([sQuery(id+"F54.wireOp",EDGE,"E83.left")])]});
            var sketch = newSketch(context, id + "F62", { "sketchPlane" : qUnion([Q0])});
            skLineSegment(sketch, "E116.bottom", {"start": v(-516.64, 914.4) * mm, "end": v(-567.44, 914.4) * mm});
            skLineSegment(sketch, "E116.top", {"start": v(-516.64, 863.6) * mm, "end": v(-567.44, 863.6) * mm});
            skLineSegment(sketch, "E116.left", {"start": v(-516.64, 914.4) * mm, "end": v(-516.64, 863.6) * mm});
            skLineSegment(sketch, "E116.right", {"start": v(-567.44, 914.4) * mm, "end": v(-567.44, 863.6) * mm});
            skLineSegment(sketch, "E117.bottom", {"start": v(-516.64, 330.2) * mm, "end": v(-567.44, 330.2) * mm});
            skLineSegment(sketch, "E117.top", {"start": v(-516.64, 279.4) * mm, "end": v(-567.44, 279.4) * mm});
            skLineSegment(sketch, "E117.left", {"start": v(-516.64, 330.2) * mm, "end": v(-516.64, 279.4) * mm});
            skLineSegment(sketch, "E117.right", {"start": v(-567.44, 330.2) * mm, "end": v(-567.44, 279.4) * mm});
            skSolve(sketch);
        }
        {
            var Q0;
            Q0 = qSketchRegion(id + "F62", true);
            extrude(context, id + "F63", {"entities" : qUnion([Q0]), "operationType" : NewBodyOperationType.ADD, "oppositeDirection" : true, "depth" : 4107.18 * mm});
        }
        {
            var Q0;
            Q0=qCreatedBy(makeId("Top.planeOp"),FACE);
            var sketch = newSketch(context, id + "F64", { "sketchPlane" : qUnion([Q0])});
            skLineSegment(sketch, "E118", {"start": v(-1017.68, 226.1) * mm, "end": v(-1017.68, 276.9) * mm});
            skLineSegment(sketch, "E119.bottom", {"start": v(-1253.23, -472.42) * mm, "end": v(-1202.43, -472.42) * mm});
            skLineSegment(sketch, "E119.top", {"start": v(-1253.23, -421.62) * mm, "end": v(-1202.43, -421.62) * mm});
            skLineSegment(sketch, "E119.left", {"start": v(-1253.23, -472.42) * mm, "end": v(-1253.23, -421.62) * mm});
            skLineSegment(sketch, "E119.right", {"start": v(-1202.43, -472.42) * mm, "end": v(-1202.43, -421.62) * mm});
            skLineSegment(sketch, "E120.bottom", {"start": v(-1253.23, 276.9) * mm, "end": v(-1202.43, 276.9) * mm});
            skLineSegment(sketch, "E120.top", {"start": v(-1253.23, 327.7) * mm, "end": v(-1202.43, 327.7) * mm});
            skLineSegment(sketch, "E120.left", {"start": v(-1253.23, 276.9) * mm, "end": v(-1253.23, 327.7) * mm});
            skLineSegment(sketch, "E120.right", {"start": v(-1202.43, 276.9) * mm, "end": v(-1202.43, 327.7) * mm});
            skLineSegment(sketch, "E121.bottom", {"start": v(-34.03, 327.7) * mm, "end": v(-84.83, 327.7) * mm});
            skLineSegment(sketch, "E121.top", {"start": v(-34.03, 276.9) * mm, "end": v(-84.83, 276.9) * mm});
            skLineSegment(sketch, "E121.left", {"start": v(-34.03, 327.7) * mm, "end": v(-34.03, 276.9) * mm});
            skLineSegment(sketch, "E121.right", {"start": v(-84.83, 327.7) * mm, "end": v(-84.83, 276.9) * mm});
            skSolve(sketch);
        }
        {
            var Q0;
            Q0 = qSketchRegion(id + "F64", true);
            extrude(context, id + "F65", {"entities" : qUnion([Q0]), "depth" : 914.4 * mm});
        }
        {
            var Q0;
            Q0=makeQuery(id+"F65.opExtrude","SWEPT_FACE",FACE,{"disambiguationData":[OSD([sQuery(id+"F64.wireOp",EDGE,"E120.top")])]});
            var sketch = newSketch(context, id + "F66", { "sketchPlane" : qUnion([Q0])});
            skLineSegment(sketch, "E122.bottom", {"start": v(1253.23, 914.4) * mm, "end": v(1202.43, 914.4) * mm});
            skLineSegment(sketch, "E122.top", {"start": v(1253.23, 863.6) * mm, "end": v(1202.43, 863.6) * mm});
            skLineSegment(sketch, "E122.left", {"start": v(1253.23, 914.4) * mm, "end": v(1253.23, 863.6) * mm});
            skLineSegment(sketch, "E122.right", {"start": v(1202.43, 914.4) * mm, "end": v(1202.43, 863.6) * mm});
            skLineSegment(sketch, "E123.bottom", {"start": v(1253.23, 332.54) * mm, "end": v(1202.43, 332.54) * mm});
            skLineSegment(sketch, "E123.top", {"start": v(1253.23, 281.74) * mm, "end": v(1202.43, 281.74) * mm});
            skLineSegment(sketch, "E123.left", {"start": v(1253.23, 332.54) * mm, "end": v(1253.23, 281.74) * mm});
            skLineSegment(sketch, "E123.right", {"start": v(1202.43, 332.54) * mm, "end": v(1202.43, 281.74) * mm});
            skSolve(sketch);
        }
        {
            var Q0;
            Q0 = qSketchRegion(id + "F66", true);
            extrude(context, id + "F67", {"entities" : qUnion([Q0]), "operationType" : NewBodyOperationType.ADD, "oppositeDirection" : true, "depth" : 774.7 * mm});
        }
        {
            var Q0;
            Q0=makeQuery(id+"F61.boolean.opBoolean","MERGE",FACE,{"derivedFrom":[makeQuery(id+"F59.boolean.opBoolean","MERGE",FACE,{"derivedFrom":[makeQuery(id+"F49.opExtrude","CAP_FACE",FACE,{"disambiguationData":[OSD([sQuery(id+"F48.wireOp",EDGE,"E75.bottom"),sQuery(id+"F48.wireOp",EDGE,"E75.top"),sQuery(id+"F48.wireOp",EDGE,"E75.left"),sQuery(id+"F48.wireOp",EDGE,"E75.right")])],"isStart":true}),makeQuery(id+"F57.boolean.opBoolean","MERGE",FACE,{"derivedFrom":[makeQuery(id+"F55.opExtrude","CAP_FACE",FACE,{"disambiguationData":[OSD([sQuery(id+"F54.wireOp",EDGE,"E81.bottom"),sQuery(id+"F54.wireOp",EDGE,"E81.top"),sQuery(id+"F54.wireOp",EDGE,"E81.left"),sQuery(id+"F54.wireOp",EDGE,"E81.right")])],"isStart":true}),makeQuery(id+"F55.opExtrude","CAP_FACE",FACE,{"disambiguationData":[OSD([sQuery(id+"F54.wireOp",EDGE,"E82.bottom"),sQuery(id+"F54.wireOp",EDGE,"E82.top"),sQuery(id+"F54.wireOp",EDGE,"E82.left"),sQuery(id+"F54.wireOp",EDGE,"E82.right")])],"isStart":true}),makeQuery(id+"F55.opExtrude","CAP_FACE",FACE,{"disambiguationData":[OSD([sQuery(id+"F54.wireOp",EDGE,"E83.bottom"),sQuery(id+"F54.wireOp",EDGE,"E83.top"),sQuery(id+"F54.wireOp",EDGE,"E83.left"),sQuery(id+"F54.wireOp",EDGE,"E83.right")])],"isStart":true}),makeQuery(id+"F55.opExtrude","CAP_FACE",FACE,{"disambiguationData":[OSD([sQuery(id+"F54.wireOp",EDGE,"E84.bottom"),sQuery(id+"F54.wireOp",EDGE,"E84.top"),sQuery(id+"F54.wireOp",EDGE,"E84.left"),sQuery(id+"F54.wireOp",EDGE,"E84.right")])],"isStart":true}),makeQuery(id+"F55.opExtrude","CAP_FACE",FACE,{"disambiguationData":[OSD([sQuery(id+"F54.wireOp",EDGE,"E85.bottom"),sQuery(id+"F54.wireOp",EDGE,"E85.top"),sQuery(id+"F54.wireOp",EDGE,"E85.left"),sQuery(id+"F54.wireOp",EDGE,"E85.right")])],"isStart":true}),makeQuery(id+"F55.opExtrude","CAP_FACE",FACE,{"disambiguationData":[OSD([sQuery(id+"F54.wireOp",EDGE,"E86.MirrorCS"),sQuery(id+"F54.wireOp",EDGE,"E87.MirrorCS"),sQuery(id+"F54.wireOp",EDGE,"E88.MirrorCS"),sQuery(id+"F54.wireOp",EDGE,"E89.MirrorCS")])],"isStart":true}),makeQuery(id+"F55.opExtrude","CAP_FACE",FACE,{"disambiguationData":[OSD([sQuery(id+"F54.wireOp",EDGE,"E90.MirrorCS"),sQuery(id+"F54.wireOp",EDGE,"E91.MirrorCS"),sQuery(id+"F54.wireOp",EDGE,"E94.MirrorCS"),sQuery(id+"F54.wireOp",EDGE,"E96.MirrorCS")])],"isStart":true}),makeQuery(id+"F55.opExtrude","CAP_FACE",FACE,{"disambiguationData":[OSD([sQuery(id+"F54.wireOp",EDGE,"E92.MirrorCS"),sQuery(id+"F54.wireOp",EDGE,"E93.MirrorCS"),sQuery(id+"F54.wireOp",EDGE,"E95.MirrorCS"),sQuery(id+"F54.wireOp",EDGE,"E97.MirrorCS")])],"isStart":true}),makeQuery(id+"F55.opExtrude","CAP_FACE",FACE,{"disambiguationData":[OSD([sQuery(id+"F54.wireOp",EDGE,"E98.bottom"),sQuery(id+"F54.wireOp",EDGE,"E98.top"),sQuery(id+"F54.wireOp",EDGE,"E98.left"),sQuery(id+"F54.wireOp",EDGE,"E98.right")])],"isStart":true}),makeQuery(id+"F55.opExtrude","CAP_FACE",FACE,{"disambiguationData":[OSD([sQuery(id+"F54.wireOp",EDGE,"E99.bottom"),sQuery(id+"F54.wireOp",EDGE,"E99.top"),sQuery(id+"F54.wireOp",EDGE,"E99.left"),sQuery(id+"F54.wireOp",EDGE,"E99.right")])],"isStart":true}),makeQuery(id+"F57.opExtrude","CAP_FACE",FACE,{"disambiguationData":[OSD([sQuery(id+"F56.wireOp",EDGE,"E100"),sQuery(id+"F56.wireOp",EDGE,"E101"),sQuery(id+"F56.wireOp",EDGE,"E102"),sQuery(id+"F56.wireOp",EDGE,"E103")])],"isStart":true})]}),makeQuery(id+"F59.opExtrude","CAP_FACE",FACE,{"disambiguationData":[OSD([sQuery(id+"F58.wireOp",EDGE,"E104"),sQuery(id+"F58.wireOp",EDGE,"E105"),sQuery(id+"F58.wireOp",EDGE,"E106"),sQuery(id+"F58.wireOp",EDGE,"E107")])],"isStart":true})]}),makeQuery(id+"F61.opExtrude","CAP_FACE",FACE,{"disambiguationData":[OSD([sQuery(id+"F60.wireOp",EDGE,"E112.bottom"),sQuery(id+"F60.wireOp",EDGE,"E112.top"),sQuery(id+"F60.wireOp",EDGE,"E112.left"),sQuery(id+"F60.wireOp",EDGE,"E112.right")])],"isStart":true}),makeQuery(id+"F61.opExtrude","CAP_FACE",FACE,{"disambiguationData":[OSD([sQuery(id+"F60.wireOp",EDGE,"E113.bottom"),sQuery(id+"F60.wireOp",EDGE,"E113.top"),sQuery(id+"F60.wireOp",EDGE,"E113.left"),sQuery(id+"F60.wireOp",EDGE,"E113.right")])],"isStart":true}),makeQuery(id+"F61.opExtrude","CAP_FACE",FACE,{"disambiguationData":[OSD([sQuery(id+"F60.wireOp",EDGE,"E114.bottom"),sQuery(id+"F60.wireOp",EDGE,"E114.top"),sQuery(id+"F60.wireOp",EDGE,"E114.left"),sQuery(id+"F60.wireOp",EDGE,"E114.right")])],"isStart":true}),makeQuery(id+"F61.opExtrude","CAP_FACE",FACE,{"disambiguationData":[OSD([sQuery(id+"F60.wireOp",EDGE,"E115.bottom"),sQuery(id+"F60.wireOp",EDGE,"E115.top"),sQuery(id+"F60.wireOp",EDGE,"E115.left"),sQuery(id+"F60.wireOp",EDGE,"E115.right")])],"isStart":true})]});
            var sketch = newSketch(context, id + "F68", { "sketchPlane" : qUnion([Q0])});
            skLineSegment(sketch, "E124", {"start": v(-1207.37, 486.9) * mm, "end": v(-1207.37, 450.4) * mm});
            skLineSegment(sketch, "E125", {"start": v(-1207.37, 450.4) * mm, "end": v(-1208.64, 450.4) * mm});
            skLineSegment(sketch, "E126", {"start": v(-1208.64, 450.4) * mm, "end": v(-1208.64, 486.9) * mm});
            skLineSegment(sketch, "E127", {"start": v(-1208.64, 486.9) * mm, "end": v(-1207.38, 486.99) * mm});
            skLineSegment(sketch, "E128", {"start": v(-1207.37, 486.9) * mm, "end": v(-1207.38, 486.99) * mm});
            skSolve(sketch);
        }
        {
            var Q0;
            Q0 = qSketchRegion(id + "F68", true);
            extrude(context, id + "F69", {"entities" : qUnion([Q0]), "operationType" : NewBodyOperationType.ADD, "oppositeDirection" : true, "depth" : 1.27 * mm});
        }
        {
            var Q0;
            Q0=makeQuery(id+"F67.boolean.opBoolean","MERGE",FACE,{"derivedFrom":[makeQuery(id+"F65.opExtrude","SWEPT_FACE",FACE,{"disambiguationData":[OSD([sQuery(id+"F64.wireOp",EDGE,"E119.left")])]}),makeQuery(id+"F65.opExtrude","SWEPT_FACE",FACE,{"disambiguationData":[OSD([sQuery(id+"F64.wireOp",EDGE,"E120.left")])]}),makeQuery(id+"F67.opExtrude","SWEPT_FACE",FACE,{"disambiguationData":[OSD([sQuery(id+"F66.wireOp",EDGE,"E122.left")])]}),makeQuery(id+"F67.opExtrude","SWEPT_FACE",FACE,{"disambiguationData":[OSD([sQuery(id+"F66.wireOp",EDGE,"E123.left")])]})]});
            var sketch = newSketch(context, id + "F70", { "sketchPlane" : qUnion([Q0])});
            skLineSegment(sketch, "E129.bottom", {"start": v(-327.7, 281.74) * mm, "end": v(-276.9, 281.74) * mm});
            skLineSegment(sketch, "E129.top", {"start": v(-327.7, 332.54) * mm, "end": v(-276.9, 332.54) * mm});
            skLineSegment(sketch, "E129.left", {"start": v(-327.7, 281.74) * mm, "end": v(-327.7, 332.54) * mm});
            skLineSegment(sketch, "E129.right", {"start": v(-276.9, 281.74) * mm, "end": v(-276.9, 332.54) * mm});
            skLineSegment(sketch, "E130.bottom", {"start": v(-327.7, 914.4) * mm, "end": v(-276.9, 914.4) * mm});
            skLineSegment(sketch, "E130.top", {"start": v(-327.7, 863.6) * mm, "end": v(-276.9, 863.6) * mm});
            skLineSegment(sketch, "E130.left", {"start": v(-327.7, 914.4) * mm, "end": v(-327.7, 863.6) * mm});
            skLineSegment(sketch, "E130.right", {"start": v(-276.9, 914.4) * mm, "end": v(-276.9, 863.6) * mm});
            skSolve(sketch);
        }
        {
            var Q0;
            Q0 = qSketchRegion(id + "F70", true);
            extrude(context, id + "F71", {"entities" : qUnion([Q0]), "operationType" : NewBodyOperationType.ADD, "oppositeDirection" : true, "depth" : 1176.02 * mm});
        }
        {
            var Q0;
            Q0=qCreatedBy(makeId("Top.planeOp"),FACE);
            var sketch = newSketch(context, id + "F72", { "sketchPlane" : qUnion([Q0])});
            skLineSegment(sketch, "E131", {"start": v(11916.18, 365.3) * mm, "end": v(11967, 365.3) * mm});
            skLineSegment(sketch, "E132", {"start": v(11967, 365.3) * mm, "end": v(11967, 416.1) * mm});
            skLineSegment(sketch, "E133", {"start": v(11967, 416.1) * mm, "end": v(11916.18, 416.1) * mm});
            skLineSegment(sketch, "E134", {"start": v(11916.18, 416.1) * mm, "end": v(11916.18, 365.3) * mm});
            skLineSegment(sketch, "E135", {"start": v(13237.04, 365.3) * mm, "end": v(13237.04, 416.1) * mm});
            skLineSegment(sketch, "E136", {"start": v(13237.04, 416.1) * mm, "end": v(13287.85, 416.1) * mm});
            skLineSegment(sketch, "E137", {"start": v(13287.85, 416.1) * mm, "end": v(13287.85, 365.3) * mm});
            skLineSegment(sketch, "E138", {"start": v(13287.85, 365.3) * mm, "end": v(13237.04, 365.3) * mm});
            skLineSegment(sketch, "E139", {"start": v(13287.85, 695.46) * mm, "end": v(13287.85, 746.23) * mm});
            skLineSegment(sketch, "E140", {"start": v(13287.85, 746.23) * mm, "end": v(13237.06, 746.23) * mm});
            skLineSegment(sketch, "E141", {"start": v(13237.06, 746.23) * mm, "end": v(13237.06, 695.46) * mm});
            skLineSegment(sketch, "E142", {"start": v(13237.06, 695.46) * mm, "end": v(13287.85, 695.46) * mm});
            skSolve(sketch);
        }
        {
            var Q0;
            Q0 = qSketchRegion(id + "F72", true);
            extrude(context, id + "F73", {"entities" : qUnion([Q0]), "depth" : 914.4 * mm});
        }
        {
            var Q0;
            Q0=qCreatedBy(makeId("Top.planeOp"),FACE);
            var sketch = newSketch(context, id + "F74", { "sketchPlane" : qUnion([Q0])});
            skLineSegment(sketch, "E143", {"start": v(11956.56, 398.24) * mm, "end": v(13244.7, 398.24) * mm});
            skLineSegment(sketch, "E144", {"start": v(13244.7, 398.24) * mm, "end": v(13244.7, 399.09) * mm});
            skLineSegment(sketch, "E145", {"start": v(13244.7, 399.09) * mm, "end": v(11956.56, 399.09) * mm});
            skLineSegment(sketch, "E146", {"start": v(11956.56, 399.09) * mm, "end": v(11956.56, 398.24) * mm});
            skSolve(sketch);
        }
        {
            var Q0;
            Q0 = qSketchRegion(id + "F74", true);
            extrude(context, id + "F75", {"entities" : qUnion([Q0]), "operationType" : NewBodyOperationType.ADD, "depth" : 12.7 * mm});
        }
        {
            var Q0;
            Q0=makeQuery(id+"F73.opExtrude","CAP_FACE",FACE,{"disambiguationData":[OSD([sQuery(id+"F72.wireOp",EDGE,"E139"),sQuery(id+"F72.wireOp",EDGE,"E140"),sQuery(id+"F72.wireOp",EDGE,"E141"),sQuery(id+"F72.wireOp",EDGE,"E142")])],"isStart":true});
            var sketch = newSketch(context, id + "F76", { "sketchPlane" : qUnion([Q0])});
            skLineSegment(sketch, "E147", {"start": v(13282.68, -411.44) * mm, "end": v(13282.68, -712.31) * mm});
            skLineSegment(sketch, "E148", {"start": v(13282.68, -712.31) * mm, "end": v(13282.4, -712.31) * mm});
            skLineSegment(sketch, "E149", {"start": v(13282.4, -712.31) * mm, "end": v(13282.4, -411.44) * mm});
            skLineSegment(sketch, "E150", {"start": v(13282.4, -411.44) * mm, "end": v(13282.68, -411.44) * mm});
            skSolve(sketch);
        }
        {
            var Q0;
            Q0 = qSketchRegion(id + "F76", true);
            extrude(context, id + "F77", {"entities" : qUnion([Q0]), "operationType" : NewBodyOperationType.ADD, "oppositeDirection" : true, "depth" : 1.27 * mm});
        }
        {
            var Q0;
            Q0=makeQuery(id+"F40.boolean.opBoolean","MERGE",FACE,{"derivedFrom":[makeQuery(id+"F22.boolean.opBoolean","COPY",FACE,{"disambiguationData":[TD([makeQuery(id+"F4.opExtrude","SWEPT_FACE",FACE,{"disambiguationData":[OSD([sQuery(id+"F0.wireOp",EDGE,"E3.right")])]})])],"derivedFrom":makeQuery(id+"F22.opExtrude","SWEPT_FACE",FACE,{"disambiguationData":[OSD([sQuery(id+"F21.wireOp",EDGE,"E17")])]})}),makeQuery(id+"F40.opExtrude","SWEPT_FACE",FACE,{"disambiguationData":[OSD([sQuery(id+"F39.wireOp",EDGE,"E60.bottom")])]})]});
            var sketch = newSketch(context, id + "F78", { "sketchPlane" : qUnion([Q0])});
            skPoint(sketch, "E151.endSnap0", {"position": v(10767.92, -1633) * mm});
            skLineSegment(sketch, "E152", {"start": v(10934.35, -1633) * mm, "end": v(10934.35, -1637.59) * mm});
            skLineSegment(sketch, "E153", {"start": v(10934.35, -1637.59) * mm, "end": v(10767.92, -1637.59) * mm});
            skLineSegment(sketch, "E154", {"start": v(10767.92, -1637.59) * mm, "end": v(10767.92, -1633) * mm});
            skLineSegment(sketch, "E155.MirrorCS", {"start": v(10934.35, -1633) * mm, "end": v(10934.35, -1628.42) * mm});
            skLineSegment(sketch, "E156.MirrorCS", {"start": v(10934.35, -1628.42) * mm, "end": v(10767.92, -1628.42) * mm});
            skLineSegment(sketch, "E157.MirrorCS", {"start": v(10767.92, -1628.42) * mm, "end": v(10767.92, -1633) * mm});
            skPoint(sketch, "E151.start.orphan", {"position": v(10767.92, -1633) * mm});
            skSolve(sketch);
        }
        {
            var Q0;
            Q0 = qSketchRegion(id + "F78", true);
            extrude(context, id + "F79", {"entities" : qUnion([Q0]), "operationType" : NewBodyOperationType.ADD, "depth" : 1.27 * mm});
        }
        {
            var Q0;
            Q0=makeQuery(id+"F73.opExtrude","SWEPT_BODY",BODY,{"disambiguationData":[OSD([sQuery(id+"F72.wireOp",EDGE,"E131"),sQuery(id+"F72.wireOp",EDGE,"E132"),sQuery(id+"F72.wireOp",EDGE,"E133"),sQuery(id+"F72.wireOp",EDGE,"E134")])]});
            var Q1;
            Q1=makeQuery(id+"F79.opExtrude","SWEPT_FACE",FACE,{"disambiguationData":[OSD([sQuery(id+"F78.wireOp",EDGE,"E153")])]});
            mirror(context, id + "F80", {"entities" : qUnion([Q0]), "mirrorPlane" : qUnion([Q1])});
        }
        {
            var Q0;
            Q0=makeQuery(id+"F77.boolean.opBoolean","MERGE",FACE,{"derivedFrom":[makeQuery(id+"F73.opExtrude","CAP_FACE",FACE,{"disambiguationData":[OSD([sQuery(id+"F72.wireOp",EDGE,"E139"),sQuery(id+"F72.wireOp",EDGE,"E140"),sQuery(id+"F72.wireOp",EDGE,"E141"),sQuery(id+"F72.wireOp",EDGE,"E142")])],"isStart":true}),makeQuery(id+"F75.boolean.opBoolean","MERGE",FACE,{"derivedFrom":[makeQuery(id+"F73.opExtrude","CAP_FACE",FACE,{"disambiguationData":[OSD([sQuery(id+"F72.wireOp",EDGE,"E131"),sQuery(id+"F72.wireOp",EDGE,"E132"),sQuery(id+"F72.wireOp",EDGE,"E133"),sQuery(id+"F72.wireOp",EDGE,"E134")])],"isStart":true}),makeQuery(id+"F73.opExtrude","CAP_FACE",FACE,{"disambiguationData":[OSD([sQuery(id+"F72.wireOp",EDGE,"E135"),sQuery(id+"F72.wireOp",EDGE,"E136"),sQuery(id+"F72.wireOp",EDGE,"E137"),sQuery(id+"F72.wireOp",EDGE,"E138")])],"isStart":true}),makeQuery(id+"F75.opExtrude","CAP_FACE",FACE,{"disambiguationData":[OSD([sQuery(id+"F74.wireOp",EDGE,"E143"),sQuery(id+"F74.wireOp",EDGE,"E144"),sQuery(id+"F74.wireOp",EDGE,"E145"),sQuery(id+"F74.wireOp",EDGE,"E146")])],"isStart":true})]}),makeQuery(id+"F77.opExtrude","CAP_FACE",FACE,{"disambiguationData":[OSD([sQuery(id+"F76.wireOp",EDGE,"E147"),sQuery(id+"F76.wireOp",EDGE,"E148"),sQuery(id+"F76.wireOp",EDGE,"E149"),sQuery(id+"F76.wireOp",EDGE,"E150")])],"isStart":true})]});
            var sketch = newSketch(context, id + "F81", { "sketchPlane" : qUnion([Q0])});
            skLineSegment(sketch, "E158", {"start": v(13287.85, -746.23) * mm, "end": v(13287.85, -2544.29) * mm});
            skLineSegment(sketch, "E159", {"start": v(13287.85, -2544.29) * mm, "end": v(13287.54, -2544.29) * mm});
            skLineSegment(sketch, "E160", {"start": v(13287.54, -2544.29) * mm, "end": v(13287.54, -744.86) * mm});
            skLineSegment(sketch, "E161", {"start": v(13287.54, -744.86) * mm, "end": v(13287.85, -746.23) * mm});
            skSolve(sketch);
        }
        {
            var Q0;
            Q0 = qSketchRegion(id + "F81", true);
            extrude(context, id + "F82", {"entities" : qUnion([Q0]), "operationType" : NewBodyOperationType.ADD, "oppositeDirection" : true, "depth" : 0.13 * mm});
        }
        {
            var Q0;
            Q0=makeQuery(id+"F73.opExtrude","CAP_FACE",FACE,{"disambiguationData":[OSD([sQuery(id+"F72.wireOp",EDGE,"E131"),sQuery(id+"F72.wireOp",EDGE,"E132"),sQuery(id+"F72.wireOp",EDGE,"E133"),sQuery(id+"F72.wireOp",EDGE,"E134")])],"isStart":false});
            var sketch = newSketch(context, id + "F83", { "sketchPlane" : qUnion([Q0])});
            skLineSegment(sketch, "E162", {"start": v(11967, 365.3) * mm, "end": v(11967, 416.1) * mm});
            skLineSegment(sketch, "E163", {"start": v(11967, 416.1) * mm, "end": v(13245.64, 416.1) * mm});
            skLineSegment(sketch, "E164", {"start": v(13245.64, 416.1) * mm, "end": v(13245.64, 365.3) * mm});
            skLineSegment(sketch, "E165", {"start": v(13245.64, 365.3) * mm, "end": v(11967, 365.3) * mm});
            skLineSegment(sketch, "E166", {"start": v(13237.52, 416.1) * mm, "end": v(13237.52, 705.26) * mm});
            skLineSegment(sketch, "E167", {"start": v(13237.52, 705.26) * mm, "end": v(13286.67, 705.26) * mm});
            skLineSegment(sketch, "E168", {"start": v(13286.67, 705.26) * mm, "end": v(13286.67, 404.3) * mm});
            skLineSegment(sketch, "E169", {"start": v(13286.67, 404.3) * mm, "end": v(13237.52, 416.1) * mm});
            skLineSegment(sketch, "E170.bottom", {"start": v(13237.34, 2864.37) * mm, "end": v(13287.13, 2864.37) * mm});
            skLineSegment(sketch, "E170.top", {"start": v(13237.34, 2572.46) * mm, "end": v(13287.13, 2572.46) * mm});
            skLineSegment(sketch, "E170.left", {"start": v(13237.34, 2864.37) * mm, "end": v(13237.34, 2572.46) * mm});
            skLineSegment(sketch, "E170.right", {"start": v(13287.13, 2864.37) * mm, "end": v(13287.13, 2572.46) * mm});
            skLineSegment(sketch, "E171.bottom", {"start": v(13237.63, 2909.4) * mm, "end": v(11959.84, 2909.4) * mm});
            skLineSegment(sketch, "E171.top", {"start": v(13237.63, 2860.06) * mm, "end": v(11959.84, 2860.06) * mm});
            skLineSegment(sketch, "E171.left", {"start": v(13237.63, 2909.4) * mm, "end": v(13237.63, 2860.06) * mm});
            skLineSegment(sketch, "E171.right", {"start": v(11959.84, 2909.4) * mm, "end": v(11959.84, 2860.06) * mm});
            skSolve(sketch);
        }
        {
            var Q0;
            Q0 = qSketchRegion(id + "F83", true);
            extrude(context, id + "F84", {"entities" : qUnion([Q0]), "operationType" : NewBodyOperationType.ADD, "oppositeDirection" : true, "depth" : 50.8 * mm});
        }
        {
            var Q0;
            Q0=makeQuery(id+"F84.boolean.opBoolean","MERGE",FACE,{"derivedFrom":[makeQuery(id+"F73.opExtrude","SWEPT_FACE",FACE,{"disambiguationData":[OSD([sQuery(id+"F72.wireOp",EDGE,"E131")])]}),makeQuery(id+"F73.opExtrude","SWEPT_FACE",FACE,{"disambiguationData":[OSD([sQuery(id+"F72.wireOp",EDGE,"E138")])]}),makeQuery(id+"F84.opExtrude","SWEPT_FACE",FACE,{"disambiguationData":[OSD([sQuery(id+"F83.wireOp",EDGE,"E165")])]})]});
            var sketch = newSketch(context, id + "F85", { "sketchPlane" : qUnion([Q0])});
            skLineSegment(sketch, "E172.bottom", {"start": v(11933.24, 279.4) * mm, "end": v(13250.3, 279.4) * mm});
            skLineSegment(sketch, "E172.top", {"start": v(11933.24, 331.96) * mm, "end": v(13250.3, 331.96) * mm});
            skLineSegment(sketch, "E172.left", {"start": v(11933.24, 279.4) * mm, "end": v(11933.24, 331.96) * mm});
            skLineSegment(sketch, "E172.right", {"start": v(13250.3, 279.4) * mm, "end": v(13250.3, 331.96) * mm});
            skSolve(sketch);
        }
        {
            var Q0;
            Q0 = qSketchRegion(id + "F85", true);
            extrude(context, id + "F86", {"entities" : qUnion([Q0]), "operationType" : NewBodyOperationType.ADD, "oppositeDirection" : true, "depth" : 50.8 * mm});
        }
        {
            var Q0;
            Q0=makeQuery(id+"F73.opExtrude","SWEPT_FACE",FACE,{"disambiguationData":[OSD([sQuery(id+"F72.wireOp",EDGE,"E137")])]});
            var sketch = newSketch(context, id + "F87", { "sketchPlane" : qUnion([Q0])});
            skLineSegment(sketch, "E173", {"start": v(365.3, 0) * mm, "end": v(365.3, 279.4) * mm});
            skLineSegment(sketch, "E174", {"start": v(365.3, 279.4) * mm, "end": v(731.77, 279.4) * mm});
            skLineSegment(sketch, "E175", {"start": v(731.77, 279.4) * mm, "end": v(731.77, 330.29) * mm});
            skLineSegment(sketch, "E176", {"start": v(731.77, 330.29) * mm, "end": v(393.1, 330.29) * mm});
            skLineSegment(sketch, "E177", {"start": v(393.1, 330.29) * mm, "end": v(365.3, 279.4) * mm});
            skSolve(sketch);
        }
        {
            var Q0;
            Q0 = qSketchRegion(id + "F87", true);
            extrude(context, id + "F88", {"entities" : qUnion([Q0]), "operationType" : NewBodyOperationType.ADD, "oppositeDirection" : true, "depth" : 50.8 * mm});
        }
        {
            var Q0;
            {var subQ0=makeQuery(id+"F73.opExtrude","SWEPT_FACE",FACE,{"disambiguationData":[OSD([sQuery(id+"F72.wireOp",EDGE,"E139")])]});Q0=makeQuery(id+"F88.boolean.opBoolean","MERGE",FACE,{"derivedFrom":[makeQuery(id+"F73.opExtrude","SWEPT_FACE",FACE,{"disambiguationData":[OSD([sQuery(id+"F72.wireOp",EDGE,"E137")])]}),makeQuery(id+"F82.boolean.opBoolean","MERGE",FACE,{"derivedFrom":[subQ0,makeQuery(id+"F80.opPattern","COPY",FACE,{"derivedFrom":subQ0,"instanceName":"1"}),makeQuery(id+"F82.opExtrude","SWEPT_FACE",FACE,{"disambiguationData":[OSD([sQuery(id+"F81.wireOp",EDGE,"E158")])]})]}),makeQuery(id+"F88.opExtrude","CAP_FACE",FACE,{"disambiguationData":[OSD([sQuery(id+"F87.wireOp",EDGE,"E174"),sQuery(id+"F87.wireOp",EDGE,"E175"),sQuery(id+"F87.wireOp",EDGE,"E176"),sQuery(id+"F87.wireOp",EDGE,"E177")])],"isStart":true})]});}
            var sketch = newSketch(context, id + "F89", { "sketchPlane" : qUnion([Q0])});
            skLineSegment(sketch, "E178", {"start": v(2579.72, 0) * mm, "end": v(2579.72, 280.17) * mm});
            skLineSegment(sketch, "E179", {"start": v(2579.72, 280.17) * mm, "end": v(2892.4, 280.17) * mm});
            skLineSegment(sketch, "E180", {"start": v(2892.4, 280.17) * mm, "end": v(2892.4, 331) * mm});
            skLineSegment(sketch, "E181", {"start": v(2892.4, 331) * mm, "end": v(2544.54, 331) * mm});
            skLineSegment(sketch, "E182", {"start": v(2544.54, 331) * mm, "end": v(2579.72, 280.17) * mm});
            skSolve(sketch);
        }
        {
            var Q0;
            Q0 = qSketchRegion(id + "F89", true);
            extrude(context, id + "F90", {"entities" : qUnion([Q0]), "operationType" : NewBodyOperationType.ADD, "oppositeDirection" : true, "depth" : 50.8 * mm});
        }
        {
            var Q0;
            Q0=makeQuery(id+"F80.opPattern","COPY",FACE,{"derivedFrom":makeQuery(id+"F73.opExtrude","SWEPT_FACE",FACE,{"disambiguationData":[OSD([sQuery(id+"F72.wireOp",EDGE,"E138")])]}),"instanceName":"1"});
            var sketch = newSketch(context, id + "F91", { "sketchPlane" : qUnion([Q0])});
            skLineSegment(sketch, "E183", {"start": v(-13244.16, 332.13) * mm, "end": v(-11944.6, 332.13) * mm});
            skLineSegment(sketch, "E184", {"start": v(-11944.6, 332.13) * mm, "end": v(-11965.94, 279.52) * mm});
            skLineSegment(sketch, "E185", {"start": v(-11965.94, 279.52) * mm, "end": v(-13254.7, 279.52) * mm});
            skLineSegment(sketch, "E186", {"start": v(-13254.7, 279.52) * mm, "end": v(-13244.16, 332.13) * mm});
            skSolve(sketch);
        }
        {
            var Q0;
            Q0 = qSketchRegion(id + "F91", true);
            extrude(context, id + "F92", {"entities" : qUnion([Q0]), "operationType" : NewBodyOperationType.ADD, "oppositeDirection" : true, "depth" : 50.8 * mm});
        }
    });
